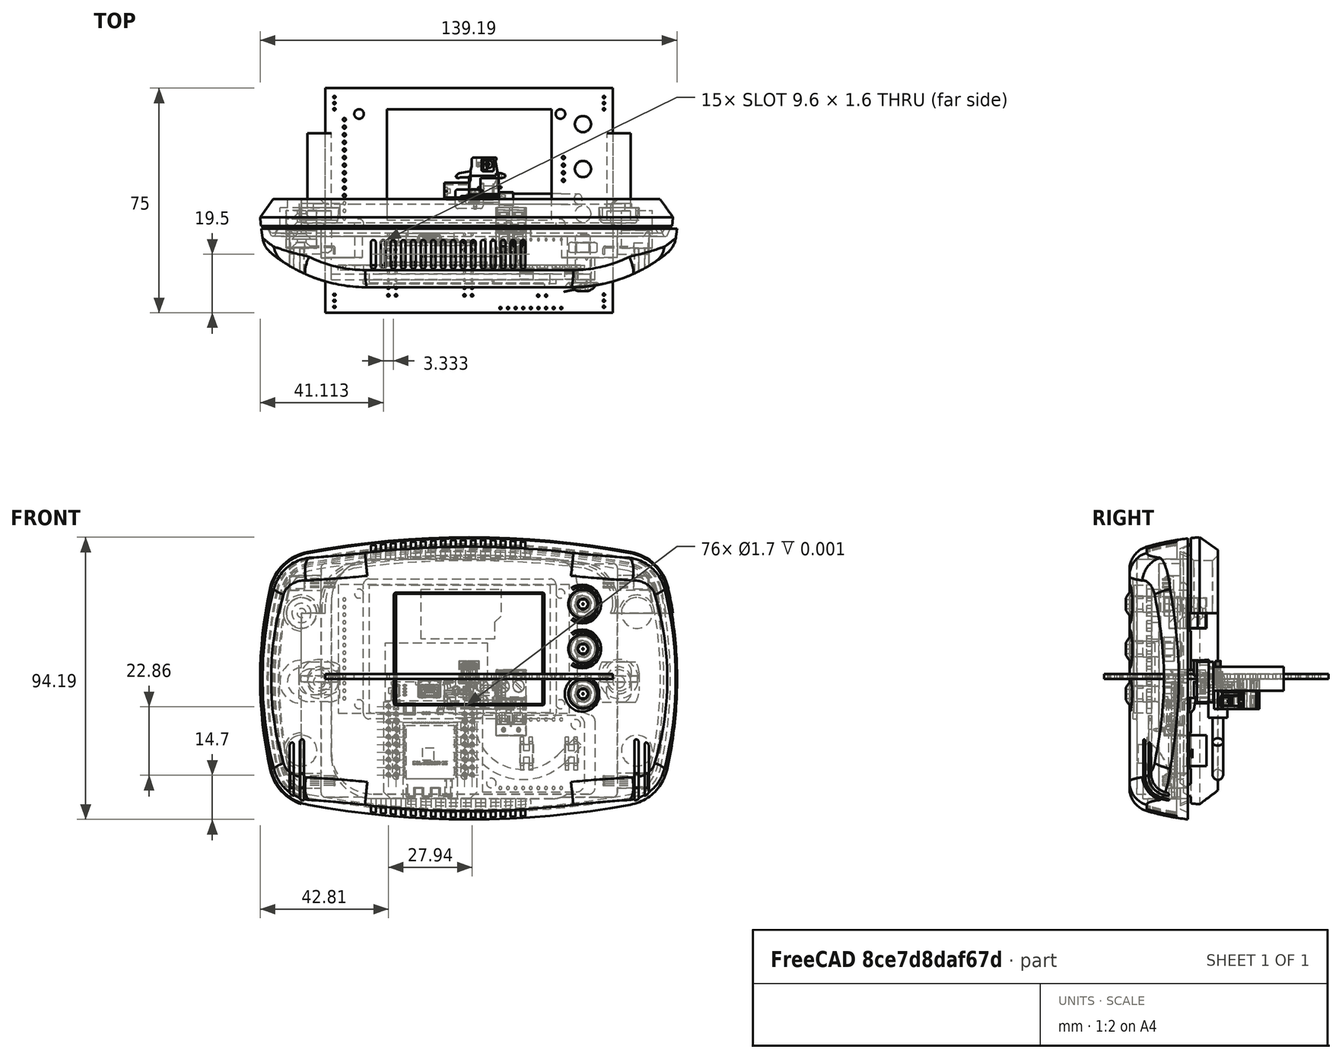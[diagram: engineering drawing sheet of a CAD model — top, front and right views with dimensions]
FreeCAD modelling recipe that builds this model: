
FCSTD DOCUMENT  (FreeCAD 1.0R38806 (Git))
Label: RoomThermostat with PCB
License: All rights reserved
LicenseURL: http://en.wikipedia.org/wiki/All_rights_reserved
objects: Sketcher::SketchObject×95, PartDesign::Body×35, PartDesign::Pocket×23, PartDesign::Pad×19, PartDesign::Mirrored×15, PartDesign::AdditivePipe×14, Part::Compound×8, Part::FeaturePython×8, PartDesign::SubtractivePipe×8, PartDesign::MultiTransform×7, Part::Feature×5, PartDesign::Revolution×5, PartDesign::Groove×5, PartDesign::LinearPattern×4, App::Part×4, App::LinkGroup×4, PartDesign::Fillet×3, PartDesign::Plane×2, Mesh::Feature×2, App::DocumentObjectGroup×1
note: 531 computed .brp shape members not serialized (recipe doc carries the construction recipe); baked Part::Feature solids carry a one-line shape summary decoded from their .brp

FEATURE [Sketcher::SketchObject] Sketch  label="gl base"
  ArcFitTolerance = 0
  AttachmentSupport = -> [XZ_Plane]
  FullyConstrained = true
  MakeInternals = false
  MapMode = 5
  Placement = pos=(0,0,0) rot=(1,0,0;1.5708rad)
  sketch-geometry (8):
    g0: LineSegment StartX=-33.28 StartY=21.36 StartZ=0 EndX=26.98 EndY=21.36 EndZ=0
    g1: LineSegment StartX=26.98 StartY=21.36 StartZ=0 EndX=26.98 EndY=-21.36 EndZ=0
    g2: LineSegment StartX=26.98 StartY=-21.36 StartZ=0 EndX=-33.28 EndY=-21.36 EndZ=0
    g3: LineSegment StartX=-33.28 StartY=-21.36 StartZ=0 EndX=-33.28 EndY=21.36 EndZ=0
    g4: LineSegment [constr] StartX=-24.48 StartY=18.36 StartZ=0 EndX=24.48 EndY=18.36 EndZ=0
    g5: LineSegment [constr] StartX=24.48 StartY=18.36 StartZ=0 EndX=24.48 EndY=-18.36 EndZ=0
    g6: LineSegment [constr] StartX=24.48 StartY=-18.36 StartZ=0 EndX=-24.48 EndY=-18.36 EndZ=0
    g7: LineSegment [constr] StartX=-24.48 StartY=-18.36 StartZ=0 EndX=-24.48 EndY=18.36 EndZ=0
  constraints (21):
    c: Coincident(g0,g1)
    c: Coincident(g1,g2)
    c: Coincident(g2,g3)
    c: Coincident(g3,g0)
    c: Horizontal(g2)
    c: Vertical(g3)
    c: DistanceX(g0,g0) = 60.26
    c: DistanceY(g1,g1) = 42.72
    c: Coincident(g4,g5)
    c: Coincident(g5,g6)
    c: Coincident(g6,g7)
    c: Coincident(g7,g4)
    c: Horizontal(g6)
    c: Vertical(g7)
    c: Horizontal(g0)
    c: Symmetric(g4,g4,g-2)
    c: Symmetric(g4,g5,g-1)
    c: DistanceX(g4,g4) = 48.96
    c: DistanceX(g4,g0) = 2.5
    c: DistanceY(g5,g5) = 36.72
    c: Symmetric(g0,g1,g-1)
FEATURE [PartDesign::Pad] Pad  label="GL Base"
  Direction = (1,1,1)
  Length = 4.2
  Length2 = 100
  Placement = pos=(0,0,0) rot=(1,0,0;1.5708rad)
  Profile = -> Sketch
  Reversed = true
  Suppressed = false
  Type = 0
FEATURE [Sketcher::SketchObject] Sketch001  label="gl active area"
  ArcFitTolerance = 0
  AttachmentSupport = -> [XZ_Plane]
  FullyConstrained = true
  MakeInternals = false
  MapMode = 5
  Placement = pos=(0,0,0) rot=(1,0,0;1.5708rad)
  sketch-geometry (4):
    g0: LineSegment StartX=-24.48 StartY=18.36 StartZ=0 EndX=24.48 EndY=18.36 EndZ=0
    g1: LineSegment StartX=24.48 StartY=18.36 StartZ=0 EndX=24.48 EndY=-18.36 EndZ=0
    g2: LineSegment StartX=24.48 StartY=-18.36 StartZ=0 EndX=-24.48 EndY=-18.36 EndZ=0
    g3: LineSegment StartX=-24.48 StartY=-18.36 StartZ=0 EndX=-24.48 EndY=18.36 EndZ=0
  constraints (10):
    c: Coincident(g0,g1)
    c: Coincident(g1,g2)
    c: Coincident(g2,g3)
    c: Coincident(g3,g0)
    c: Horizontal(g2)
    c: Vertical(g3)
    c: Symmetric(g0,g0,g-2)
    c: Symmetric(g0,g1,g-1)
    c: DistanceY(g1,g1) = 36.72
    c: DistanceX(g0,g0) = 48.96
FEATURE [PartDesign::Pad] Pad001  label="GL active area"
  BaseFeature = -> Pad
  Direction = (1,1,1)
  Length = 0.1
  Length2 = 100
  Placement = pos=(0,0,0) rot=(1,0,0;1.5708rad)
  Profile = -> Sketch001
  Suppressed = false
  Type = 0
FEATURE [PartDesign::Body] Body  label="Glass"
  AllowCompound = false
  Group = -> [Sketch,Pad,Sketch001,Pad001]
  Origin = -> Origin
  Tip = -> Pad001
FEATURE [Sketcher::SketchObject] Sketch003  label="pc skeleton"
  ArcFitTolerance = 0
  AttachmentSupport = -> [XZ_Plane001]
  FullyConstrained = true
  MakeInternals = false
  MapMode = 5
  Placement = pos=(0,0,0) rot=(1,0,0;1.5708rad)
  sketch-geometry (8):
    g0: LineSegment StartX=-33.28 StartY=21.36 StartZ=0 EndX=26.98 EndY=21.36 EndZ=0
    g1: LineSegment StartX=26.98 StartY=21.36 StartZ=0 EndX=26.98 EndY=-21.36 EndZ=0
    g2: LineSegment StartX=26.98 StartY=-21.36 StartZ=0 EndX=-33.28 EndY=-21.36 EndZ=0
    g3: LineSegment StartX=-33.28 StartY=-21.36 StartZ=0 EndX=-33.28 EndY=21.36 EndZ=0
    g4: LineSegment StartX=-24.48 StartY=18.36 StartZ=0 EndX=24.48 EndY=18.36 EndZ=0
    g5: LineSegment StartX=24.48 StartY=18.36 StartZ=0 EndX=24.48 EndY=-18.36 EndZ=0
    g6: LineSegment StartX=24.48 StartY=-18.36 StartZ=0 EndX=-24.48 EndY=-18.36 EndZ=0
    g7: LineSegment StartX=-24.48 StartY=-18.36 StartZ=0 EndX=-24.48 EndY=18.36 EndZ=0
  constraints (22):
    c: Coincident(g0,g1)
    c: Coincident(g1,g2)
    c: Coincident(g2,g3)
    c: Coincident(g3,g0)
    c: Horizontal(g2)
    c: Vertical(g3)
    c: DistanceX(g0,g0) = 60.26
    c: DistanceY(g1,g1) = 42.72
    c: Coincident(g4,g5)
    c: Coincident(g5,g6)
    c: Coincident(g6,g7)
    c: Coincident(g7,g4)
    c: Horizontal(g6)
    c: Vertical(g7)
    c: Horizontal(g0)
    c: Symmetric(g4,g4,g-2)
    c: Symmetric(g4,g5,g-1)
    c: DistanceX(g4,g4) = 48.96
    c: DistanceX(g4,g0) = 2.5
    c: DistanceY(g5,g5) = 36.72
    c: Symmetric(g0,g1,g-1)
    c: DistanceX(g0,g-1) = 33.28
FEATURE [Sketcher::SketchObject] Sketch002  label="pc base"
  ArcFitTolerance = 0
  AttachmentOffset = pos=(0,0,-4.2) rot=(0,0,1;0rad)
  AttachmentSupport = -> [XZ_Plane001]
  ExternalGeometry = -> [Sketch003]
  FullyConstrained = true
  MakeInternals = false
  MapMode = 5
  Placement = pos=(0,4.2,-9e-16) rot=(1,0,0;1.5708rad)
  sketch-geometry (12):
    g0: LineSegment StartX=33.49 StartY=21.45 StartZ=0 EndX=-43.69 EndY=21.45 EndZ=0
    g1: LineSegment StartX=-43.69 StartY=21.45 StartZ=0 EndX=-43.69 EndY=-21.45 EndZ=0
    g2: LineSegment StartX=-43.69 StartY=-21.45 StartZ=0 EndX=33.49 EndY=-21.45 EndZ=0
    g3: LineSegment StartX=33.49 StartY=-21.45 StartZ=0 EndX=33.49 EndY=21.45 EndZ=0
    g4: LineSegment [constr] StartX=-36.77 StartY=18.45 StartZ=0 EndX=30.49 EndY=18.45 EndZ=0
    g5: LineSegment [constr] StartX=30.49 StartY=18.45 StartZ=0 EndX=30.49 EndY=-18.45 EndZ=0
    g6: LineSegment [constr] StartX=30.49 StartY=-18.45 StartZ=0 EndX=-36.77 EndY=-18.45 EndZ=0
    g7: LineSegment [constr] StartX=-36.77 StartY=-18.45 StartZ=0 EndX=-36.77 EndY=18.45 EndZ=0
    g8: Circle CenterX=30.49 CenterY=18.45 CenterZ=0 NormalX=0 NormalY=0 NormalZ=1 AngleXU=0 Radius=1.5
    g9: Circle CenterX=30.49 CenterY=-18.45 CenterZ=0 NormalX=0 NormalY=0 NormalZ=1 AngleXU=0 Radius=1.5
    g10: Circle CenterX=-36.77 CenterY=-18.45 CenterZ=0 NormalX=0 NormalY=0 NormalZ=1 AngleXU=0 Radius=1.5
    g11: Circle CenterX=-36.77 CenterY=18.45 CenterZ=0 NormalX=0 NormalY=0 NormalZ=1 AngleXU=0 Radius=1.5
  constraints (31):
    c: Coincident(g0,g1)
    c: Coincident(g1,g2)
    c: Coincident(g2,g3)
    c: Coincident(g3,g0)
    c: Horizontal(g0)
    c: Horizontal(g2)
    c: Vertical(g1)
    c: Symmetric(g0,g2,g-1)
    c: DistanceX(g0,g-3) = 10.41
    c: DistanceX(g0,g0) = 77.18
    c: DistanceY(g3,g3) = 42.9
    c: Coincident(g4,g5)
    c: Coincident(g5,g6)
    c: Coincident(g6,g7)
    c: Coincident(g7,g4)
    c: Horizontal(g4)
    c: Horizontal(g6)
    c: Vertical(g7)
    c: Symmetric(g4,g5,g-1)
    c: Coincident(g8,g4)
    c: Coincident(g9,g5)
    c: Coincident(g10,g6)
    c: Coincident(g11,g4)
    c: Equal(g8,g11)
    c: Equal(g11,g10)
    c: Equal(g10,g9)
    c: Radius(g9) = 1.5
    c: DistanceX(g0,g11) = 6.92
    c: DistanceX(g8,g0) = 3
    c: DistanceY(g8,g0) = 3
    c: DistanceX(g0,g-1) = 43.69
FEATURE [PartDesign::Pad] Pad002  label="PC base"
  Direction = (1,1,1)
  Length = 1.6
  Length2 = 100
  Placement = pos=(0,0,0) rot=(1,0,0;1.5708rad)
  Profile = -> Sketch002
  Reversed = true
  Suppressed = false
  Type = 0
FEATURE [Sketcher::SketchObject] Sketch004  label="pc hole"
  ArcFitTolerance = 0
  AttachmentSupport = -> [XZ_Plane001]
  ExternalGeometry = -> [Sketch002]
  FullyConstrained = true
  MakeInternals = false
  MapMode = 5
  Placement = pos=(0,0,0) rot=(1,0,0;1.5708rad)
  sketch-geometry (1):
    g0: Circle CenterX=-41.69 CenterY=-16.51 CenterZ=0 NormalX=0 NormalY=0 NormalZ=1 AngleXU=0 Radius=0.5
  constraints (3):
    c: Radius(g0) = 0.5
    c: DistanceY(g0,g-1) = 16.51
    c: DistanceX(g0,g-1) = 41.69
FEATURE [PartDesign::Pocket] Pocket  label="PC FirstHole"
  BaseFeature = -> Pad002
  Direction = (1,1,1)
  Length = 5
  Length2 = 100
  Midplane = true
  Placement = pos=(0,0,0) rot=(1,0,0;1.5708rad)
  Profile = -> Sketch004
  Suppressed = false
  Type = 1
FEATURE [PartDesign::LinearPattern] LinearPattern  label="PC OtherHoles"
  BaseFeature = -> Pocket
  Direction = -> Z_Axis001
  Length = 33.02
  Mode = 0
  Occurrences = 14
  Offset = 2.54
  Originals = -> [Pocket]
  Placement = pos=(0,0,0) rot=(1,0,0;1.5708rad)
  Suppressed = false
  TransformMode = 0
FEATURE [PartDesign::Body] Body001  label="PCB"
  AllowCompound = false
  Group = -> [Sketch002,Sketch003,Pad002,Sketch004,Pocket,LinearPattern]
  Origin = -> Origin001
  Tip = -> LinearPattern
FEATURE [Sketcher::SketchObject] Sketch006  label="sd skeleton"
  ArcFitTolerance = 0
  AttachmentSupport = -> [XZ_Plane002]
  FullyConstrained = true
  MakeInternals = false
  MapMode = 5
  Placement = pos=(0,0,0) rot=(1,0,0;1.5708rad)
  sketch-geometry (8):
    g0: LineSegment StartX=-33.28 StartY=21.36 StartZ=0 EndX=26.98 EndY=21.36 EndZ=0
    g1: LineSegment StartX=26.98 StartY=21.36 StartZ=0 EndX=26.98 EndY=-21.36 EndZ=0
    g2: LineSegment StartX=26.98 StartY=-21.36 StartZ=0 EndX=-33.28 EndY=-21.36 EndZ=0
    g3: LineSegment StartX=-33.28 StartY=-21.36 StartZ=0 EndX=-33.28 EndY=21.36 EndZ=0
    g4: LineSegment StartX=-24.48 StartY=18.36 StartZ=0 EndX=24.48 EndY=18.36 EndZ=0
    g5: LineSegment StartX=24.48 StartY=18.36 StartZ=0 EndX=24.48 EndY=-18.36 EndZ=0
    g6: LineSegment StartX=24.48 StartY=-18.36 StartZ=0 EndX=-24.48 EndY=-18.36 EndZ=0
    g7: LineSegment StartX=-24.48 StartY=-18.36 StartZ=0 EndX=-24.48 EndY=18.36 EndZ=0
  constraints (21):
    c: Coincident(g0,g1)
    c: Coincident(g1,g2)
    c: Coincident(g2,g3)
    c: Coincident(g3,g0)
    c: Horizontal(g2)
    c: Vertical(g3)
    c: DistanceX(g0,g0) = 60.26
    c: DistanceY(g1,g1) = 42.72
    c: Coincident(g4,g5)
    c: Coincident(g5,g6)
    c: Coincident(g6,g7)
    c: Coincident(g7,g4)
    c: Horizontal(g6)
    c: Vertical(g7)
    c: Horizontal(g0)
    c: Symmetric(g4,g4,g-2)
    c: Symmetric(g4,g5,g-1)
    c: DistanceX(g4,g4) = 48.96
    c: DistanceX(g4,g0) = 2.5
    c: DistanceY(g5,g5) = 36.72
    c: Symmetric(g0,g1,g-1)
FEATURE [Sketcher::SketchObject] Sketch005  label="sd base"
  ArcFitTolerance = 0
  AttachmentOffset = pos=(0,0,-5.8) rot=(0,0,1;0rad)
  AttachmentSupport = -> [XZ_Plane002]
  ExternalGeometry = -> [Sketch006]
  FullyConstrained = true
  MakeInternals = false
  MapMode = 5
  Placement = pos=(0,5.8,-1.3e-15) rot=(1,0,0;1.5708rad)
  sketch-geometry (6):
    g0: LineSegment StartX=-16.02 StartY=19.96 StartZ=0 EndX=10.58 EndY=19.96 EndZ=0
    g1: LineSegment StartX=10.58 StartY=19.96 StartZ=0 EndX=10.58 EndY=10.96 EndZ=0
    g2: LineSegment StartX=8.48 StartY=3.26 StartZ=0 EndX=-16.02 EndY=3.26 EndZ=0
    g3: LineSegment StartX=-16.02 StartY=3.26 StartZ=0 EndX=-16.02 EndY=19.96 EndZ=0
    g4: LineSegment StartX=10.58 StartY=10.96 StartZ=0 EndX=8.48 EndY=8.86 EndZ=0
    g5: LineSegment StartX=8.48 StartY=8.86 StartZ=0 EndX=8.48 EndY=3.26 EndZ=0
  constraints (18):
    c: Coincident(g0,g1)
    c: Coincident(g2,g3)
    c: Coincident(g3,g0)
    c: Horizontal(g0)
    c: Horizontal(g2)
    c: Vertical(g1)
    c: Vertical(g3)
    c: DistanceX(g0,g-3) = 16.4
    c: DistanceX(g0,g0) = 26.6
    c: DistanceY(g0,g-3) = 1.4
    c: Coincident(g4,g5)
    c: Vertical(g5)
    c: Coincident(g2,g5)
    c: Coincident(g4,g1)
    c: DistanceY(g2,g0) = 16.7
    c: DistanceX(g2,g2) = 24.5
    c: DistanceY(g5,g5) = 5.6
    c: Angle(g5,g4) = 2.35619
FEATURE [PartDesign::Pad] Pad003  label="SD Base"
  Direction = (1,1,1)
  Length = 2.9
  Length2 = 100
  Placement = pos=(0,0,0) rot=(1,0,0;1.5708rad)
  Profile = -> Sketch005
  Reversed = true
  Suppressed = false
  Type = 0
FEATURE [PartDesign::Body] Body002  label="SD Card Slot"
  AllowCompound = false
  Group = -> [Sketch005,Sketch006,Pad003]
  Origin = -> Origin002
  Tip = -> Pad003
FEATURE [Sketcher::SketchObject] Sketch009  label="cm skeleton"
  ArcFitTolerance = 0
  AttachmentOffset = pos=(0,0,-4.2) rot=(0,0,1;0rad)
  AttachmentSupport = -> [XZ_Plane003]
  ExternalGeometry = -> [Sketch003]
  FullyConstrained = true
  MakeInternals = false
  MapMode = 5
  Placement = pos=(0,4.2,-9e-16) rot=(1,0,0;1.5708rad)
  sketch-geometry (12):
    g0: LineSegment StartX=33.49 StartY=21.45 StartZ=0 EndX=-43.69 EndY=21.45 EndZ=0
    g1: LineSegment StartX=-43.69 StartY=21.45 StartZ=0 EndX=-43.69 EndY=-21.45 EndZ=0
    g2: LineSegment StartX=-43.69 StartY=-21.45 StartZ=0 EndX=33.49 EndY=-21.45 EndZ=0
    g3: LineSegment StartX=33.49 StartY=-21.45 StartZ=0 EndX=33.49 EndY=21.45 EndZ=0
    g4: LineSegment [constr] StartX=-36.77 StartY=18.45 StartZ=0 EndX=30.49 EndY=18.45 EndZ=0
    g5: LineSegment [constr] StartX=30.49 StartY=18.45 StartZ=0 EndX=30.49 EndY=-18.45 EndZ=0
    g6: LineSegment [constr] StartX=30.49 StartY=-18.45 StartZ=0 EndX=-36.77 EndY=-18.45 EndZ=0
    g7: LineSegment [constr] StartX=-36.77 StartY=-18.45 StartZ=0 EndX=-36.77 EndY=18.45 EndZ=0
    g8: Circle CenterX=30.49 CenterY=18.45 CenterZ=0 NormalX=0 NormalY=0 NormalZ=1 AngleXU=0 Radius=1.5
    g9: Circle CenterX=30.49 CenterY=-18.45 CenterZ=0 NormalX=0 NormalY=0 NormalZ=1 AngleXU=0 Radius=1.5
    g10: Circle CenterX=-36.77 CenterY=-18.45 CenterZ=0 NormalX=0 NormalY=0 NormalZ=1 AngleXU=0 Radius=1.5
    g11: Circle CenterX=-36.77 CenterY=18.45 CenterZ=0 NormalX=0 NormalY=0 NormalZ=1 AngleXU=0 Radius=1.5
  constraints (30):
    c: Coincident(g0,g1)
    c: Coincident(g1,g2)
    c: Coincident(g2,g3)
    c: Coincident(g3,g0)
    c: Horizontal(g0)
    c: Horizontal(g2)
    c: Vertical(g1)
    c: Symmetric(g0,g2,g-1)
    c: DistanceX(g0,g-3) = 10.41
    c: DistanceX(g0,g0) = 77.18
    c: DistanceY(g3,g3) = 42.9
    c: Coincident(g4,g5)
    c: Coincident(g5,g6)
    c: Coincident(g6,g7)
    c: Coincident(g7,g4)
    c: Horizontal(g4)
    c: Horizontal(g6)
    c: Vertical(g7)
    c: Symmetric(g4,g5,g-1)
    c: Coincident(g8,g4)
    c: Coincident(g9,g5)
    c: Coincident(g10,g6)
    c: Coincident(g11,g4)
    c: Equal(g8,g11)
    c: Equal(g11,g10)
    c: Equal(g10,g9)
    c: Radius(g9) = 1.5
    c: DistanceX(g0,g11) = 6.92
    c: DistanceX(g8,g0) = 3
    c: DistanceY(g8,g0) = 3
FEATURE [Sketcher::SketchObject] Sketch010  label="cm components"
  ArcFitTolerance = 0
  AttachmentOffset = pos=(0,0,-5.8) rot=(0,0,1;0rad)
  AttachmentSupport = -> [XZ_Plane003]
  ExternalGeometry = -> [Sketch009]
  FullyConstrained = true
  MakeInternals = false
  MapMode = 5
  Placement = pos=(0,5.8,-1.3e-15) rot=(1,0,0;1.5708rad)
  sketch-geometry (4):
    g0: LineSegment StartX=-27.99 StartY=2.05 StartZ=0 EndX=6.01 EndY=2.05 EndZ=0
    g1: LineSegment StartX=6.01 StartY=2.05 StartZ=0 EndX=6.01 EndY=-17.45 EndZ=0
    g2: LineSegment StartX=6.01 StartY=-17.45 StartZ=0 EndX=-27.99 EndY=-17.45 EndZ=0
    g3: LineSegment StartX=-27.99 StartY=-17.45 StartZ=0 EndX=-27.99 EndY=2.05 EndZ=0
  constraints (12):
    c: Coincident(g0,g1)
    c: Coincident(g1,g2)
    c: Coincident(g2,g3)
    c: Coincident(g3,g0)
    c: Horizontal(g0)
    c: Horizontal(g2)
    c: Vertical(g1)
    c: Vertical(g3)
    c: DistanceX(g-3,g2) = 15.7
    c: DistanceX(g0,g0) = 34
    c: DistanceY(g-3,g2) = 4
    c: DistanceY(g1,g1) = 19.5
FEATURE [PartDesign::Pad] Pad004
  Direction = (1,1,1)
  Length = 1
  Length2 = 100
  Placement = pos=(0,0,0) rot=(1,0,0;1.5708rad)
  Profile = -> Sketch010
  Reversed = true
  Suppressed = false
  Type = 0
FEATURE [PartDesign::Body] Body003  label="Components"
  AllowCompound = false
  Group = -> [Sketch009,Sketch010,Pad004]
  Origin = -> Origin003
  Tip = -> Pad004
FEATURE [Part::Compound] Compound  label="Display"
  Links = -> [Body,Body001,Body002,Body003]
  Placement = pos=(0,-27.92,10) rot=(0,0,1;0rad)
FEATURE [Part::FeaturePython] Screw  label="M5x16-Screw"  # Fasteners workbench fastener (typed FeaturePython)
  Placement = pos=(38,-28,25) rot=(1,0,0;1.5708rad)
  diameter = 3
  invert = false
  length = 4
  lengthCustom = 16
  matchOuter = false
  offset = 0
  thread = false
  type = 40
FEATURE [Part::FeaturePython] Screw001  label="M5x16-Screw015"  # Fasteners workbench fastener (typed FeaturePython)
  Placement = pos=(38,-28,10) rot=(1,0,0;1.5708rad)
  diameter = 3
  invert = false
  length = 4
  lengthCustom = 16
  matchOuter = false
  offset = 0
  thread = false
  type = 40
FEATURE [Part::FeaturePython] Screw002  label="M5x16-Screw016"  # Fasteners workbench fastener (typed FeaturePython)
  Placement = pos=(38,-28,-5) rot=(1,0,0;1.5708rad)
  diameter = 3
  invert = false
  length = 4
  lengthCustom = 16
  matchOuter = false
  offset = 0
  thread = false
  type = 40
FEATURE [Part::FeaturePython] Nut  label="M5-Nut"  # Fasteners workbench fastener (typed FeaturePython)
  Placement = pos=(38,-18,25) rot=(-1,0,0;1.5708rad)
  diameter = 7
  invert = false
  matchOuter = false
  offset = 0
  thread = false
  type = 7
FEATURE [Part::FeaturePython] Nut001  label="M5-Nut015"  # Fasteners workbench fastener (typed FeaturePython)
  Placement = pos=(38,-18,10) rot=(-1,0,0;1.5708rad)
  diameter = 7
  invert = false
  matchOuter = false
  offset = 0
  thread = false
  type = 7
FEATURE [Part::FeaturePython] Nut002  label="M5-Nut016"  # Fasteners workbench fastener (typed FeaturePython)
  Placement = pos=(38,-18,-5) rot=(-1,0,0;1.5708rad)
  diameter = 7
  invert = false
  matchOuter = false
  offset = 0
  thread = false
  type = 7
FEATURE [Sketcher::SketchObject] Sketch023  label="cable_trj"
  ArcFitTolerance = 0
  AttachmentSupport = -> [XZ_Plane015]
  FullyConstrained = true
  MakeInternals = false
  MapMode = 5
  Placement = pos=(0,0,0) rot=(1,0,0;1.5708rad)
  sketch-geometry (3):
    g0: LineSegment StartX=0 StartY=-13 StartZ=0 EndX=0 EndY=-14 EndZ=0
    g1: ArcOfCircle CenterX=18 CenterY=-14 CenterZ=0 NormalX=0 NormalY=0 NormalZ=1 AngleXU=0 Radius=18 StartAngle=3.14159 EndAngle=5.49779
    g2: LineSegment StartX=30.7279 StartY=-26.7279 StartZ=0 EndX=36.3848 EndY=-21.0711 EndZ=0
  constraints (9):
    c: PointOnObject(g0,g-2)
    c: DistanceY(g0,g-1) = 13
    c: DistanceY(g0,g0) = 1
    c: Tangent(g0,g1) = -1.5708
    c: Radius(g1) = 18
    c: Tangent(g1,g2) = -1.5708
    c: Angle(g2,g-2) = 0.785398
    c: Distance(g2) = 8
    c: Vertical(g0)
FEATURE [Sketcher::SketchObject] Sketch024  label="cable_crs"
  ArcFitTolerance = 0
  AttachmentOffset = pos=(0,0,-13) rot=(0,0,1;0rad)
  AttachmentSupport = -> [XY_Plane015]
  FullyConstrained = true
  MakeInternals = false
  MapMode = 5
  Placement = pos=(0,0,-13) rot=(0,0,1;0rad)
  sketch-geometry (1):
    g0: Circle CenterX=0 CenterY=0 CenterZ=0 NormalX=0 NormalY=0 NormalZ=1 AngleXU=0 Radius=1.75
  constraints (2):
    c: Coincident(g0,g-1)
    c: Diameter(g0) = 3.5
FEATURE [PartDesign::AdditivePipe] AdditivePipe
  AuxilleryCurvelinear = true
  AuxillerySpineTangent = false
  Binormal = (0,0,0)
  Mode = 0
  Profile = -> Sketch024
  Spine = -> Sketch023
  SpineTangent = false
  Suppressed = false
  Transformation = 0
  Transition = 0
FEATURE [PartDesign::Body] Body015  label="Cable"
  AllowCompound = false
  Group = -> [Sketch023,Sketch024,AdditivePipe]
  Origin = -> Origin015
  Tip = -> AdditivePipe
FEATURE [Part::Feature] Part__Feature001  label="Micro_USB_Plug_Connector"
  shape: bbox 6.85 x 2.55 x 7.5 mm, 144 faces, 4 solids (baked)
FEATURE [Sketcher::SketchObject] Sketch025  label="Sketch002"
  ArcFitTolerance = 0
  AttachmentSupport = -> [XY_Plane016]
  FullyConstrained = true
  MakeInternals = false
  MapMode = 5
  sketch-geometry (12):
    g0: LineSegment StartX=-3.75 StartY=3.175 StartZ=0 EndX=3.75 EndY=3.175 EndZ=0
    g1: LineSegment StartX=4.65 StartY=2.275 StartZ=0 EndX=4.65 EndY=-2.275 EndZ=0
    g2: LineSegment StartX=3.75 StartY=-3.175 StartZ=0 EndX=-3.75 EndY=-3.175 EndZ=0
    g3: LineSegment StartX=-4.65 StartY=-2.275 StartZ=0 EndX=-4.65 EndY=2.275 EndZ=0
    g4: LineSegment [constr] StartX=-3.75 StartY=2.275 StartZ=0 EndX=3.75 EndY=2.275 EndZ=0
    g5: LineSegment [constr] StartX=3.75 StartY=2.275 StartZ=0 EndX=3.75 EndY=-2.275 EndZ=0
    g6: LineSegment [constr] StartX=3.75 StartY=-2.275 StartZ=0 EndX=-3.75 EndY=-2.275 EndZ=0
    g7: LineSegment [constr] StartX=-3.75 StartY=-2.275 StartZ=0 EndX=-3.75 EndY=2.275 EndZ=0
    g8: ArcOfCircle CenterX=3.75 CenterY=2.275 CenterZ=0 NormalX=0 NormalY=0 NormalZ=1 AngleXU=0 Radius=0.9 StartAngle=0 EndAngle=1.5708
    g9: ArcOfCircle CenterX=3.75 CenterY=-2.275 CenterZ=0 NormalX=0 NormalY=0 NormalZ=1 AngleXU=0 Radius=0.9 StartAngle=4.71239 EndAngle=6.28319
    g10: ArcOfCircle CenterX=-3.75 CenterY=-2.275 CenterZ=0 NormalX=0 NormalY=0 NormalZ=1 AngleXU=0 Radius=0.9 StartAngle=3.14159 EndAngle=4.71239
    g11: ArcOfCircle CenterX=-3.75 CenterY=2.275 CenterZ=0 NormalX=0 NormalY=0 NormalZ=1 AngleXU=0 Radius=0.9 StartAngle=1.5708 EndAngle=3.14159
  constraints (26):
    c: Horizontal(g0)
    c: Horizontal(g2)
    c: Vertical(g1)
    c: Vertical(g3)
    c: Coincident(g4,g5)
    c: Coincident(g5,g6)
    c: Coincident(g6,g7)
    c: Coincident(g7,g4)
    c: Horizontal(g6)
    c: Symmetric(g4,g4,g-2)
    c: Symmetric(g4,g5,g-1)
    c: Tangent(g1,g8) = 1.5708
    c: Tangent(g0,g8) = 1.5708
    c: Tangent(g1,g9) = 1.5708
    c: Tangent(g2,g9) = 1.5708
    c: Tangent(g2,g10) = 1.5708
    c: Tangent(g3,g10) = 1.5708
    c: Tangent(g0,g11) = 1.5708
    c: Tangent(g3,g11) = 1.5708
    c: Coincident(g4,g8)
    c: Coincident(g5,g9)
    c: Coincident(g6,g10)
    c: Coincident(g4,g11)
    c: DistanceX(g3,g1) = 9.3
    c: DistanceY(g2,g0) = 6.35
    c: Radius(g8) = 0.9
FEATURE [PartDesign::Pad] Pad015
  Direction = (1,1,1)
  Length = 13
  Length2 = 100
  Profile = -> Sketch025
  Reversed = true
  Suppressed = false
  Type = 0
FEATURE [PartDesign::Body] Body016  label="Housing"
  AllowCompound = false
  Group = -> [Sketch025,Pad015]
  Origin = -> Origin016
  Tip = -> Pad015
FEATURE [Part::Feature] Part__Feature004  label="mstb_2.5-2-g"
  Placement = pos=(-36.6267,-37.7727,-2.5) rot=(0,0,1;0rad)
  shape: bbox 12 x 12.1 x 10 mm, 208 faces (baked)
FEATURE [App::Part] mstb_2_5_2_g  label="mstb_2.5-2-g001"
  Group = -> [Part__Feature004]
  Origin = -> Origin023
FEATURE [Part::Feature] Part__Feature005  label="mstb_2.5-2-st"
  Placement = pos=(-48.6267,-39.1127,-2.5) rot=(0,0,1;0rad)
  shape: bbox 18.2 x 15 x 10 mm, 170 faces (baked)
FEATURE [App::Part] mstb_2_5_2_st  label="mstb_2.5-2-st001"
  Group = -> [Part__Feature005]
  Origin = -> Origin024
  Placement = pos=(12.1,1.35,0) rot=(0,0,1;0rad)
FEATURE [Part::Compound] Compound004  label="Phoenix"
  Links = -> [mstb_2_5_2_g,mstb_2_5_2_st]
  Placement = pos=(9,-18,-19) rot=(0,-1,0;1.5708rad)
FEATURE [Part::Feature] Part__Feature  label="MH-ET_LIVE_MiniKit"
  Placement = pos=(0,19.5,7e-15) rot=(1,0,0;1.5708rad)
  shape: bbox 31.02 x 39.44 x 99.68 mm, 5494 faces, 23 solids (baked)
FEATURE [Part::Compound] Compound005  label="ESP32"
  Links = -> [Part__Feature]
  Placement = pos=(-13,-15.5,-0.96) rot=(-1,0,0;1.5708rad)
FEATURE [Sketcher::SketchObject] Sketch032
  ArcFitTolerance = 0
  AttachmentSupport = -> [XY_Plane025]
  FullyConstrained = true
  MakeInternals = false
  MapMode = 5
  sketch-geometry (13):
    g0: LineSegment StartX=9.8 StartY=17.1 StartZ=0 EndX=-9.8 EndY=17.1 EndZ=0
    g1: LineSegment StartX=-12.8 StartY=14.1 StartZ=0 EndX=-12.8 EndY=-17.1 EndZ=0
    g2: LineSegment StartX=-12.8 StartY=-17.1 StartZ=0 EndX=12.8 EndY=-17.1 EndZ=0
    g3: LineSegment StartX=12.8 StartY=-17.1 StartZ=0 EndX=12.8 EndY=14.1 EndZ=0
    g4: GeomPoint X=12.8 Y=17.1 Z=0
    g5: ArcOfCircle CenterX=9.8 CenterY=14.1 CenterZ=0 NormalX=0 NormalY=0 NormalZ=1 AngleXU=0 Radius=3 StartAngle=0 EndAngle=1.5708
    g6: ArcOfCircle CenterX=-9.8 CenterY=14.1 CenterZ=0 NormalX=0 NormalY=0 NormalZ=1 AngleXU=0 Radius=3 StartAngle=1.5708 EndAngle=3.14159
    g7: Circle CenterX=-9.8 CenterY=14.1 CenterZ=0 NormalX=0 NormalY=0 NormalZ=1 AngleXU=0 Radius=1.6
    g8: Circle CenterX=9.8 CenterY=-14.1 CenterZ=0 NormalX=0 NormalY=0 NormalZ=1 AngleXU=0 Radius=1.6
    g9: LineSegment [constr] StartX=-9.8 StartY=14.1 StartZ=0 EndX=9.8 EndY=14.1 EndZ=0
    g10: LineSegment [constr] StartX=9.8 StartY=14.1 StartZ=0 EndX=9.8 EndY=-14.1 EndZ=0
    g11: LineSegment [constr] StartX=9.8 StartY=-14.1 StartZ=0 EndX=-9.8 EndY=-14.1 EndZ=0
    g12: LineSegment [constr] StartX=-9.8 StartY=-14.1 StartZ=0 EndX=-9.8 EndY=14.1 EndZ=0
  constraints (29):
    c: Vertical(g1)
    c: Symmetric(g1,g3,g-2)
    c: PointOnObject(g4,g0)
    c: Symmetric(g4,g2,g-1)
    c: Symmetric(g2,g2,g-2)
    c: Tangent(g3,g5) = -1.5708
    c: Tangent(g0,g5) = -1.5708
    c: Tangent(g0,g6) = -1.5708
    c: Tangent(g1,g6) = -1.5708
    c: Symmetric(g5,g6,g-2)
    c: Coincident(g1,g2)
    c: DistanceY(g2,g0) = 34.2
    c: Vertical(g3)
    c: DistanceX(g1,g3) = 25.6
    c: Radius(g5) = 3
    c: Coincident(g7,g6)
    c: Diameter(g7) = 3.2
    c: Coincident(g9,g10)
    c: Coincident(g10,g11)
    c: Coincident(g11,g12)
    c: Coincident(g12,g9)
    c: Horizontal(g11)
    c: Vertical(g12)
    c: Coincident(g9,g6)
    c: Coincident(g10,g8)
    c: Symmetric(g6,g9,g-2)
    c: Symmetric(g5,g8,g-1)
    c: Equal(g8,g7)
    c: DistanceY(g1,g-1) = 17.1
FEATURE [PartDesign::Pad] Pad017
  Direction = (1,1,1)
  Length = 1
  Length2 = 100
  Profile = -> Sketch032
  Reversed = true
  Suppressed = false
  Type = 0
FEATURE [Sketcher::SketchObject] Sketch033
  ArcFitTolerance = 0
  AttachmentSupport = -> [YZ_Plane026]
  FullyConstrained = false
  MakeInternals = false
  MapMode = 5
  Placement = pos=(0,0,0) rot=(0.57735,0.57735,0.57735;2.0944rad)
  sketch-geometry (4):
    g0: LineSegment StartX=-2.25 StartY=3.6 StartZ=0 EndX=2.25 EndY=3.6 EndZ=0
    g1: LineSegment StartX=2.25 StartY=3.6 StartZ=0 EndX=2.25 EndY=0 EndZ=0
    g2: LineSegment StartX=2.25 StartY=0 StartZ=0 EndX=-2.25 EndY=0 EndZ=0
    g3: LineSegment StartX=-2.25 StartY=0 StartZ=0 EndX=-2.25 EndY=3.6 EndZ=0
  constraints (11):
    c: Coincident(g0,g1)
    c: Coincident(g1,g2)
    c: Coincident(g2,g3)
    c: Coincident(g3,g0)
    c: Horizontal(g2)
    c: Vertical(g1)
    c: Vertical(g3)
    c: DistanceX(g0,g0) = 4.5
    c: DistanceY(g1,g1) = 3.6
    c: PointOnObject(g1,g-1)
    c: Symmetric(g0,g0,g-2)
FEATURE [PartDesign::Pad] Pad018
  Direction = (1,1,1)
  Length = 6.3
  Length2 = 100
  Midplane = true
  Placement = pos=(0,0,0) rot=(0.57735,0.57735,0.57735;2.0944rad)
  Profile = -> Sketch033
  Suppressed = false
  Type = 0
FEATURE [PartDesign::Body] Body021  label="BodyDevice003"
  AllowCompound = false
  Group = -> [Sketch033,Pad018]
  Origin = -> Origin026
  Placement = pos=(0,14.75,0) rot=(0,0,1;0rad)
  Tip = -> Pad018
FEATURE [Sketcher::SketchObject] Sketch034
  ArcFitTolerance = 0
  AttachmentSupport = -> [XZ_Plane027]
  FullyConstrained = false
  MakeInternals = false
  MapMode = 5
  Placement = pos=(0,0,0) rot=(1,0,0;1.5708rad)
  sketch-geometry (10):
    g0: LineSegment StartX=0 StartY=1.9 StartZ=0 EndX=3.2 EndY=1.9 EndZ=0
    g1: LineSegment StartX=3.2 StartY=1.4 StartZ=0 EndX=0 EndY=1.4 EndZ=0
    g2: LineSegment StartX=0 StartY=1.4 StartZ=0 EndX=0 EndY=1.9 EndZ=0
    g3: LineSegment StartX=4 StartY=0.5 StartZ=0 EndX=5.5 EndY=0.5 EndZ=0
    g4: LineSegment StartX=5.5 StartY=0.5 StartZ=0 EndX=5.5 EndY=0 EndZ=0
    g5: LineSegment StartX=5.5 StartY=0 StartZ=0 EndX=4 EndY=0 EndZ=0
    g6: LineSegment StartX=3.2 StartY=1.4 StartZ=0 EndX=3.5221 EndY=0.352981 EndZ=0
    g7: LineSegment StartX=4 StartY=0.5 StartZ=0 EndX=3.6779 EndY=1.54702 EndZ=0
    g8: ArcOfCircle CenterX=3.2 CenterY=1.4 CenterZ=0 NormalX=0 NormalY=0 NormalZ=1 AngleXU=0 Radius=0.5 StartAngle=0.29845 EndAngle=1.5708
    g9: ArcOfCircle CenterX=4 CenterY=0.5 CenterZ=0 NormalX=0 NormalY=0 NormalZ=1 AngleXU=0 Radius=0.5 StartAngle=3.44004 EndAngle=4.71239
  constraints (26):
    c: Coincident(g1,g2)
    c: Coincident(g2,g0)
    c: Horizontal(g0)
    c: Horizontal(g1)
    c: Vertical(g2)
    c: PointOnObject(g0,g-2)
    c: Coincident(g3,g4)
    c: Coincident(g4,g5)
    c: Horizontal(g3)
    c: Horizontal(g5)
    c: Vertical(g4)
    c: PointOnObject(g4,g-1)
    c: Tangent(g0,g8) = 1.5708
    c: Tangent(g7,g8) = -1.5708
    c: Tangent(g6,g9) = -1.5708
    c: Tangent(g5,g9) = 1.5708
    c: Coincident(g3,g7)
    c: Coincident(g3,g9)
    c: Coincident(g1,g6)
    c: Coincident(g1,g8)
    c: Parallel(g6,g7)
    c: DistanceX(g3) = 5.5
    c: DistanceY(g4,g4) = 0.5
    c: DistanceX(g1) = 3.2
    c: DistanceY(g1) = 1.4
    c: DistanceX(g1,g3) = 0.8
FEATURE [PartDesign::Pad] Pad019
  Direction = (1,1,1)
  Length = 4
  Length2 = 100
  Midplane = true
  Placement = pos=(0,0,0) rot=(1,0,0;1.5708rad)
  Profile = -> Sketch034
  Suppressed = false
  Type = 0
FEATURE [PartDesign::Mirrored] Mirrored005
  BaseFeature = -> Pad019
  MirrorPlane = -> YZ_Plane027
  Originals = -> [Pad019]
  Placement = pos=(0,0,0) rot=(1,0,0;1.5708rad)
  Suppressed = false
  TransformMode = 0
FEATURE [Sketcher::SketchObject] Sketch035
  ArcFitTolerance = 0
  AttachmentSupport = -> [XY_Plane027]
  FullyConstrained = false
  MakeInternals = false
  MapMode = 5
  sketch-geometry (4):
    g0: LineSegment StartX=6 StartY=0.9 StartZ=0 EndX=1 EndY=0.9 EndZ=0
    g1: LineSegment StartX=1 StartY=0.9 StartZ=0 EndX=1 EndY=-0.9 EndZ=0
    g2: LineSegment StartX=1 StartY=-0.9 StartZ=0 EndX=6 EndY=-0.9 EndZ=0
    g3: LineSegment StartX=6 StartY=-0.9 StartZ=0 EndX=6 EndY=0.9 EndZ=0
  constraints (11):
    c: Coincident(g0,g1)
    c: Coincident(g1,g2)
    c: Coincident(g2,g3)
    c: Coincident(g3,g0)
    c: Horizontal(g0)
    c: Horizontal(g2)
    c: Vertical(g1)
    c: Symmetric(g0,g2,g-1)
    c: DistanceY(g3,g3) = 1.8
    c: DistanceX(g0) = 6
    c: DistanceX(g0) = 1
FEATURE [PartDesign::Pocket] Pocket005
  BaseFeature = -> Mirrored005
  Direction = (1,1,1)
  Length = 5
  Length2 = 100
  Midplane = true
  Placement = pos=(0,0,0) rot=(1,0,0;1.5708rad)
  Profile = -> Sketch035
  Suppressed = false
  Type = 1
FEATURE [PartDesign::Mirrored] Mirrored006
  BaseFeature = -> Pocket005
  MirrorPlane = -> YZ_Plane027
  Originals = -> [Pocket005]
  Placement = pos=(0,0,0) rot=(1,0,0;1.5708rad)
  Suppressed = false
  TransformMode = 0
FEATURE [PartDesign::Body] Body022  label="PinsDevice003"
  AllowCompound = false
  Group = -> [Sketch034,Pad019,Mirrored005,Sketch035,Pocket005,Mirrored006]
  Origin = -> Origin027
  Placement = pos=(0,14.75,0) rot=(0,0,1;0rad)
  Tip = -> Mirrored006
FEATURE [Sketcher::SketchObject] Sketch036
  ArcFitTolerance = 0
  AttachmentSupport = -> [YZ_Plane007]
  FullyConstrained = false
  MakeInternals = false
  MapMode = 5
  Placement = pos=(0,0,0) rot=(0.57735,0.57735,0.57735;2.0944rad)
  sketch-geometry (4):
    g0: LineSegment StartX=-2.25 StartY=3.6 StartZ=0 EndX=2.25 EndY=3.6 EndZ=0
    g1: LineSegment StartX=2.25 StartY=3.6 StartZ=0 EndX=2.25 EndY=0 EndZ=0
    g2: LineSegment StartX=2.25 StartY=0 StartZ=0 EndX=-2.25 EndY=0 EndZ=0
    g3: LineSegment StartX=-2.25 StartY=0 StartZ=0 EndX=-2.25 EndY=3.6 EndZ=0
  constraints (11):
    c: Coincident(g0,g1)
    c: Coincident(g1,g2)
    c: Coincident(g2,g3)
    c: Coincident(g3,g0)
    c: Horizontal(g2)
    c: Vertical(g1)
    c: Vertical(g3)
    c: DistanceX(g0,g0) = 4.5
    c: DistanceY(g1,g1) = 3.6
    c: PointOnObject(g1,g-1)
    c: Symmetric(g0,g0,g-2)
FEATURE [PartDesign::Pad] Pad021
  Direction = (1,1,1)
  Length = 6.3
  Length2 = 100
  Midplane = true
  Placement = pos=(0,0,0) rot=(0.57735,0.57735,0.57735;2.0944rad)
  Profile = -> Sketch036
  Suppressed = false
  Type = 0
FEATURE [PartDesign::Body] Body007  label="BodyDevice004"
  AllowCompound = false
  Group = -> [Sketch036,Pad021]
  Origin = -> Origin008
  Placement = pos=(0,29.75,0) rot=(0,0,1;0rad)
  Tip = -> Pad021
FEATURE [Sketcher::SketchObject] Sketch013  label="Sketch037"
  ArcFitTolerance = 0
  AttachmentSupport = -> [XY_Plane007]
  FullyConstrained = false
  MakeInternals = false
  MapMode = 5
  sketch-geometry (4):
    g0: LineSegment StartX=6 StartY=0.9 StartZ=0 EndX=1 EndY=0.9 EndZ=0
    g1: LineSegment StartX=1 StartY=0.9 StartZ=0 EndX=1 EndY=-0.9 EndZ=0
    g2: LineSegment StartX=1 StartY=-0.9 StartZ=0 EndX=6 EndY=-0.9 EndZ=0
    g3: LineSegment StartX=6 StartY=-0.9 StartZ=0 EndX=6 EndY=0.9 EndZ=0
  constraints (11):
    c: Coincident(g0,g1)
    c: Coincident(g1,g2)
    c: Coincident(g2,g3)
    c: Coincident(g3,g0)
    c: Horizontal(g0)
    c: Horizontal(g2)
    c: Vertical(g1)
    c: Symmetric(g0,g2,g-1)
    c: DistanceY(g3,g3) = 1.8
    c: DistanceX(g0) = 6
    c: DistanceX(g0) = 1
FEATURE [Sketcher::SketchObject] Sketch037  label="Sketch038"
  ArcFitTolerance = 0
  AttachmentSupport = -> [XZ_Plane008]
  FullyConstrained = false
  MakeInternals = false
  MapMode = 5
  Placement = pos=(0,0,0) rot=(1,0,0;1.5708rad)
  sketch-geometry (10):
    g0: LineSegment StartX=0 StartY=1.9 StartZ=0 EndX=3.2 EndY=1.9 EndZ=0
    g1: LineSegment StartX=3.2 StartY=1.4 StartZ=0 EndX=0 EndY=1.4 EndZ=0
    g2: LineSegment StartX=0 StartY=1.4 StartZ=0 EndX=0 EndY=1.9 EndZ=0
    g3: LineSegment StartX=4 StartY=0.5 StartZ=0 EndX=5.5 EndY=0.5 EndZ=0
    g4: LineSegment StartX=5.5 StartY=0.5 StartZ=0 EndX=5.5 EndY=0 EndZ=0
    g5: LineSegment StartX=5.5 StartY=0 StartZ=0 EndX=4 EndY=0 EndZ=0
    g6: LineSegment StartX=3.2 StartY=1.4 StartZ=0 EndX=3.5221 EndY=0.352981 EndZ=0
    g7: LineSegment StartX=4 StartY=0.5 StartZ=0 EndX=3.6779 EndY=1.54702 EndZ=0
    g8: ArcOfCircle CenterX=3.2 CenterY=1.4 CenterZ=0 NormalX=0 NormalY=0 NormalZ=1 AngleXU=0 Radius=0.5 StartAngle=0.29845 EndAngle=1.5708
    g9: ArcOfCircle CenterX=4 CenterY=0.5 CenterZ=0 NormalX=0 NormalY=0 NormalZ=1 AngleXU=0 Radius=0.5 StartAngle=3.44004 EndAngle=4.71239
  constraints (26):
    c: Coincident(g1,g2)
    c: Coincident(g2,g0)
    c: Horizontal(g0)
    c: Horizontal(g1)
    c: Vertical(g2)
    c: PointOnObject(g0,g-2)
    c: Coincident(g3,g4)
    c: Coincident(g4,g5)
    c: Horizontal(g3)
    c: Horizontal(g5)
    c: Vertical(g4)
    c: PointOnObject(g4,g-1)
    c: Tangent(g0,g8) = 1.5708
    c: Tangent(g7,g8) = -1.5708
    c: Tangent(g6,g9) = -1.5708
    c: Tangent(g5,g9) = 1.5708
    c: Coincident(g3,g7)
    c: Coincident(g3,g9)
    c: Coincident(g1,g6)
    c: Coincident(g1,g8)
    c: Parallel(g6,g7)
    c: DistanceX(g3) = 5.5
    c: DistanceY(g4,g4) = 0.5
    c: DistanceX(g1) = 3.2
    c: DistanceY(g1) = 1.4
    c: DistanceX(g1,g3) = 0.8
FEATURE [PartDesign::Pad] Pad020
  Direction = (1,1,1)
  Length = 4
  Length2 = 100
  Midplane = true
  Placement = pos=(0,0,0) rot=(1,0,0;1.5708rad)
  Profile = -> Sketch037
  Suppressed = false
  Type = 0
FEATURE [PartDesign::Mirrored] Mirrored007
  BaseFeature = -> Pad020
  MirrorPlane = -> YZ_Plane008
  Originals = -> [Pad020]
  Placement = pos=(0,0,0) rot=(1,0,0;1.5708rad)
  Suppressed = false
  TransformMode = 0
FEATURE [PartDesign::Pocket] Pocket006
  BaseFeature = -> Mirrored007
  Direction = (1,1,1)
  Length = 5
  Length2 = 100
  Midplane = true
  Placement = pos=(0,0,0) rot=(1,0,0;1.5708rad)
  Profile = -> Sketch013
  Suppressed = false
  Type = 1
FEATURE [PartDesign::Mirrored] Mirrored008
  BaseFeature = -> Pocket006
  MirrorPlane = -> YZ_Plane008
  Originals = -> [Pocket006]
  Placement = pos=(0,0,0) rot=(1,0,0;1.5708rad)
  Suppressed = false
  TransformMode = 0
FEATURE [PartDesign::Body] Body008  label="PinsDevice004"
  AllowCompound = false
  Group = -> [Sketch037,Pad020,Mirrored007,Sketch013,Pocket006,Mirrored008]
  Origin = -> Origin007
  Placement = pos=(0,29.75,0) rot=(0,0,1;0rad)
  Tip = -> Mirrored008
FEATURE [Sketcher::SketchObject] Sketch038  label="Sketch039"
  ArcFitTolerance = 0
  AttachmentSupport = -> [XY_Plane025]
  FullyConstrained = false
  MakeInternals = false
  MapMode = 5
  sketch-geometry (1):
    g0: Circle CenterX=11.45 CenterY=-11.09 CenterZ=0 NormalX=0 NormalY=0 NormalZ=1 AngleXU=0 Radius=0.5
  constraints (3):
    c: DistanceX(g-1,g0) = 11.45
    c: DistanceY(g0,g-1) = 11.09
    c: Diameter(g0) = 1
FEATURE [PartDesign::Pocket] Pocket007
  BaseFeature = -> Pad017
  Direction = (1,1,1)
  Length = 5
  Length2 = 100
  Midplane = true
  Profile = -> Sketch038
  Suppressed = false
  Type = 1
FEATURE [PartDesign::LinearPattern] LinearPattern002
  Direction = -> Y_Axis025
  Length = 20.32
  Mode = 0
  Occurrences = 9
  Offset = 2.54
  Suppressed = false
  TransformMode = 0
FEATURE [PartDesign::Mirrored] Mirrored009
  MirrorPlane = -> YZ_Plane025
  Suppressed = false
  TransformMode = 0
FEATURE [PartDesign::MultiTransform] MultiTransform001
  BaseFeature = -> Pocket007
  Originals = -> [Pocket007]
  Suppressed = false
  TransformMode = 0
  Transformations = -> [LinearPattern002,Mirrored009]
FEATURE [PartDesign::Body] Body020  label="PCB002"
  AllowCompound = false
  Group = -> [Sketch032,Pad017,Sketch038,Pocket007,MultiTransform001,LinearPattern002,Mirrored009]
  Origin = -> Origin025
  Placement = pos=(0,17.1,0) rot=(0,0,1;0rad)
  Tip = -> MultiTransform001
FEATURE [Part::Compound] Compound006  label="OpenThermAdaptor"
  Links = -> [Body020,Body021,Body022,Body007,Body008]
  Placement = pos=(4.4,-23.12,-25) rot=(0.57735,0.57735,-0.57735;2.0944rad)
FEATURE [App::Part] Part  label="Micro USB connector"
  Group = -> [Body015,Part__Feature001,Body016]
  Origin = -> Origin017
  Placement = pos=(-13.05,-13.35,2.5) rot=(1,0,0;3.14159rad)
FEATURE [Sketcher::SketchObject] Sketch027  label="wp edge trj"
  ArcFitTolerance = 0
  AttachmentSupport = -> [XZ_Plane018]
  FullyConstrained = true
  MakeInternals = false
  MapMode = 5
  Placement = pos=(0,0,0) rot=(1,0,0;1.5708rad)
  sketch-geometry (14):
    g0: ArcOfCircle CenterX=-6.23e-14 CenterY=-252.5 CenterZ=0 NormalX=0 NormalY=0 NormalZ=1 AngleXU=0 Radius=300 StartAngle=1.39005 EndAngle=1.75154
    g1: ArcOfCircle CenterX=3.11e-14 CenterY=252.5 CenterZ=0 NormalX=0 NormalY=0 NormalZ=1 AngleXU=0 Radius=300 StartAngle=4.53164 EndAngle=4.89314
    g2: LineSegment [constr] StartX=0 StartY=47.5 StartZ=0 EndX=0 EndY=-47.5 EndZ=0
    g3: ArcOfCircle CenterX=70 CenterY=0 CenterZ=0 NormalX=0 NormalY=0 NormalZ=1 AngleXU=0 Radius=140 StartAngle=2.92314 EndAngle=3.36005
    g4: ArcOfCircle CenterX=-70 CenterY=0 CenterZ=0 NormalX=0 NormalY=0 NormalZ=1 AngleXU=0 Radius=140 StartAngle=6.06473 EndAngle=6.50164
    g5: ArcOfCircle CenterX=51.0529 CenterY=26.8736 CenterZ=0 NormalX=0 NormalY=0 NormalZ=1 AngleXU=0 Radius=16 StartAngle=0.218456 EndAngle=1.39005
    g6: ArcOfCircle CenterX=-51.0529 CenterY=26.8736 CenterZ=0 NormalX=0 NormalY=0 NormalZ=1 AngleXU=0 Radius=16 StartAngle=1.75154 EndAngle=2.92314
    g7: ArcOfCircle CenterX=51.0529 CenterY=-26.8736 CenterZ=0 NormalX=0 NormalY=0 NormalZ=1 AngleXU=0 Radius=16 StartAngle=4.89314 EndAngle=6.06473
    g8: ArcOfCircle CenterX=-51.0529 CenterY=-26.8736 CenterZ=0 NormalX=0 NormalY=0 NormalZ=1 AngleXU=0 Radius=16 StartAngle=3.36005 EndAngle=4.53164
    g9: LineSegment [constr] StartX=-51.0529 StartY=26.8736 StartZ=0 EndX=51.0529 EndY=26.8736 EndZ=0
    g10: LineSegment [constr] StartX=51.0529 StartY=26.8736 StartZ=0 EndX=51.0529 EndY=-26.8736 EndZ=0
    g11: LineSegment [constr] StartX=51.0529 StartY=-26.8736 StartZ=0 EndX=-51.0529 EndY=-26.8736 EndZ=0
    g12: LineSegment [constr] StartX=-51.0529 StartY=-26.8736 StartZ=0 EndX=-51.0529 EndY=26.8736 EndZ=0
    g13: LineSegment [constr] StartX=-70 StartY=0 StartZ=0 EndX=70 EndY=0 EndZ=0
  constraints (36):
    c: PointOnObject(g2,g0)
    c: PointOnObject(g2,g1)
    c: DistanceY(g2,g2) = 95
    c: Equal(g4,g3)
    c: Equal(g0,g1)
    c: Tangent(g0,g5) = -1.5708
    c: Tangent(g4,g5) = -1.5708
    c: Tangent(g4,g7) = -1.5708
    c: Tangent(g1,g7) = -1.5708
    c: Tangent(g8,g1) = -1.5708
    c: Tangent(g3,g8) = -1.5708
    c: Tangent(g3,g6) = -1.5708
    c: Tangent(g0,g6) = -1.5708
    c: Equal(g6,g5)
    c: Equal(g5,g7)
    c: Equal(g7,g8)
    c: Radius(g5) = 16
    c: Coincident(g9,g10)
    c: Coincident(g10,g11)
    c: Coincident(g11,g12)
    c: Coincident(g12,g9)
    c: Horizontal(g9)
    c: Horizontal(g11)
    c: Coincident(g9,g6)
    c: Coincident(g10,g7)
    c: Coincident(g5,g9)
    c: Coincident(g8,g11)
    c: Radius(g4) = 140
    c: Radius(g0) = 300
    c: Coincident(g13,g4)
    c: Coincident(g13,g3)
    c: PointOnObject(g3,g4)
    c: DistanceY(g3,g-1) = 0
    c: Symmetric(g2,g2,g13)
    c: PointOnObject(g-1,g2)
    c: Symmetric(g5,g6,g2)
FEATURE [Sketcher::SketchObject] Sketch028  label="wp base shape"
  ArcFitTolerance = 0
  AttachmentSupport = -> [XY_Plane018]
  FullyConstrained = true
  MakeInternals = false
  MapMode = 5
  sketch-geometry (6):
    g0: LineSegment StartX=-34 StartY=-29.5 StartZ=0 EndX=34 EndY=-29.5 EndZ=0
    g1: ArcOfCircle CenterX=34 CenterY=21.2813 CenterZ=0 NormalX=0 NormalY=0 NormalZ=1 AngleXU=0 Radius=50.7813 StartAngle=4.71239 EndAngle=5.52869
    g2: ArcOfCircle CenterX=-34 CenterY=21.2813 CenterZ=0 NormalX=0 NormalY=0 NormalZ=1 AngleXU=0 Radius=50.7813 StartAngle=3.89609 EndAngle=4.71239
    g3: LineSegment StartX=-71 StartY=0 StartZ=0 EndX=71 EndY=0 EndZ=0
    g4: LineSegment StartX=71 StartY=0 StartZ=0 EndX=71 EndY=-13.5 EndZ=0
    g5: LineSegment StartX=-71 StartY=-13.5 StartZ=0 EndX=-71 EndY=0 EndZ=0
  constraints (16):
    c: Tangent(g0,g2) = -1.5708
    c: Tangent(g0,g1) = -1.5708
    c: DistanceY(g0,g-1) = 29.5
    c: Coincident(g3,g4)
    c: Coincident(g5,g3)
    c: Horizontal(g3)
    c: Vertical(g4)
    c: Vertical(g5)
    c: PointOnObject(g3,g-1)
    c: Coincident(g4,g1)
    c: Coincident(g2,g5)
    c: Symmetric(g1,g2,g-2)
    c: DistanceX(g0,g0) = 68
    c: Symmetric(g1,g2,g-2)
    c: DistanceX(g3,g3) = 142
    c: DistanceY(g0,g1) = 16
FEATURE [PartDesign::Pad] Pad016  label="WP Base shape"
  Direction = (1,1,1)
  Length = 100
  Length2 = 60
  Midplane = true
  Profile = -> Sketch028
  Suppressed = false
  Type = 0
FEATURE [Sketcher::SketchObject] Sketch029  label="wp edge crs"
  ArcFitTolerance = 0
  AttachmentSupport = -> [YZ_Plane018]
  FullyConstrained = true
  MakeInternals = false
  MapMode = 5
  Placement = pos=(0,0,0) rot=(0.57735,0.57735,0.57735;2.0944rad)
  sketch-geometry (6):
    g0: LineSegment StartX=0 StartY=70 StartZ=0 EndX=-30 EndY=70 EndZ=0
    g1: LineSegment StartX=-30 StartY=70 StartZ=0 EndX=-30 EndY=42.0299 EndZ=0
    g2: LineSegment StartX=0 StartY=43 StartZ=0 EndX=0 EndY=70 EndZ=0
    g3: ArcOfCircle CenterX=0 CenterY=-37.5 CenterZ=0 NormalX=0 NormalY=0 NormalZ=1 AngleXU=0 Radius=85 StartAngle=1.64277 EndAngle=1.93151
    g4: LineSegment StartX=-6.11239 StartY=47.2799 StartZ=0 EndX=0 EndY=43 EndZ=0
    g5: ArcOfCircle [constr] CenterX=0 CenterY=-37.5 CenterZ=0 NormalX=0 NormalY=0 NormalZ=1 AngleXU=0 Radius=85 StartAngle=1.5708 EndAngle=1.64277
  constraints (19):
    c: Coincident(g0,g1)
    c: Coincident(g2,g0)
    c: Horizontal(g0)
    c: Vertical(g1)
    c: Vertical(g2)
    c: PointOnObject(g0,g-2)
    c: Coincident(g3,g1)
    c: DistanceX(g1,g-1) = 30
    c: PointOnObject(g3,g-2)
    c: DistanceY(g0) = 70
    c: Radius(g3) = 85
    c: Coincident(g4,g3)
    c: Coincident(g5,g3)
    c: Coincident(g5,g3)
    c: PointOnObject(g5,g-2)
    c: DistanceY(g5) = 47.5
    c: Coincident(g2,g4)
    c: Angle(g2,g4) = 0.959931
    c: DistanceY(g2,g5) = 4.5
FEATURE [PartDesign::SubtractivePipe] SubtractivePipe  label="WP Edge"
  AuxilleryCurvelinear = true
  AuxillerySpineTangent = false
  BaseFeature = -> Pad016
  Binormal = (0,0,0)
  Mode = 0
  Profile = -> Sketch029
  Spine = -> Sketch027
  SpineTangent = false
  Suppressed = false
  Transformation = 0
  Transition = 0
FEATURE [PartDesign::Fillet] Fillet  label="WP Base fillet"
  Base = -> SubtractivePipe [Edge10]
  BaseFeature = -> SubtractivePipe
  Radius = 8
  SupportTransform = false
  Suppressed = false
  UseAllEdges = false
FEATURE [Part::FeaturePython] Screw003  label="M8x25-Screw"  # Fasteners workbench fastener (typed FeaturePython)
  Placement = pos=(50,-3,-1e-15) rot=(1,0,0;1.5708rad)
  diameter = 9
  invert = false
  length = 5
  lengthCustom = 25
  matchOuter = false
  offset = 0
  thread = false
  type = 19
FEATURE [Part::FeaturePython] Screw004  label="M8x25-Screw001"  # Fasteners workbench fastener (typed FeaturePython)
  Placement = pos=(-50,-3,-1e-15) rot=(1,0,0;1.5708rad)
  diameter = 9
  invert = false
  length = 5
  lengthCustom = 25
  matchOuter = false
  offset = 0
  thread = false
  type = 19
FEATURE [PartDesign::Plane] DatumPlane  label="wp sensor mirror plane"
  AttachmentOffset = pos=(0,0,-1) rot=(0,0,1;0rad)
  AttachmentSupport = -> [XY_Plane018]
  Length = 60
  MapMode = 5
  Placement = pos=(0,0,-1) rot=(0,0,1;0rad)
  ResizeMode = 0
  Width = 60
FEATURE [Sketcher::SketchObject] Sketch067  label="Sketch"
  ArcFitTolerance = 0
  AttachmentSupport = -> [XZ_Plane042]
  FullyConstrained = false
  MakeInternals = false
  MapMode = 5
  Placement = pos=(0,0,0) rot=(1,0,0;1.5708rad)
  sketch-geometry (5):
    g0: LineSegment StartX=3.2 StartY=2.75 StartZ=0 EndX=5 EndY=2.75 EndZ=0
    g1: LineSegment StartX=5 StartY=2.75 StartZ=0 EndX=5 EndY=0 EndZ=0
    g2: LineSegment StartX=5 StartY=0 StartZ=0 EndX=1.5 EndY=0 EndZ=0
    g3: LineSegment StartX=1.5 StartY=0 StartZ=0 EndX=1.5 EndY=1.05 EndZ=0
    g4: LineSegment StartX=3.2 StartY=2.75 StartZ=0 EndX=1.5 EndY=1.05 EndZ=0
  constraints (15):
    c: Coincident(g0,g1)
    c: Coincident(g1,g2)
    c: Coincident(g2,g3)
    c: Horizontal(g0)
    c: Horizontal(g2)
    c: Vertical(g1)
    c: Vertical(g3)
    c: PointOnObject(g1,g-1)
    c: DistanceX(g1) = 5
    c: Coincident(g0,g4)
    c: Coincident(g4,g3)
    c: DistanceY(g0) = 2.75
    c: DistanceX(g2) = 1.5
    c: Angle(g3,g4) = 2.35619
    c: DistanceX(g0) = 3.2
FEATURE [PartDesign::Revolution] Revolution001  label="Revolution"
  Angle = 360
  Angle2 = 60
  Axis = (-3e-16,3e-16,1)
  Base = (0,0,0)
  Placement = pos=(0,0,0) rot=(1,0,0;1.5708rad)
  Profile = -> Sketch067
  ReferenceAxis = -> Z_Axis042
  Reversed = true
  Suppressed = false
  Type = 0
FEATURE [PartDesign::Body] Body037  label="RingMagnet10x2.75_1"
  AllowCompound = false
  Group = -> [Sketch067,Revolution001]
  Origin = -> Origin042
  Placement = pos=(-56,-6.75,22) rot=(1,0,0;1.5708rad)
  Tip = -> Revolution001
FEATURE [Sketcher::SketchObject] Sketch068  label="wp magnet pocket"
  ArcFitTolerance = 0
  AttachmentOffset = pos=(0,0,-56) rot=(0,0,1;0rad)
  AttachmentSupport = -> [YZ_Plane018]
  FullyConstrained = true
  MakeInternals = false
  MapMode = 5
  Placement = pos=(-56,0,0) rot=(0.57735,0.57735,0.57735;2.0944rad)
  sketch-geometry (5):
    g0: LineSegment StartX=-9.6 StartY=27.15 StartZ=0 EndX=-3.8 EndY=27.15 EndZ=0
    g1: LineSegment StartX=-3.8 StartY=27.15 StartZ=0 EndX=-3.8 EndY=22 EndZ=0
    g2: LineSegment StartX=-3.8 StartY=22 StartZ=0 EndX=-9.6 EndY=22 EndZ=0
    g3: LineSegment StartX=-9.6 StartY=22 StartZ=0 EndX=-9.6 EndY=27.15 EndZ=0
    g4: LineSegment [constr] StartX=-3.8 StartY=22 StartZ=0 EndX=1.35 EndY=22 EndZ=0
  constraints (15):
    c: Coincident(g0,g1)
    c: Coincident(g1,g2)
    c: Coincident(g2,g3)
    c: Coincident(g3,g0)
    c: Horizontal(g0)
    c: Horizontal(g2)
    c: Vertical(g1)
    c: Vertical(g3)
    c: Coincident(g4,g1)
    c: Horizontal(g4)
    c: DistanceY(g2) = 22
    c: DistanceY(g3,g3) = 5.15
    c: Equal(g4,g1)
    c: DistanceX(g0,g-1) = 9.6
    c: DistanceX(g0,g0) = 5.8
FEATURE [PartDesign::Mirrored] Mirrored011
  MirrorPlane = -> DatumPlane
  Suppressed = false
  TransformMode = 0
FEATURE [PartDesign::Mirrored] Mirrored012
  MirrorPlane = -> YZ_Plane018
  Suppressed = false
  TransformMode = 0
FEATURE [Sketcher::SketchObject] Sketch069  label="wp separation top bottom"
  ArcFitTolerance = 0
  AttachmentSupport = -> [YZ_Plane018]
  FullyConstrained = true
  MakeInternals = false
  MapMode = 5
  Placement = pos=(0,0,0) rot=(0.57735,0.57735,0.57735;2.0944rad)
  sketch-geometry (4):
    g0: LineSegment StartX=-9 StartY=60 StartZ=0 EndX=-59 EndY=60 EndZ=0
    g1: LineSegment StartX=-59 StartY=60 StartZ=0 EndX=-59 EndY=-60 EndZ=0
    g2: LineSegment StartX=-59 StartY=-60 StartZ=0 EndX=-9 EndY=-60 EndZ=0
    g3: LineSegment StartX=-9 StartY=-60 StartZ=0 EndX=-9 EndY=60 EndZ=0
  constraints (11):
    c: Coincident(g0,g1)
    c: Coincident(g1,g2)
    c: Coincident(g2,g3)
    c: Coincident(g3,g0)
    c: Horizontal(g0)
    c: Horizontal(g2)
    c: Vertical(g1)
    c: DistanceX(g0,g-1) = 9
    c: DistanceX(g0,g0) = 50
    c: Symmetric(g0,g2,g-1)
    c: DistanceY(g3,g3) = 120
FEATURE [PartDesign::Pocket] Pocket009  label="WP Separation top bottom"
  BaseFeature = -> Fillet
  Direction = (1,1,1)
  Length = 5
  Length2 = 100
  Midplane = true
  Profile = -> Sketch069
  Suppressed = false
  Type = 1
FEATURE [Sketcher::SketchObject] Sketch070  label="fp base shape"
  ArcFitTolerance = 0
  AttachmentSupport = -> [XY_Plane043]
  FullyConstrained = true
  MakeInternals = false
  MapMode = 5
  sketch-geometry (6):
    g0: LineSegment StartX=-34 StartY=-29.5 StartZ=0 EndX=34 EndY=-29.5 EndZ=0
    g1: ArcOfCircle CenterX=34 CenterY=21.2813 CenterZ=0 NormalX=0 NormalY=0 NormalZ=1 AngleXU=0 Radius=50.7813 StartAngle=4.71239 EndAngle=5.52869
    g2: ArcOfCircle CenterX=-34 CenterY=21.2813 CenterZ=0 NormalX=0 NormalY=0 NormalZ=1 AngleXU=0 Radius=50.7813 StartAngle=3.89609 EndAngle=4.71239
    g3: LineSegment StartX=-71 StartY=0 StartZ=0 EndX=71 EndY=0 EndZ=0
    g4: LineSegment StartX=71 StartY=0 StartZ=0 EndX=71 EndY=-13.5 EndZ=0
    g5: LineSegment StartX=-71 StartY=-13.5 StartZ=0 EndX=-71 EndY=0 EndZ=0
  constraints (16):
    c: Tangent(g0,g2) = -1.5708
    c: Tangent(g0,g1) = -1.5708
    c: DistanceY(g0,g-1) = 29.5
    c: Coincident(g3,g4)
    c: Coincident(g5,g3)
    c: Horizontal(g3)
    c: Vertical(g4)
    c: Vertical(g5)
    c: PointOnObject(g3,g-1)
    c: Coincident(g4,g1)
    c: Coincident(g2,g5)
    c: Symmetric(g1,g2,g-2)
    c: DistanceX(g0,g0) = 68
    c: Symmetric(g1,g2,g-2)
    c: DistanceX(g3,g3) = 142
    c: DistanceY(g0,g1) = 16
FEATURE [Sketcher::SketchObject] Sketch071  label="fp edge trj"
  ArcFitTolerance = 0
  AttachmentSupport = -> [XZ_Plane043]
  FullyConstrained = true
  MakeInternals = false
  MapMode = 5
  Placement = pos=(0,0,0) rot=(1,0,0;1.5708rad)
  sketch-geometry (14):
    g0: ArcOfCircle CenterX=-2.3e-15 CenterY=-252.5 CenterZ=0 NormalX=0 NormalY=0 NormalZ=1 AngleXU=0 Radius=300 StartAngle=1.39005 EndAngle=1.75154
    g1: ArcOfCircle CenterX=5.98e-14 CenterY=252.5 CenterZ=0 NormalX=0 NormalY=0 NormalZ=1 AngleXU=0 Radius=300 StartAngle=4.53164 EndAngle=4.89314
    g2: LineSegment [constr] StartX=0 StartY=47.5 StartZ=0 EndX=0 EndY=-47.5 EndZ=0
    g3: ArcOfCircle CenterX=70 CenterY=0 CenterZ=0 NormalX=0 NormalY=0 NormalZ=1 AngleXU=0 Radius=140 StartAngle=2.92314 EndAngle=3.36005
    g4: ArcOfCircle CenterX=-70 CenterY=0 CenterZ=0 NormalX=0 NormalY=0 NormalZ=1 AngleXU=0 Radius=140 StartAngle=6.06473 EndAngle=6.50164
    g5: ArcOfCircle CenterX=51.0529 CenterY=26.8736 CenterZ=0 NormalX=0 NormalY=0 NormalZ=1 AngleXU=0 Radius=16 StartAngle=0.218456 EndAngle=1.39005
    g6: ArcOfCircle CenterX=-51.0529 CenterY=26.8736 CenterZ=0 NormalX=0 NormalY=0 NormalZ=1 AngleXU=0 Radius=16 StartAngle=1.75154 EndAngle=2.92314
    g7: ArcOfCircle CenterX=51.0529 CenterY=-26.8736 CenterZ=0 NormalX=0 NormalY=0 NormalZ=1 AngleXU=0 Radius=16 StartAngle=4.89314 EndAngle=6.06473
    g8: ArcOfCircle CenterX=-51.0529 CenterY=-26.8736 CenterZ=0 NormalX=0 NormalY=0 NormalZ=1 AngleXU=0 Radius=16 StartAngle=3.36005 EndAngle=4.53164
    g9: LineSegment [constr] StartX=-51.0529 StartY=26.8736 StartZ=0 EndX=51.0529 EndY=26.8736 EndZ=0
    g10: LineSegment [constr] StartX=51.0529 StartY=26.8736 StartZ=0 EndX=51.0529 EndY=-26.8736 EndZ=0
    g11: LineSegment [constr] StartX=51.0529 StartY=-26.8736 StartZ=0 EndX=-51.0529 EndY=-26.8736 EndZ=0
    g12: LineSegment [constr] StartX=-51.0529 StartY=-26.8736 StartZ=0 EndX=-51.0529 EndY=26.8736 EndZ=0
    g13: LineSegment [constr] StartX=-70 StartY=0 StartZ=0 EndX=70 EndY=0 EndZ=0
  constraints (36):
    c: PointOnObject(g2,g0)
    c: PointOnObject(g2,g1)
    c: DistanceY(g2,g2) = 95
    c: Equal(g4,g3)
    c: Equal(g0,g1)
    c: Tangent(g0,g5) = -1.5708
    c: Tangent(g4,g5) = -1.5708
    c: Tangent(g4,g7) = -1.5708
    c: Tangent(g1,g7) = -1.5708
    c: Tangent(g8,g1) = -1.5708
    c: Tangent(g3,g8) = -1.5708
    c: Tangent(g3,g6) = -1.5708
    c: Tangent(g0,g6) = -1.5708
    c: Equal(g6,g5)
    c: Equal(g5,g7)
    c: Equal(g7,g8)
    c: Radius(g5) = 16
    c: Coincident(g9,g10)
    c: Coincident(g10,g11)
    c: Coincident(g11,g12)
    c: Coincident(g12,g9)
    c: Horizontal(g9)
    c: Horizontal(g11)
    c: Coincident(g9,g6)
    c: Coincident(g10,g7)
    c: Coincident(g5,g9)
    c: Coincident(g8,g11)
    c: Radius(g4) = 140
    c: Radius(g0) = 300
    c: Coincident(g13,g4)
    c: Coincident(g13,g3)
    c: PointOnObject(g3,g4)
    c: DistanceY(g3,g-1) = 0
    c: Symmetric(g2,g2,g13)
    c: PointOnObject(g-1,g2)
    c: Symmetric(g5,g6,g2)
FEATURE [Sketcher::SketchObject] Sketch072  label="fp edge crs"
  ArcFitTolerance = 0
  AttachmentSupport = -> [YZ_Plane043]
  FullyConstrained = true
  MakeInternals = false
  MapMode = 5
  Placement = pos=(0,0,0) rot=(0.57735,0.57735,0.57735;2.0944rad)
  sketch-geometry (4):
    g0: LineSegment StartX=5.2e-15 StartY=70 StartZ=0 EndX=-30 EndY=70 EndZ=0
    g1: LineSegment StartX=-30 StartY=70 StartZ=0 EndX=-30 EndY=42.0299 EndZ=0
    g2: LineSegment StartX=5.2e-15 StartY=47.5 StartZ=0 EndX=5.2e-15 EndY=70 EndZ=0
    g3: ArcOfCircle CenterX=0 CenterY=-37.5 CenterZ=0 NormalX=0 NormalY=0 NormalZ=1 AngleXU=0 Radius=85 StartAngle=1.5708 EndAngle=1.93151
  constraints (13):
    c: Coincident(g0,g1)
    c: Coincident(g2,g0)
    c: Horizontal(g0)
    c: Vertical(g1)
    c: Vertical(g2)
    c: PointOnObject(g0,g-2)
    c: Coincident(g3,g1)
    c: Coincident(g2,g3)
    c: DistanceY(g2) = 47.5
    c: DistanceX(g1,g-1) = 30
    c: PointOnObject(g3,g-2)
    c: DistanceY(g0) = 70
    c: Radius(g3) = 85
FEATURE [Sketcher::SketchObject] Sketch073  label="fp cable cavity"
  ArcFitTolerance = 0
  AttachmentOffset = pos=(0,0,25) rot=(0,0,1;0rad)
  AttachmentSupport = -> [XZ_Plane043]
  FullyConstrained = true
  MakeInternals = false
  MapMode = 5
  Placement = pos=(0,-25,5.6e-15) rot=(1,0,0;1.5708rad)
  sketch-geometry (13):
    g0: ArcOfCircle CenterX=3.7e-15 CenterY=-102 CenterZ=0 NormalX=0 NormalY=0 NormalZ=1 AngleXU=0 Radius=140 StartAngle=1.3467 EndAngle=1.79489
    g1: LineSegment StartX=35 StartY=29.6245 StartZ=0 EndX=35 EndY=-2 EndZ=0
    g2: LineSegment StartX=30 StartY=-7 StartZ=0 EndX=-30 EndY=-7 EndZ=0
    g3: LineSegment StartX=-35 StartY=-2 StartZ=0 EndX=-35 EndY=29.6245 EndZ=0
    g4: GeomPoint [constr] X=0 Y=38 Z=0
    g5: ArcOfCircle CenterX=-30 CenterY=29.6245 CenterZ=0 NormalX=0 NormalY=0 NormalZ=1 AngleXU=0 Radius=5 StartAngle=1.79489 EndAngle=3.14159
    g6: ArcOfCircle CenterX=-30 CenterY=-2 CenterZ=0 NormalX=0 NormalY=0 NormalZ=1 AngleXU=0 Radius=5 StartAngle=3.14159 EndAngle=4.71239
    g7: ArcOfCircle CenterX=30 CenterY=-2 CenterZ=0 NormalX=0 NormalY=0 NormalZ=1 AngleXU=0 Radius=5 StartAngle=4.71239 EndAngle=6.28319
    g8: ArcOfCircle CenterX=30 CenterY=29.6245 CenterZ=0 NormalX=0 NormalY=0 NormalZ=1 AngleXU=0 Radius=5 StartAngle=0 EndAngle=1.3467
    g9: LineSegment [constr] StartX=30 StartY=29.6245 StartZ=0 EndX=-30 EndY=29.6245 EndZ=0
    g10: LineSegment [constr] StartX=-30 StartY=29.6245 StartZ=0 EndX=-30 EndY=-2 EndZ=0
    g11: LineSegment [constr] StartX=-30 StartY=-2 StartZ=0 EndX=30 EndY=-2 EndZ=0
    g12: LineSegment [constr] StartX=30 StartY=-2 StartZ=0 EndX=30 EndY=29.6245 EndZ=0
  constraints (30):
    c: Horizontal(g2)
    c: Vertical(g1)
    c: Vertical(g3)
    c: PointOnObject(g4,g0)
    c: PointOnObject(g4,g-2)
    c: DistanceY(g4) = 38
    c: Radius(g0) = 140
    c: Tangent(g0,g5) = -1.5708
    c: Tangent(g3,g5) = 1.5708
    c: Tangent(g2,g6) = 1.5708
    c: Tangent(g3,g6) = 1.5708
    c: Tangent(g2,g7) = 1.5708
    c: Tangent(g1,g7) = 1.5708
    c: Tangent(g1,g8) = 1.5708
    c: Tangent(g0,g8) = -1.5708
    c: Coincident(g9,g10)
    c: Coincident(g10,g11)
    c: Coincident(g11,g12)
    c: Coincident(g12,g9)
    c: Horizontal(g11)
    c: Vertical(g10)
    c: Vertical(g12)
    c: Coincident(g9,g8)
    c: Coincident(g10,g6)
    c: Coincident(g5,g9)
    c: Symmetric(g5,g8,g-2)
    c: Coincident(g7,g11)
    c: DistanceX(g3,g1) = 70
    c: DistanceY(g2,g-1) = 7
    c: Radius(g7) = 5
FEATURE [Sketcher::SketchObject] Sketch077  label="fp magnet pocket"
  ArcFitTolerance = 0
  AttachmentOffset = pos=(0,0,-56) rot=(0,0,1;0rad)
  AttachmentSupport = -> [YZ_Plane043]
  FullyConstrained = true
  MakeInternals = false
  MapMode = 5
  Placement = pos=(-56,0,0) rot=(0.57735,0.57735,0.57735;2.0944rad)
  sketch-geometry (5):
    g0: LineSegment StartX=-16.4 StartY=27.15 StartZ=0 EndX=-10.4 EndY=27.15 EndZ=0
    g1: LineSegment StartX=-10.4 StartY=27.15 StartZ=0 EndX=-10.4 EndY=22 EndZ=0
    g2: LineSegment StartX=-10.4 StartY=22 StartZ=0 EndX=-16.4 EndY=22 EndZ=0
    g3: LineSegment StartX=-16.4 StartY=22 StartZ=0 EndX=-16.4 EndY=27.15 EndZ=0
    g4: LineSegment [constr] StartX=-10.4 StartY=22 StartZ=0 EndX=-5.25 EndY=22 EndZ=0
  constraints (15):
    c: Coincident(g0,g1)
    c: Coincident(g1,g2)
    c: Coincident(g2,g3)
    c: Coincident(g3,g0)
    c: Horizontal(g0)
    c: Horizontal(g2)
    c: Vertical(g1)
    c: Vertical(g3)
    c: Coincident(g4,g1)
    c: Horizontal(g4)
    c: DistanceY(g2) = 22
    c: DistanceY(g3,g3) = 5.15
    c: Equal(g4,g1)
    c: DistanceX(g1,g-1) = 10.4
    c: DistanceX(g0,g0) = 6
FEATURE [PartDesign::Mirrored] Mirrored014
  MirrorPlane = -> YZ_Plane043
  Suppressed = false
  TransformMode = 0
FEATURE [PartDesign::Plane] DatumPlane001  label="fp sensor mirror plane"
  AttachmentOffset = pos=(0,0,-1) rot=(0,0,1;0rad)
  AttachmentSupport = -> [XY_Plane043]
  Length = 60
  MapMode = 5
  Placement = pos=(0,0,-1) rot=(0,0,1;0rad)
  ResizeMode = 0
  Width = 60
FEATURE [PartDesign::Mirrored] Mirrored016
  MirrorPlane = -> DatumPlane001
  Suppressed = false
  TransformMode = 0
FEATURE [Sketcher::SketchObject] Sketch078  label="fp separation top bottom"
  ArcFitTolerance = 0
  AttachmentSupport = -> [YZ_Plane043]
  FullyConstrained = true
  MakeInternals = false
  MapMode = 5
  Placement = pos=(0,0,0) rot=(0.57735,0.57735,0.57735;2.0944rad)
  sketch-geometry (4):
    g0: LineSegment StartX=-10 StartY=60 StartZ=0 EndX=40 EndY=60 EndZ=0
    g1: LineSegment StartX=40 StartY=60 StartZ=0 EndX=40 EndY=-60 EndZ=0
    g2: LineSegment StartX=40 StartY=-60 StartZ=0 EndX=-10 EndY=-60 EndZ=0
    g3: LineSegment StartX=-10 StartY=-60 StartZ=0 EndX=-10 EndY=60 EndZ=0
  constraints (11):
    c: Coincident(g0,g1)
    c: Coincident(g1,g2)
    c: Coincident(g2,g3)
    c: Coincident(g3,g0)
    c: Horizontal(g0)
    c: Horizontal(g2)
    c: Vertical(g1)
    c: DistanceX(g0,g-1) = 10
    c: DistanceX(g0,g0) = -50
    c: Symmetric(g0,g2,g-1)
    c: DistanceY(g3,g3) = 120
FEATURE [PartDesign::Pad] Pad025  label="FP Base shape"
  Direction = (1,1,1)
  Length = 100
  Length2 = 60
  Midplane = true
  Profile = -> Sketch070
  Suppressed = false
  Type = 0
FEATURE [PartDesign::SubtractivePipe] SubtractivePipe001  label="FP Edge"
  AuxilleryCurvelinear = true
  AuxillerySpineTangent = false
  BaseFeature = -> Pad025
  Binormal = (0,0,0)
  Mode = 0
  Profile = -> Sketch072
  Spine = -> Sketch071
  SpineTangent = false
  Suppressed = false
  Transformation = 0
  Transition = 0
FEATURE [PartDesign::Fillet] Fillet002  label="FP Base fillet"
  Base = -> SubtractivePipe001 [Edge10]
  BaseFeature = -> SubtractivePipe001
  Radius = 8
  SupportTransform = false
  Suppressed = false
  UseAllEdges = false
FEATURE [PartDesign::Groove] Groove003  label="FP Magnet pocket"
  Angle = 360
  Angle2 = 60
  Axis = (1.7e-15,5.15,-1.1e-15)
  Base = (-56,-10.4,22)
  BaseFeature = -> Fillet002
  Profile = -> Sketch077
  ReferenceAxis = -> Sketch077 [Axis]
  Reversed = true
  Suppressed = false
  Type = 0
FEATURE [PartDesign::MultiTransform] MultiTransform003  label="FP Other magnet pockets"
  BaseFeature = -> Groove003
  Originals = -> [Groove003]
  Suppressed = false
  TransformMode = 0
  Transformations = -> [Mirrored016,Mirrored014]
FEATURE [PartDesign::Pocket] Pocket011  label="FP Cable cavity"
  BaseFeature = -> MultiTransform003
  Direction = (0,1,2e-16)
  Length = 5
  Length2 = 100
  Profile = -> Sketch073
  Suppressed = false
  Type = 1
FEATURE [PartDesign::Pocket] Pocket010  label="FP Separation top bottom"
  BaseFeature = -> Pocket011
  Direction = (-1,2e-16,-3e-16)
  Length = 5
  Length2 = 100
  Midplane = true
  Profile = -> Sketch078
  Suppressed = false
  Type = 1
FEATURE [Sketcher::SketchObject] Sketch079  label="fp screen visible hole"
  ArcFitTolerance = 0
  AttachmentSupport = -> [XZ_Plane043]
  FullyConstrained = true
  MakeInternals = false
  MapMode = 5
  Placement = pos=(0,0,0) rot=(1,0,0;1.5708rad)
  sketch-geometry (13):
    g0: LineSegment [constr] StartX=-24.35 StartY=28.05 StartZ=0 EndX=24.35 EndY=28.05 EndZ=0
    g1: LineSegment [constr] StartX=24.35 StartY=28.05 StartZ=0 EndX=24.35 EndY=-8.05 EndZ=0
    g2: LineSegment [constr] StartX=24.35 StartY=-8.05 StartZ=0 EndX=-24.35 EndY=-8.05 EndZ=0
    g3: LineSegment [constr] StartX=-24.35 StartY=-8.05 StartZ=0 EndX=-24.35 EndY=28.05 EndZ=0
    g4: LineSegment StartX=-24.35 StartY=28.85 StartZ=0 EndX=24.35 EndY=28.85 EndZ=0
    g5: LineSegment StartX=25.15 StartY=28.05 StartZ=0 EndX=25.15 EndY=-8.05 EndZ=0
    g6: LineSegment StartX=24.35 StartY=-8.85 StartZ=0 EndX=-24.35 EndY=-8.85 EndZ=0
    g7: LineSegment StartX=-25.15 StartY=-8.05 StartZ=0 EndX=-25.15 EndY=28.05 EndZ=0
    g8: ArcOfCircle CenterX=24.35 CenterY=28.05 CenterZ=0 NormalX=0 NormalY=0 NormalZ=1 AngleXU=0 Radius=0.8 StartAngle=4.911e-12 EndAngle=1.5708
    g9: ArcOfCircle CenterX=-24.35 CenterY=28.05 CenterZ=0 NormalX=0 NormalY=0 NormalZ=1 AngleXU=0 Radius=0.8 StartAngle=1.5708 EndAngle=3.14159
    g10: ArcOfCircle CenterX=-24.35 CenterY=-8.05 CenterZ=0 NormalX=0 NormalY=0 NormalZ=1 AngleXU=0 Radius=0.8 StartAngle=3.14159 EndAngle=4.71239
    g11: ArcOfCircle CenterX=24.35 CenterY=-8.05 CenterZ=0 NormalX=0 NormalY=0 NormalZ=1 AngleXU=0 Radius=0.8 StartAngle=4.71239 EndAngle=6.28319
    g12: LineSegment [constr] StartX=-24.35 StartY=10 StartZ=0 EndX=24.35 EndY=10 EndZ=0
  constraints (30):
    c: Coincident(g0,g1)
    c: Coincident(g1,g2)
    c: Coincident(g2,g3)
    c: Coincident(g3,g0)
    c: Horizontal(g2)
    c: Vertical(g1)
    c: Vertical(g3)
    c: Horizontal(g4)
    c: Horizontal(g6)
    c: Vertical(g5)
    c: Tangent(g4,g8) = 1.5708
    c: Tangent(g5,g8) = 1.5708
    c: Tangent(g4,g9) = 1.5708
    c: Tangent(g7,g9) = 1.5708
    c: Tangent(g6,g10) = 1.5708
    c: Tangent(g7,g10) = 1.5708
    c: Tangent(g5,g11) = 1.5708
    c: Tangent(g6,g11) = 1.5708
    c: Coincident(g1,g11)
    c: Coincident(g0,g8)
    c: Coincident(g0,g9)
    c: Coincident(g2,g10)
    c: Symmetric(g8,g9,g-2)
    c: DistanceX(g7,g5) = 50.3
    c: DistanceY(g6,g4) = 37.7
    c: PointOnObject(g12,g3)
    c: PointOnObject(g12,g1)
    c: Symmetric(g8,g11,g12)
    c: DistanceY(g12) = 10
    c: Radius(g8) = 0.8
FEATURE [PartDesign::Pocket] Pocket013  label="FP Screen visible hole"
  BaseFeature = -> Pocket010
  Direction = (0,1,2e-16)
  Length = 5
  Length2 = 100
  Profile = -> Sketch079
  Reversed = true
  Suppressed = false
  Type = 1
FEATURE [Sketcher::SketchObject] Sketch080  label="fp screen glass hole"
  ArcFitTolerance = 0
  AttachmentOffset = pos=(0,0,28.3) rot=(0,0,1;0rad)
  AttachmentSupport = -> [XZ_Plane043]
  FullyConstrained = true
  MakeInternals = false
  MapMode = 5
  Placement = pos=(0,-28.3,6.3e-15) rot=(1,0,0;1.5708rad)
  sketch-geometry (13):
    g0: LineSegment [constr] StartX=-33.35 StartY=31.4 StartZ=0 EndX=27 EndY=31.4 EndZ=0
    g1: LineSegment [constr] StartX=27 StartY=31.4 StartZ=0 EndX=27 EndY=-11.4 EndZ=0
    g2: LineSegment [constr] StartX=27 StartY=-11.4 StartZ=0 EndX=-33.35 EndY=-11.4 EndZ=0
    g3: LineSegment [constr] StartX=-33.35 StartY=-11.4 StartZ=0 EndX=-33.35 EndY=31.4 EndZ=0
    g4: LineSegment [constr] StartX=-33.35 StartY=10 StartZ=0 EndX=27 EndY=10 EndZ=0
    g5: LineSegment StartX=29 StartY=31.4 StartZ=0 EndX=29 EndY=-11.4 EndZ=0
    g6: ArcOfCircle CenterX=27 CenterY=31.4 CenterZ=0 NormalX=0 NormalY=0 NormalZ=1 AngleXU=0 Radius=2 StartAngle=0 EndAngle=1.5708
    g7: ArcOfCircle CenterX=27 CenterY=-11.4 CenterZ=0 NormalX=0 NormalY=0 NormalZ=1 AngleXU=0 Radius=2 StartAngle=4.71239 EndAngle=6.28319
    g8: ArcOfCircle CenterX=-33.35 CenterY=-11.4 CenterZ=0 NormalX=0 NormalY=0 NormalZ=1 AngleXU=0 Radius=2 StartAngle=3.14159 EndAngle=4.71239
    g9: ArcOfCircle CenterX=-33.35 CenterY=31.4 CenterZ=0 NormalX=0 NormalY=0 NormalZ=1 AngleXU=0 Radius=2 StartAngle=1.5708 EndAngle=3.14159
    g10: LineSegment StartX=-33.35 StartY=33.4 StartZ=0 EndX=27 EndY=33.4 EndZ=0
    g11: LineSegment StartX=27 StartY=-13.4 StartZ=0 EndX=-33.35 EndY=-13.4 EndZ=0
    g12: LineSegment StartX=-35.35 StartY=-11.4 StartZ=0 EndX=-35.35 EndY=31.4 EndZ=0
  constraints (31):
    c: Coincident(g0,g1)
    c: Coincident(g1,g2)
    c: Coincident(g2,g3)
    c: Coincident(g3,g0)
    c: Horizontal(g0)
    c: Horizontal(g2)
    c: Vertical(g1)
    c: Vertical(g3)
    c: DistanceY(g1,g1) = 42.8
    c: DistanceX(g2,g2) = 60.35
    c: PointOnObject(g4,g3)
    c: Symmetric(g0,g1,g4)
    c: DistanceY(g4) = 10
    c: DistanceX(g0) = 27
    c: Vertical(g5)
    c: Tangent(g5,g6) = 1.5708
    c: Coincident(g0,g6)
    c: Coincident(g1,g7)
    c: Coincident(g2,g8)
    c: Coincident(g0,g9)
    c: Radius(g9) = 2
    c: Horizontal(g10)
    c: Tangent(g8,g11) = 1.5708
    c: Tangent(g9,g12) = 1.5708
    c: PointOnObject(g4,g1)
    c: Tangent(g9,g10) = 1.5708
    c: Tangent(g6,g10) = 1.5708
    c: Tangent(g7,g5) = 1.5708
    c: Tangent(g11,g7) = 1.5708
    c: Tangent(g8,g12) = 1.5708
    c: Vertical(g12)
FEATURE [PartDesign::Pocket] Pocket014  label="FP Screen glass hole"
  BaseFeature = -> Pocket013
  Direction = (0,1,2e-16)
  Length = 5
  Length2 = 100
  Profile = -> Sketch080
  Suppressed = false
  Type = 1
FEATURE [Sketcher::SketchObject] Sketch081  label="fp screen PCB hole"
  ArcFitTolerance = 0
  AttachmentOffset = pos=(0,0,25) rot=(0,0,1;0rad)
  AttachmentSupport = -> [XZ_Plane043]
  FullyConstrained = true
  MakeInternals = false
  MapMode = 5
  Placement = pos=(0,-25,5.6e-15) rot=(1,0,0;1.5708rad)
  sketch-geometry (22):
    g0: LineSegment StartX=-32 StartY=40 StartZ=0 EndX=28 EndY=40 EndZ=0
    g1: LineSegment StartX=36 StartY=32 StartZ=0 EndX=36 EndY=27.7 EndZ=0
    g2: LineSegment StartX=28 StartY=-40 StartZ=0 EndX=-32 EndY=-40 EndZ=0
    g3: LineSegment StartX=-46 StartY=-26 StartZ=0 EndX=-46 EndY=26 EndZ=0
    g4: ArcOfCircle CenterX=28 CenterY=32 CenterZ=0 NormalX=0 NormalY=0 NormalZ=1 AngleXU=0 Radius=8 StartAngle=0 EndAngle=1.5708
    g5: ArcOfCircle CenterX=28 CenterY=-32 CenterZ=0 NormalX=0 NormalY=0 NormalZ=1 AngleXU=0 Radius=8 StartAngle=4.71239 EndAngle=6.28319
    g6: ArcOfCircle CenterX=38 CenterY=25 CenterZ=0 NormalX=0 NormalY=0 NormalZ=1 AngleXU=0 Radius=2.7 StartAngle=4.71239 EndAngle=7.85398
    g7: ArcOfCircle CenterX=38 CenterY=10 CenterZ=0 NormalX=0 NormalY=0 NormalZ=1 AngleXU=0 Radius=2.7 StartAngle=4.71239 EndAngle=7.85398
    g8: ArcOfCircle CenterX=38 CenterY=-5 CenterZ=0 NormalX=0 NormalY=0 NormalZ=1 AngleXU=0 Radius=2.7 StartAngle=4.71239 EndAngle=7.85398
    g9: LineSegment [constr] StartX=38 StartY=-5 StartZ=0 EndX=38 EndY=10 EndZ=0
    g10: LineSegment [constr] StartX=38 StartY=10 StartZ=0 EndX=38 EndY=25 EndZ=0
    g11: LineSegment StartX=38 StartY=27.7 StartZ=0 EndX=36 EndY=27.7 EndZ=0
    g12: LineSegment StartX=38 StartY=22.3 StartZ=0 EndX=36 EndY=22.3 EndZ=0
    g13: LineSegment StartX=36 StartY=22.3 StartZ=0 EndX=36 EndY=12.7 EndZ=0
    g14: LineSegment StartX=38 StartY=12.7 StartZ=0 EndX=36 EndY=12.7 EndZ=0
    g15: LineSegment StartX=38 StartY=7.3 StartZ=0 EndX=36 EndY=7.3 EndZ=0
    g16: LineSegment StartX=36 StartY=7.3 StartZ=0 EndX=36 EndY=-2.3 EndZ=0
    g17: LineSegment StartX=38 StartY=-2.3 StartZ=0 EndX=36 EndY=-2.3 EndZ=0
    g18: LineSegment StartX=38 StartY=-7.7 StartZ=0 EndX=36 EndY=-7.7 EndZ=0
    g19: LineSegment StartX=36 StartY=-7.7 StartZ=0 EndX=36 EndY=-32 EndZ=0
    g20: ArcOfCircle CenterX=-32 CenterY=26 CenterZ=0 NormalX=0 NormalY=0 NormalZ=1 AngleXU=0 Radius=14 StartAngle=1.5708 EndAngle=3.14159
    g21: ArcOfCircle CenterX=-32 CenterY=-26 CenterZ=0 NormalX=0 NormalY=0 NormalZ=1 AngleXU=0 Radius=14 StartAngle=3.14159 EndAngle=4.71239
  constraints (53):
    c: Horizontal(g0)
    c: Horizontal(g2)
    c: Vertical(g1)
    c: Tangent(g1,g4) = 1.5708
    c: Tangent(g0,g4) = 1.5708
    c: Tangent(g2,g5) = 1.5708
    c: Symmetric(g5,g4,g-1)
    c: DistanceY(g2,g0) = 80
    c: DistanceX(g1) = 36
    c: Radius(g4) = 8
    c: Coincident(g9,g8)
    c: Coincident(g9,g7)
    c: Vertical(g9)
    c: Coincident(g10,g7)
    c: Coincident(g10,g6)
    c: Vertical(g10)
    c: DistanceY(g7) = 10
    c: Equal(g9,g10)
    c: DistanceY(g8,g6) = 30
    c: DistanceX(g6) = 38
    c: Horizontal(g11)
    c: Horizontal(g12)
    c: Tangent(g6,g12) = 1.5708
    c: Tangent(g6,g11) = -1.5708
    c: Tangent(g1,g13)
    c: Coincident(g11,g1)
    c: Coincident(g12,g13)
    c: Horizontal(g14)
    c: Horizontal(g15)
    c: Tangent(g7,g15) = 1.5708
    c: Tangent(g7,g14) = -1.5708
    c: Tangent(g13,g16)
    c: Coincident(g14,g13)
    c: Coincident(g15,g16)
    c: Horizontal(g17)
    c: Horizontal(g18)
    c: Tangent(g8,g17) = -1.5708
    c: Tangent(g8,g18) = 1.5708
    c: Tangent(g16,g19)
    c: Coincident(g17,g16)
    c: Coincident(g18,g19)
    c: Equal(g8,g7)
    c: Equal(g7,g6)
    c: Radius(g6) = 2.7
    c: Tangent(g5,g19) = 1.5708
    c: Tangent(g0,g20) = 1.5708
    c: Tangent(g3,g20) = 1.5708
    c: Tangent(g2,g21) = 1.5708
    c: Tangent(g3,g21) = 1.5708
    c: Equal(g20,g21)
    c: Radius(g20) = 14
    c: Vertical(g3)
    c: DistanceX(g3,g-1) = 46
FEATURE [PartDesign::Pocket] Pocket015  label="FP Screen PCB hole"
  BaseFeature = -> Pocket014
  Direction = (0,1,2e-16)
  Length = 5
  Length2 = 100
  Profile = -> Sketch081
  Suppressed = false
  Type = 1
FEATURE [Sketcher::SketchObject] Sketch082  label="fp cross connect pcb hole"
  ArcFitTolerance = 0
  AttachmentOffset = pos=(0,0,19.65) rot=(0,0,1;0rad)
  AttachmentSupport = -> [XZ_Plane043]
  FullyConstrained = true
  MakeInternals = false
  MapMode = 5
  Placement = pos=(0,-19.65,4.4e-15) rot=(1,0,0;1.5708rad)
  sketch-geometry (18):
    g0: LineSegment StartX=-48 StartY=38.5 StartZ=0 EndX=48 EndY=38.5 EndZ=0
    g1: LineSegment StartX=49.5 StartY=37 StartZ=0 EndX=49.5 EndY=-38 EndZ=0
    g2: LineSegment StartX=48 StartY=-39.5 StartZ=0 EndX=-48 EndY=-39.5 EndZ=0
    g3: LineSegment StartX=-49.5 StartY=-38 StartZ=0 EndX=-49.5 EndY=-3.25 EndZ=0
    g4: LineSegment [constr] StartX=48 StartY=37 StartZ=0 EndX=-48 EndY=37 EndZ=0
    g5: LineSegment [constr] StartX=-48 StartY=37 StartZ=0 EndX=-48 EndY=-38 EndZ=0
    g6: LineSegment [constr] StartX=-48 StartY=-38 StartZ=0 EndX=48 EndY=-38 EndZ=0
    g7: LineSegment [constr] StartX=48 StartY=-38 StartZ=0 EndX=48 EndY=37 EndZ=0
    g8: ArcOfCircle CenterX=48 CenterY=37 CenterZ=0 NormalX=0 NormalY=0 NormalZ=1 AngleXU=0 Radius=1.5 StartAngle=1.7e-15 EndAngle=1.5708
    g9: ArcOfCircle CenterX=48 CenterY=-38 CenterZ=0 NormalX=0 NormalY=0 NormalZ=1 AngleXU=0 Radius=1.5 StartAngle=4.71239 EndAngle=6.28319
    g10: ArcOfCircle CenterX=-48 CenterY=-38 CenterZ=0 NormalX=0 NormalY=0 NormalZ=1 AngleXU=0 Radius=1.5 StartAngle=3.14159 EndAngle=4.71239
    g11: ArcOfCircle CenterX=-48 CenterY=37 CenterZ=0 NormalX=0 NormalY=0 NormalZ=1 AngleXU=0 Radius=1.5 StartAngle=1.5708 EndAngle=3.14159
    g12: LineSegment StartX=-47.5 StartY=1.25 StartZ=0 EndX=-45.5 EndY=1.25 EndZ=0
    g13: LineSegment StartX=-45.5 StartY=1.25 StartZ=0 EndX=-45.5 EndY=-1.25 EndZ=0
    g14: LineSegment StartX=-45.5 StartY=-1.25 StartZ=0 EndX=-47.5 EndY=-1.25 EndZ=0
    g15: LineSegment StartX=-49.5 StartY=3.25 StartZ=0 EndX=-49.5 EndY=37 EndZ=0
    g16: ArcOfCircle CenterX=-47.5 CenterY=3.25 CenterZ=0 NormalX=0 NormalY=0 NormalZ=1 AngleXU=0 Radius=2 StartAngle=3.14159 EndAngle=4.71239
    g17: ArcOfCircle CenterX=-47.5 CenterY=-3.25 CenterZ=0 NormalX=0 NormalY=0 NormalZ=1 AngleXU=0 Radius=2 StartAngle=1.5708 EndAngle=3.14159
  constraints (41):
    c: Horizontal(g0)
    c: Horizontal(g2)
    c: Vertical(g1)
    c: Vertical(g3)
    c: Coincident(g4,g5)
    c: Coincident(g5,g6)
    c: Coincident(g6,g7)
    c: Coincident(g7,g4)
    c: Horizontal(g6)
    c: Vertical(g5)
    c: Symmetric(g4,g4,g-2)
    c: DistanceX(g4,g4) = 96
    c: DistanceY(g7,g7) = 75
    c: DistanceY(g4) = 37
    c: Tangent(g1,g8) = 1.5708
    c: Tangent(g0,g8) = 1.5708
    c: Tangent(g1,g9) = 1.5708
    c: Tangent(g2,g9) = 1.5708
    c: Tangent(g2,g10) = 1.5708
    c: Tangent(g3,g10) = 1.5708
    c: Tangent(g0,g11) = 1.5708
    c: Coincident(g4,g11)
    c: Coincident(g4,g8)
    c: Coincident(g6,g9)
    c: Coincident(g5,g10)
    c: Radius(g8) = 1.5
    c: Coincident(g12,g13)
    c: Coincident(g13,g14)
    c: Horizontal(g12)
    c: Horizontal(g14)
    c: Vertical(g13)
    c: Tangent(g3,g15)
    c: Tangent(g12,g16) = -1.5708
    c: Tangent(g15,g16) = 1.5708
    c: Tangent(g14,g17) = -1.5708
    c: Tangent(g3,g17) = 1.5708
    c: Symmetric(g17,g16,g-1)
    c: DistanceY(g13,g13) = 2.5
    c: DistanceX(g15,g12) = 4
    c: Radius(g16) = 2
    c: Tangent(g11,g15) = 1.5708
FEATURE [PartDesign::Pocket] Pocket016  label="FP Cross connect PCB hole"
  BaseFeature = -> Pocket015
  Direction = (0,1,2e-16)
  Length = 5
  Length2 = 100
  Profile = -> Sketch082
  Suppressed = false
  Type = 1
FEATURE [Sketcher::SketchObject] Sketch083  label="fp V groove"
  ArcFitTolerance = 0
  AttachmentSupport = -> [YZ_Plane043]
  FullyConstrained = true
  MakeInternals = false
  MapMode = 5
  Placement = pos=(0,0,0) rot=(0.57735,0.57735,0.57735;2.0944rad)
  sketch-geometry (5):
    g0: LineSegment StartX=-9 StartY=45.1321 StartZ=0 EndX=-12.5 EndY=43.5 EndZ=0
    g1: LineSegment StartX=-12.5 StartY=43.5 StartZ=0 EndX=-12.5 EndY=42.5 EndZ=0
    g2: LineSegment StartX=-12.5 StartY=42.5 StartZ=0 EndX=-9 EndY=40.8679 EndZ=0
    g3: LineSegment StartX=-9 StartY=40.8679 StartZ=0 EndX=-9 EndY=45.1321 EndZ=0
    g4: LineSegment [constr] StartX=-12.5 StartY=43 StartZ=0 EndX=-9 EndY=43 EndZ=0
  constraints (14):
    c: Coincident(g0,g1)
    c: Vertical(g1)
    c: Coincident(g1,g2)
    c: Coincident(g2,g3)
    c: Coincident(g3,g0)
    c: DistanceX(g0,g-1) = 9
    c: DistanceX(g0,g-1) = 12.5
    c: PointOnObject(g4,g1)
    c: PointOnObject(g4,g3)
    c: Symmetric(g2,g0,g4)
    c: Symmetric(g1,g0,g4)
    c: DistanceY(g1,g1) = 1
    c: Angle(g2,g0) = 0.872665
    c: DistanceY(g4) = 43
FEATURE [PartDesign::SubtractivePipe] SubtractivePipe002  label="FP V groove"
  AuxilleryCurvelinear = true
  AuxillerySpineTangent = false
  BaseFeature = -> Pocket016
  Binormal = (0,0,0)
  Mode = 0
  Profile = -> Sketch083
  Spine = -> Sketch071
  SpineTangent = false
  Suppressed = false
  Transformation = 0
  Transition = 0
FEATURE [Sketcher::SketchObject] Sketch084  label="wp Rim top bottom"
  ArcFitTolerance = 0
  AttachmentSupport = -> [YZ_Plane018]
  FullyConstrained = true
  MakeInternals = false
  MapMode = 5
  Placement = pos=(0,0,0) rot=(0.57735,0.57735,0.57735;2.0944rad)
  sketch-geometry (5):
    g0: LineSegment StartX=-8.5 StartY=45.3321 StartZ=0 EndX=-11.5 EndY=43.6 EndZ=0
    g1: LineSegment StartX=-11.5 StartY=43.6 StartZ=0 EndX=-11.5 EndY=42.4 EndZ=0
    g2: LineSegment StartX=-11.5 StartY=42.4 StartZ=0 EndX=-8.5 EndY=40.6679 EndZ=0
    g3: LineSegment StartX=-8.5 StartY=40.6679 StartZ=0 EndX=-8.5 EndY=45.3321 EndZ=0
    g4: LineSegment [constr] StartX=-11.5 StartY=43 StartZ=0 EndX=-8.5 EndY=43 EndZ=0
  constraints (14):
    c: Coincident(g0,g1)
    c: Vertical(g1)
    c: Coincident(g1,g2)
    c: Coincident(g2,g3)
    c: Coincident(g3,g0)
    c: DistanceX(g0,g-1) = 8.5
    c: DistanceX(g0,g-1) = 11.5
    c: PointOnObject(g4,g1)
    c: PointOnObject(g4,g3)
    c: Symmetric(g2,g0,g4)
    c: Symmetric(g1,g0,g4)
    c: DistanceY(g1,g1) = 1.2
    c: Angle(g2,g0) = 1.0472
    c: DistanceY(g4) = 43
FEATURE [Sketcher::SketchObject] Sketch085  label="wp inner slit screw right"
  ArcFitTolerance = 0
  AttachmentSupport = -> [XZ_Plane018]
  ExternalGeometry = -> [DatumPlane]
  FullyConstrained = true
  MakeInternals = false
  MapMode = 5
  Placement = pos=(0,0,0) rot=(1,0,0;1.5708rad)
  sketch-geometry (4):
    g0: ArcOfCircle CenterX=50 CenterY=10 CenterZ=0 NormalX=0 NormalY=0 NormalZ=1 AngleXU=0 Radius=4.7 StartAngle=1e-16 EndAngle=3.14159
    g1: ArcOfCircle CenterX=50 CenterY=-12 CenterZ=0 NormalX=0 NormalY=0 NormalZ=1 AngleXU=0 Radius=4.7 StartAngle=3.14159 EndAngle=6.28319
    g2: LineSegment StartX=45.3 StartY=10 StartZ=0 EndX=45.3 EndY=-12 EndZ=0
    g3: LineSegment StartX=54.7 StartY=10 StartZ=0 EndX=54.7 EndY=-12 EndZ=0
  constraints (9):
    c: Tangent(g0,g3) = 1.5708
    c: Tangent(g0,g2) = -1.5708
    c: Tangent(g2,g1) = -1.5708
    c: Tangent(g3,g1) = 1.5708
    c: Vertical(g2)
    c: DistanceX(g0) = 50
    c: Radius(g0) = 4.7
    c: DistanceY(g1,g0) = 22
    c: Symmetric(g1,g0,g-3)
FEATURE [Sketcher::SketchObject] Sketch086  label="wp outer slit screw right"
  ArcFitTolerance = 0
  AttachmentOffset = pos=(0,0,3) rot=(0,0,1;0rad)
  AttachmentSupport = -> [XZ_Plane018]
  ExternalGeometry = -> [Sketch085]
  FullyConstrained = true
  MakeInternals = false
  MapMode = 5
  Placement = pos=(0,-3,7e-16) rot=(1,0,0;1.5708rad)
  sketch-geometry (4):
    g0: ArcOfCircle CenterX=50 CenterY=10 CenterZ=0 NormalX=0 NormalY=0 NormalZ=1 AngleXU=0 Radius=7.2 StartAngle=4.00905e-11 EndAngle=3.14159
    g1: ArcOfCircle CenterX=50 CenterY=-12 CenterZ=0 NormalX=0 NormalY=0 NormalZ=1 AngleXU=0 Radius=7.2 StartAngle=3.14159 EndAngle=6.28319
    g2: LineSegment StartX=42.8 StartY=10 StartZ=0 EndX=42.8 EndY=-12 EndZ=0
    g3: LineSegment StartX=57.2 StartY=10 StartZ=0 EndX=57.2 EndY=-12 EndZ=0
  constraints (8):
    c: Tangent(g0,g3) = 1.5708
    c: Tangent(g0,g2) = -1.5708
    c: Tangent(g2,g1) = -1.5708
    c: Tangent(g3,g1) = 1.5708
    c: Vertical(g2)
    c: Coincident(g1,g-4)
    c: Coincident(g0,g-3)
    c: Radius(g0) = 7.2
FEATURE [Sketcher::SketchObject] Sketch088  label="wp inner slit screw left"
  ArcFitTolerance = 0
  AttachmentSupport = -> [XZ_Plane018]
  ExternalGeometry = -> [DatumPlane]
  FullyConstrained = true
  MakeInternals = false
  MapMode = 5
  Placement = pos=(0,0,0) rot=(1,0,0;1.5708rad)
  sketch-geometry (5):
    g0: ArcOfCircle CenterX=-56 CenterY=-1 CenterZ=0 NormalX=0 NormalY=0 NormalZ=1 AngleXU=0 Radius=4.7 StartAngle=1.5708 EndAngle=4.71239
    g1: ArcOfCircle CenterX=-44 CenterY=-1 CenterZ=0 NormalX=0 NormalY=0 NormalZ=1 AngleXU=0 Radius=4.7 StartAngle=4.71239 EndAngle=7.85398
    g2: LineSegment StartX=-56 StartY=-5.7 StartZ=0 EndX=-44 EndY=-5.7 EndZ=0
    g3: LineSegment StartX=-56 StartY=3.7 StartZ=0 EndX=-44 EndY=3.7 EndZ=0
    g4: LineSegment [constr] StartX=-50 StartY=3.7 StartZ=0 EndX=-50 EndY=-5.7 EndZ=0
  constraints (13):
    c: Tangent(g0,g3) = 1.5708
    c: Tangent(g0,g2) = -1.5708
    c: Tangent(g2,g1) = -1.5708
    c: Tangent(g3,g1) = 1.5708
    c: Horizontal(g2)
    c: Equal(g0,g1)
    c: PointOnObject(g4,g3)
    c: PointOnObject(g4,g2)
    c: Symmetric(g1,g0,g4)
    c: DistanceX(g4,g-1) = 50
    c: Radius(g1) = 4.7
    c: DistanceX(g3,g3) = 12
    c: PointOnObject(g0,g-3)
FEATURE [Sketcher::SketchObject] Sketch087  label="wp outer slit screw left"
  ArcFitTolerance = 0
  AttachmentOffset = pos=(0,0,3) rot=(0,0,1;0rad)
  AttachmentSupport = -> [XZ_Plane018]
  ExternalGeometry = -> [Sketch088]
  FullyConstrained = true
  MakeInternals = false
  MapMode = 5
  Placement = pos=(0,-3,7e-16) rot=(1,0,0;1.5708rad)
  sketch-geometry (4):
    g0: ArcOfCircle CenterX=-56 CenterY=-1 CenterZ=0 NormalX=0 NormalY=0 NormalZ=1 AngleXU=0 Radius=7.2 StartAngle=1.5708 EndAngle=4.71239
    g1: ArcOfCircle CenterX=-44 CenterY=-1 CenterZ=0 NormalX=0 NormalY=0 NormalZ=1 AngleXU=0 Radius=7.2 StartAngle=4.71239 EndAngle=7.85398
    g2: LineSegment StartX=-56 StartY=-8.2 StartZ=0 EndX=-44 EndY=-8.2 EndZ=0
    g3: LineSegment StartX=-56 StartY=6.2 StartZ=0 EndX=-44 EndY=6.2 EndZ=0
  constraints (8):
    c: Tangent(g0,g3) = 1.5708
    c: Tangent(g0,g2) = -1.5708
    c: Tangent(g2,g1) = -1.5708
    c: Tangent(g3,g1) = 1.5708
    c: Horizontal(g2)
    c: Coincident(g0,g-3)
    c: Coincident(g1,g-4)
    c: Radius(g1) = 7.2
FEATURE [Sketcher::SketchObject] Sketch091  label="fp button hole"
  ArcFitTolerance = 0
  AttachmentOffset = pos=(0,0,-5) rot=(0,0,1;0rad)
  AttachmentSupport = -> [XY_Plane043]
  FullyConstrained = true
  MakeInternals = false
  MapMode = 5
  Placement = pos=(0,0,-5) rot=(0,0,1;0rad)
  sketch-geometry (8):
    g0: LineSegment StartX=38 StartY=-32 StartZ=0 EndX=38 EndY=0 EndZ=0
    g1: LineSegment StartX=38 StartY=0 StartZ=0 EndX=35.35 EndY=0 EndZ=0
    g2: LineSegment StartX=35.35 StartY=0 StartZ=0 EndX=35.35 EndY=-28 EndZ=0
    g3: LineSegment StartX=30.9303 StartY=-32 StartZ=0 EndX=38 EndY=-32 EndZ=0
    g4: LineSegment [constr] StartX=38 StartY=0 StartZ=0 EndX=38 EndY=2.65 EndZ=0
    g5: ArcOfCircle CenterX=38.7569 CenterY=-33.6569 CenterZ=0 NormalX=0 NormalY=0 NormalZ=1 AngleXU=0 Radius=8 StartAngle=2.35619 EndAngle=2.93298
    g6: LineSegment StartX=33.1 StartY=-28 StartZ=0 EndX=35.35 EndY=-28 EndZ=0
    g7: LineSegment [constr] StartX=35.35 StartY=-25.75 StartZ=0 EndX=33.1 EndY=-28 EndZ=0
  constraints (24):
    c: PointOnObject(g0,g-1)
    c: Vertical(g0)
    c: Coincident(g0,g1)
    c: PointOnObject(g1,g-1)
    c: Coincident(g1,g2)
    c: Vertical(g2)
    c: Coincident(g3,g0)
    c: Horizontal(g3)
    c: Coincident(g4,g0)
    c: Vertical(g4)
    c: Equal(g1,g4)
    c: DistanceX(g4) = 38
    c: DistanceX(g1,g1) = 2.65
    c: Coincident(g6,g5)
    c: Horizontal(g6)
    c: DistanceY(g5,g-1) = 28
    c: DistanceX(g5,g4) = 4.9
    c: Coincident(g6,g2)
    c: Coincident(g3,g5)
    c: DistanceY(g0,g0) = 32
    c: PointOnObject(g7,g2)
    c: Tangent(g7,g5) = -1.5708
    c: Angle(g2,g7) = 2.35619
    c: Radius(g5) = 8
FEATURE [PartDesign::Groove] Groove  label="FP First button hole"
  Angle = 360
  Angle2 = 60
  Axis = (0,2.65,0)
  Base = (38,0,-5)
  BaseFeature = -> SubtractivePipe002
  Profile = -> Sketch091
  ReferenceAxis = -> Sketch091 [Axis]
  Reversed = true
  Suppressed = false
  Type = 0
FEATURE [PartDesign::LinearPattern] LinearPattern003  label="FP Other button holes"
  BaseFeature = -> Groove
  Direction = -> Z_Axis043
  Length = 30
  Mode = 0
  Occurrences = 3
  Offset = 15
  Originals = -> [Groove]
  Suppressed = false
  TransformMode = 0
FEATURE [Sketcher::SketchObject] Sketch099  label="fp vent hole ESP"
  ArcFitTolerance = 0
  AttachmentOffset = pos=(0,0,-35) rot=(0,0,1;0rad)
  AttachmentSupport = -> [XY_Plane043]
  FullyConstrained = true
  MakeInternals = false
  MapMode = 5
  Placement = pos=(0,0,-35) rot=(0,0,1;0rad)
  sketch-geometry (4):
    g0: ArcOfCircle CenterX=-32 CenterY=-14.5 CenterZ=0 NormalX=0 NormalY=0 NormalZ=1 AngleXU=0 Radius=0.8 StartAngle=1.71e-14 EndAngle=3.14159
    g1: ArcOfCircle CenterX=-32 CenterY=-22.5 CenterZ=0 NormalX=0 NormalY=0 NormalZ=1 AngleXU=0 Radius=0.8 StartAngle=3.14159 EndAngle=6.28319
    g2: LineSegment StartX=-32.8 StartY=-14.5 StartZ=0 EndX=-32.8 EndY=-22.5 EndZ=0
    g3: LineSegment StartX=-31.2 StartY=-14.5 StartZ=0 EndX=-31.2 EndY=-22.5 EndZ=0
  constraints (10):
    c: Tangent(g0,g3) = 1.5708
    c: Tangent(g0,g2) = -1.5708
    c: Tangent(g2,g1) = -1.5708
    c: Tangent(g3,g1) = 1.5708
    c: Vertical(g2)
    c: Equal(g0,g1)
    c: DistanceY(g0,g-1) = 14.5
    c: DistanceY(g1,g-1) = 22.5
    c: DistanceX(g0,g0) = 1.6
    c: DistanceX(g0,g-1) = 32
FEATURE [Sketcher::SketchObject] Sketch100
  ArcFitTolerance = 0
  AttachmentSupport = -> [XZ_Plane044]
  FullyConstrained = false
  MakeInternals = false
  MapMode = 5
  Placement = pos=(0,0,0) rot=(1,0,0;1.5708rad)
  sketch-geometry (5):
    g0: LineSegment StartX=3.2 StartY=2.75 StartZ=0 EndX=5 EndY=2.75 EndZ=0
    g1: LineSegment StartX=5 StartY=2.75 StartZ=0 EndX=5 EndY=0 EndZ=0
    g2: LineSegment StartX=5 StartY=0 StartZ=0 EndX=1.5 EndY=0 EndZ=0
    g3: LineSegment StartX=1.5 StartY=0 StartZ=0 EndX=1.5 EndY=1.05 EndZ=0
    g4: LineSegment StartX=3.2 StartY=2.75 StartZ=0 EndX=1.5 EndY=1.05 EndZ=0
  constraints (15):
    c: Coincident(g0,g1)
    c: Coincident(g1,g2)
    c: Coincident(g2,g3)
    c: Horizontal(g0)
    c: Horizontal(g2)
    c: Vertical(g1)
    c: Vertical(g3)
    c: PointOnObject(g1,g-1)
    c: DistanceX(g1) = 5
    c: Coincident(g0,g4)
    c: Coincident(g4,g3)
    c: DistanceY(g0) = 2.75
    c: DistanceX(g2) = 1.5
    c: Angle(g3,g4) = 2.35619
    c: DistanceX(g0) = 3.2
FEATURE [PartDesign::Revolution] Revolution003
  Angle = 360
  Angle2 = 60
  Axis = (-3e-16,3e-16,1)
  Base = (0,0,0)
  Placement = pos=(0,0,0) rot=(1,0,0;1.5708rad)
  Profile = -> Sketch100
  ReferenceAxis = -> Z_Axis043
  Reversed = true
  Suppressed = false
  Type = 0
FEATURE [PartDesign::Body] Body039  label="RingMagnet10x2.75_2"
  AllowCompound = false
  Group = -> [Sketch100,Revolution003]
  Origin = -> Origin044
  Placement = pos=(-56,-10.7,22) rot=(1,0,0;1.5708rad)
  Tip = -> Revolution003
FEATURE [Sketcher::SketchObject] Sketch101  label="wp magnet island"
  ArcFitTolerance = 0
  AttachmentOffset = pos=(0,0,-56) rot=(0,0,1;0rad)
  AttachmentSupport = -> [YZ_Plane018]
  FullyConstrained = true
  MakeInternals = false
  MapMode = 5
  Placement = pos=(-56,0,0) rot=(0.57735,0.57735,0.57735;2.0944rad)
  sketch-geometry (6):
    g0: LineSegment StartX=-9 StartY=28 StartZ=0 EndX=-1 EndY=28 EndZ=0
    g1: LineSegment StartX=-1 StartY=28 StartZ=0 EndX=-1 EndY=22 EndZ=0
    g2: LineSegment StartX=-1 StartY=22 StartZ=0 EndX=-10 EndY=22 EndZ=0
    g3: LineSegment StartX=-10 StartY=22 StartZ=0 EndX=-10 EndY=27 EndZ=0
    g4: ArcOfCircle CenterX=-9 CenterY=27 CenterZ=0 NormalX=0 NormalY=0 NormalZ=1 AngleXU=0 Radius=1 StartAngle=1.5708 EndAngle=3.14159
    g5: LineSegment [constr] StartX=-10 StartY=22 StartZ=0 EndX=-15 EndY=22 EndZ=0
  constraints (17):
    c: Coincident(g0,g1)
    c: Coincident(g1,g2)
    c: Coincident(g2,g3)
    c: Horizontal(g0)
    c: Horizontal(g2)
    c: Vertical(g1)
    c: Vertical(g3)
    c: DistanceX(g1,g-1) = 1
    c: DistanceY(g1) = 22
    c: Tangent(g0,g4) = 1.5708
    c: Tangent(g3,g4) = 1.5708
    c: DistanceX(g0,g-1) = 9
    c: DistanceX(g3,g-1) = 10
    c: DistanceY(g1,g1) = 6
    c: Coincident(g5,g2)
    c: Horizontal(g5)
    c: Equal(g3,g5)
FEATURE [PartDesign::Revolution] Revolution  label="WP Magnet island"
  Angle = 360
  Angle2 = 60
  Axis = (-1.7e-15,-5,1.1e-15)
  Base = (-56,-10,22)
  BaseFeature = -> Pocket009
  Profile = -> Sketch101
  ReferenceAxis = -> Sketch101 [Axis]
  Reversed = true
  Suppressed = false
  Type = 0
FEATURE [PartDesign::Groove] Groove001  label="WP Magnet pocket"
  Angle = 360
  Angle2 = 60
  Axis = (1.7e-15,5.15,-1.1e-15)
  Base = (-56,-3.8,22)
  BaseFeature = -> Revolution
  Profile = -> Sketch068
  ReferenceAxis = -> Sketch068 [Axis]
  Reversed = true
  Suppressed = false
  Type = 0
FEATURE [PartDesign::MultiTransform] MultiTransform002  label="WP Other magnet pockets"
  BaseFeature = -> Groove001
  Originals = -> [Revolution,Groove001]
  Suppressed = false
  TransformMode = 0
  Transformations = -> [Mirrored011,Mirrored012]
FEATURE [PartDesign::AdditivePipe] AdditivePipe013  label="WP Rim top bottom"
  AuxilleryCurvelinear = true
  AuxillerySpineTangent = false
  BaseFeature = -> MultiTransform002
  Binormal = (0,0,0)
  Mode = 0
  Profile = -> Sketch084
  Spine = -> Sketch027
  SpineTangent = false
  Suppressed = false
  Transformation = 0
  Transition = 0
FEATURE [PartDesign::Pocket] Pocket017  label="WP Inner slit screw right"
  BaseFeature = -> AdditivePipe013
  Direction = (0,1,2e-16)
  Length = 5
  Length2 = 100
  Midplane = true
  Profile = -> Sketch085
  Suppressed = false
  Type = 1
FEATURE [PartDesign::Pocket] Pocket018  label="WP Outer slit screw right"
  BaseFeature = -> Pocket017
  Direction = (0,1,2e-16)
  Length = 5
  Length2 = 100
  Profile = -> Sketch086
  Reversed = true
  Suppressed = false
  Type = 1
FEATURE [PartDesign::Pocket] Pocket019  label="WP Inner slit screw left"
  BaseFeature = -> Pocket018
  Direction = (0,1,2e-16)
  Length = 5
  Length2 = 100
  Midplane = true
  Profile = -> Sketch088
  Suppressed = false
  Type = 1
FEATURE [PartDesign::Pocket] Pocket020  label="WP Outer slit screw left"
  BaseFeature = -> Pocket019
  Direction = (0,1,2e-16)
  Length = 5
  Length2 = 100
  Profile = -> Sketch087
  Reversed = true
  Suppressed = false
  Type = 1
FEATURE [PartDesign::LinearPattern] LinearPattern004
  Direction = -> X_Axis043
  Length = 50
  Mode = 0
  Occurrences = 16
  Offset = 3.33333
  Suppressed = false
  TransformMode = 0
FEATURE [PartDesign::Mirrored] Mirrored
  MirrorPlane = -> XY_Plane043
  Suppressed = false
  TransformMode = 0
FEATURE [Sketcher::SketchObject] Sketch102
  ArcFitTolerance = 0
  AttachmentOffset = pos=(0,0,10) rot=(0,0,1;0rad)
  AttachmentSupport = -> [YZ_Plane045]
  FullyConstrained = true
  MakeInternals = false
  MapMode = 5
  Placement = pos=(10,0,0) rot=(0.57735,0.57735,0.57735;2.0944rad)
  sketch-geometry (2):
    g0: ArcOfCircle CenterX=0 CenterY=0 CenterZ=0 NormalX=0 NormalY=0 NormalZ=1 AngleXU=0 Radius=2.3 StartAngle=5.68249 EndAngle=10.0255
    g1: LineSegment StartX=1.89737 StartY=-1.3 StartZ=0 EndX=-1.89737 EndY=-1.3 EndZ=0
  constraints (6):
    c: Coincident(g1,g0)
    c: Coincident(g1,g0)
    c: Coincident(g0,g-1)
    c: Diameter(g0) = 4.6
    c: Distance(g0,g1) = 1.3
    c: Horizontal(g1)
FEATURE [PartDesign::Pad] Pad026
  Direction = (1,1,1)
  Length = 4.7
  Length2 = 100
  Placement = pos=(0,0,0) rot=(0.57735,0.57735,0.57735;2.0944rad)
  Profile = -> Sketch102
  Suppressed = false
  Type = 0
FEATURE [PartDesign::Body] Body040  label="DallasSensor004"
  AllowCompound = false
  Group = -> [Sketch102,Pad026]
  Origin = -> Origin045
  Tip = -> Pad026
FEATURE [Sketcher::SketchObject] Sketch103  label="pin crs012"
  ArcFitTolerance = 0
  AttachmentOffset = pos=(0,0,-1) rot=(0,0,1;0rad)
  FullyConstrained = true
  MakeInternals = false
  MapMode = 5
  Placement = pos=(0,0,-1) rot=(0,0,1;0rad)
  sketch-geometry (4):
    g0: LineSegment StartX=-0.275 StartY=0.275 StartZ=0 EndX=0.275 EndY=0.275 EndZ=0
    g1: LineSegment StartX=0.275 StartY=0.275 StartZ=0 EndX=0.275 EndY=-0.275 EndZ=0
    g2: LineSegment StartX=0.275 StartY=-0.275 StartZ=0 EndX=-0.275 EndY=-0.275 EndZ=0
    g3: LineSegment StartX=-0.275 StartY=-0.275 StartZ=0 EndX=-0.275 EndY=0.275 EndZ=0
  constraints (10):
    c: Coincident(g0,g1)
    c: Coincident(g1,g2)
    c: Coincident(g2,g3)
    c: Coincident(g3,g0)
    c: Horizontal(g2)
    c: Vertical(g3)
    c: Symmetric(g1,g0,g-1)
    c: Symmetric(g0,g0,g-2)
    c: Equal(g0,g1)
    c: DistanceX(g0,g0) = 0.55
FEATURE [Sketcher::SketchObject] Sketch104  label="pin trj012"
  ArcFitTolerance = 0
  AttachmentSupport = -> [XZ_Plane046]
  FullyConstrained = true
  MakeInternals = false
  MapMode = 5
  Placement = pos=(0,0,0) rot=(1,0,0;1.5708rad)
  sketch-geometry (3):
    g0: LineSegment StartX=0.5 StartY=0 StartZ=0 EndX=10 EndY=0 EndZ=0
    g1: LineSegment StartX=0 StartY=-2.5 StartZ=0 EndX=0 EndY=-0.5 EndZ=0
    g2: ArcOfCircle CenterX=0.5 CenterY=-0.5 CenterZ=0 NormalX=0 NormalY=0 NormalZ=1 AngleXU=0 Radius=0.5 StartAngle=1.5708 EndAngle=3.14159
  constraints (9):
    c: Horizontal(g0)
    c: Vertical(g1)
    c: Tangent(g0,g2) = 1.5708
    c: Tangent(g1,g2) = 1.5708
    c: DistanceY(g1,g-1) = 2.5
    c: DistanceX(g-1,g0) = 10
    c: Radius(g2) = 0.5
    c: PointOnObject(g1,g-2)
    c: PointOnObject(g0,g-1)
FEATURE [PartDesign::AdditivePipe] AdditivePipe014
  AuxilleryCurvelinear = true
  AuxillerySpineTangent = false
  Binormal = (0,0,0)
  Mode = 0
  Placement = pos=(0,0,-1) rot=(0,0,1;0rad)
  Profile = -> Sketch103
  Spine = -> Sketch104
  SpineTangent = false
  Suppressed = false
  Transformation = 0
  Transition = 0
FEATURE [PartDesign::Body] Body041  label="DallasPin013"
  AllowCompound = false
  Group = -> [Sketch104,Sketch103,AdditivePipe014]
  Origin = -> Origin046
  Placement = pos=(0,0,0) rot=(1,0,0;3.14159rad)
  Tip = -> AdditivePipe014
FEATURE [Sketcher::SketchObject] Sketch105  label="pin crs013"
  ArcFitTolerance = 0
  AttachmentOffset = pos=(0,0,-1) rot=(0,0,1;0rad)
  FullyConstrained = true
  MakeInternals = false
  MapMode = 5
  Placement = pos=(0,0,-1) rot=(0,0,1;0rad)
  sketch-geometry (4):
    g0: LineSegment StartX=-0.275 StartY=0.275 StartZ=0 EndX=0.275 EndY=0.275 EndZ=0
    g1: LineSegment StartX=0.275 StartY=0.275 StartZ=0 EndX=0.275 EndY=-0.275 EndZ=0
    g2: LineSegment StartX=0.275 StartY=-0.275 StartZ=0 EndX=-0.275 EndY=-0.275 EndZ=0
    g3: LineSegment StartX=-0.275 StartY=-0.275 StartZ=0 EndX=-0.275 EndY=0.275 EndZ=0
  constraints (10):
    c: Coincident(g0,g1)
    c: Coincident(g1,g2)
    c: Coincident(g2,g3)
    c: Coincident(g3,g0)
    c: Horizontal(g2)
    c: Vertical(g3)
    c: Symmetric(g1,g0,g-1)
    c: Symmetric(g0,g0,g-2)
    c: Equal(g0,g1)
    c: DistanceX(g0,g0) = 0.55
FEATURE [Sketcher::SketchObject] Sketch106  label="pin trj013"
  ArcFitTolerance = 0
  AttachmentSupport = -> [XZ_Plane047]
  FullyConstrained = true
  MakeInternals = false
  MapMode = 5
  Placement = pos=(0,0,0) rot=(1,0,0;1.5708rad)
  sketch-geometry (3):
    g0: LineSegment StartX=0.5 StartY=0 StartZ=0 EndX=10 EndY=0 EndZ=0
    g1: LineSegment StartX=0 StartY=-2.5 StartZ=0 EndX=0 EndY=-0.5 EndZ=0
    g2: ArcOfCircle CenterX=0.5 CenterY=-0.5 CenterZ=0 NormalX=0 NormalY=0 NormalZ=1 AngleXU=0 Radius=0.5 StartAngle=1.5708 EndAngle=3.14159
  constraints (9):
    c: Horizontal(g0)
    c: Vertical(g1)
    c: Tangent(g0,g2) = 1.5708
    c: Tangent(g1,g2) = 1.5708
    c: DistanceY(g1,g-1) = 2.5
    c: DistanceX(g-1,g0) = 10
    c: Radius(g2) = 0.5
    c: PointOnObject(g1,g-2)
    c: PointOnObject(g0,g-1)
FEATURE [PartDesign::AdditivePipe] AdditivePipe015
  AuxilleryCurvelinear = true
  AuxillerySpineTangent = false
  Binormal = (0,0,0)
  Mode = 0
  Placement = pos=(0,0,-1) rot=(0,0,1;0rad)
  Profile = -> Sketch105
  Spine = -> Sketch106
  SpineTangent = false
  Suppressed = false
  Transformation = 0
  Transition = 0
FEATURE [PartDesign::Body] Body042  label="DallasPin014"
  AllowCompound = false
  Group = -> [Sketch106,Sketch105,AdditivePipe015]
  Origin = -> Origin047
  Placement = pos=(0,1.27,0) rot=(1,0,0;3.14159rad)
  Tip = -> AdditivePipe015
FEATURE [Sketcher::SketchObject] Sketch014  label="pin crs014"
  ArcFitTolerance = 0
  AttachmentOffset = pos=(0,0,-1) rot=(0,0,1;0rad)
  FullyConstrained = true
  MakeInternals = false
  MapMode = 5
  Placement = pos=(0,0,-1) rot=(0,0,1;0rad)
  sketch-geometry (4):
    g0: LineSegment StartX=-0.275 StartY=0.275 StartZ=0 EndX=0.275 EndY=0.275 EndZ=0
    g1: LineSegment StartX=0.275 StartY=0.275 StartZ=0 EndX=0.275 EndY=-0.275 EndZ=0
    g2: LineSegment StartX=0.275 StartY=-0.275 StartZ=0 EndX=-0.275 EndY=-0.275 EndZ=0
    g3: LineSegment StartX=-0.275 StartY=-0.275 StartZ=0 EndX=-0.275 EndY=0.275 EndZ=0
  constraints (10):
    c: Coincident(g0,g1)
    c: Coincident(g1,g2)
    c: Coincident(g2,g3)
    c: Coincident(g3,g0)
    c: Horizontal(g2)
    c: Vertical(g3)
    c: Symmetric(g1,g0,g-1)
    c: Symmetric(g0,g0,g-2)
    c: Equal(g0,g1)
    c: DistanceX(g0,g0) = 0.55
FEATURE [Sketcher::SketchObject] Sketch015  label="pin trj014"
  ArcFitTolerance = 0
  AttachmentSupport = -> [XZ_Plane009]
  FullyConstrained = true
  MakeInternals = false
  MapMode = 5
  Placement = pos=(0,0,0) rot=(1,0,0;1.5708rad)
  sketch-geometry (3):
    g0: LineSegment StartX=0.5 StartY=0 StartZ=0 EndX=10 EndY=0 EndZ=0
    g1: LineSegment StartX=0 StartY=-2.5 StartZ=0 EndX=0 EndY=-0.5 EndZ=0
    g2: ArcOfCircle CenterX=0.5 CenterY=-0.5 CenterZ=0 NormalX=0 NormalY=0 NormalZ=1 AngleXU=0 Radius=0.5 StartAngle=1.5708 EndAngle=3.14159
  constraints (9):
    c: Horizontal(g0)
    c: Vertical(g1)
    c: Tangent(g0,g2) = 1.5708
    c: Tangent(g1,g2) = 1.5708
    c: DistanceY(g1,g-1) = 2.5
    c: DistanceX(g-1,g0) = 10
    c: Radius(g2) = 0.5
    c: PointOnObject(g1,g-2)
    c: PointOnObject(g0,g-1)
FEATURE [PartDesign::AdditivePipe] AdditivePipe016
  AuxilleryCurvelinear = true
  AuxillerySpineTangent = false
  Binormal = (0,0,0)
  Mode = 0
  Placement = pos=(0,0,-1) rot=(0,0,1;0rad)
  Profile = -> Sketch014
  Spine = -> Sketch015
  SpineTangent = false
  Suppressed = false
  Transformation = 0
  Transition = 0
FEATURE [PartDesign::Body] Body009  label="DallasPin001"
  AllowCompound = false
  Group = -> [Sketch015,Sketch014,AdditivePipe016]
  Origin = -> Origin009
  Placement = pos=(0,-1.27,0) rot=(1,0,0;3.14159rad)
  Tip = -> AdditivePipe016
FEATURE [App::LinkGroup] LinkGroup
  ElementList = -> [Body040,Body041,Body042,Body009]
  LinkMode = 0
FEATURE [Part::Compound] Compound007  label="Dallas DS18B20_1"
  Links = -> [LinkGroup]
  Placement = pos=(-45,-16,31.99) rot=(0,0.707107,-0.707107;3.14159rad)
FEATURE [Sketcher::SketchObject] Sketch107
  ArcFitTolerance = 0
  AttachmentOffset = pos=(0,0,10) rot=(0,0,1;0rad)
  AttachmentSupport = -> [YZ_Plane048]
  FullyConstrained = true
  MakeInternals = false
  MapMode = 5
  Placement = pos=(10,0,0) rot=(0.57735,0.57735,0.57735;2.0944rad)
  sketch-geometry (2):
    g0: ArcOfCircle CenterX=0 CenterY=0 CenterZ=0 NormalX=0 NormalY=0 NormalZ=1 AngleXU=0 Radius=2.3 StartAngle=5.68249 EndAngle=10.0255
    g1: LineSegment StartX=1.89737 StartY=-1.3 StartZ=0 EndX=-1.89737 EndY=-1.3 EndZ=0
  constraints (6):
    c: Coincident(g1,g0)
    c: Coincident(g1,g0)
    c: Coincident(g0,g-1)
    c: Diameter(g0) = 4.6
    c: Distance(g0,g1) = 1.3
    c: Horizontal(g1)
FEATURE [PartDesign::Pad] Pad027
  Direction = (1,1,1)
  Length = 4.7
  Length2 = 100
  Placement = pos=(0,0,0) rot=(0.57735,0.57735,0.57735;2.0944rad)
  Profile = -> Sketch107
  Suppressed = false
  Type = 0
FEATURE [PartDesign::Body] Body046  label="DallasSensor005"
  AllowCompound = false
  Group = -> [Sketch107,Pad027]
  Origin = -> Origin050
  Tip = -> Pad027
FEATURE [Sketcher::SketchObject] Sketch108  label="pin trj015"
  ArcFitTolerance = 0
  AttachmentSupport = -> [XZ_Plane049]
  FullyConstrained = true
  MakeInternals = false
  MapMode = 5
  Placement = pos=(0,0,0) rot=(1,0,0;1.5708rad)
  sketch-geometry (3):
    g0: LineSegment StartX=0.5 StartY=0 StartZ=0 EndX=10 EndY=0 EndZ=0
    g1: LineSegment StartX=0 StartY=-2.5 StartZ=0 EndX=0 EndY=-0.5 EndZ=0
    g2: ArcOfCircle CenterX=0.5 CenterY=-0.5 CenterZ=0 NormalX=0 NormalY=0 NormalZ=1 AngleXU=0 Radius=0.5 StartAngle=1.5708 EndAngle=3.14159
  constraints (9):
    c: Horizontal(g0)
    c: Vertical(g1)
    c: Tangent(g0,g2) = 1.5708
    c: Tangent(g1,g2) = 1.5708
    c: DistanceY(g1,g-1) = 2.5
    c: DistanceX(g-1,g0) = 10
    c: Radius(g2) = 0.5
    c: PointOnObject(g1,g-2)
    c: PointOnObject(g0,g-1)
FEATURE [Sketcher::SketchObject] Sketch109  label="pin crs015"
  ArcFitTolerance = 0
  AttachmentOffset = pos=(0,0,-1) rot=(0,0,1;0rad)
  FullyConstrained = true
  MakeInternals = false
  MapMode = 5
  Placement = pos=(0,0,-1) rot=(0,0,1;0rad)
  sketch-geometry (4):
    g0: LineSegment StartX=-0.275 StartY=0.275 StartZ=0 EndX=0.275 EndY=0.275 EndZ=0
    g1: LineSegment StartX=0.275 StartY=0.275 StartZ=0 EndX=0.275 EndY=-0.275 EndZ=0
    g2: LineSegment StartX=0.275 StartY=-0.275 StartZ=0 EndX=-0.275 EndY=-0.275 EndZ=0
    g3: LineSegment StartX=-0.275 StartY=-0.275 StartZ=0 EndX=-0.275 EndY=0.275 EndZ=0
  constraints (10):
    c: Coincident(g0,g1)
    c: Coincident(g1,g2)
    c: Coincident(g2,g3)
    c: Coincident(g3,g0)
    c: Horizontal(g2)
    c: Vertical(g3)
    c: Symmetric(g1,g0,g-1)
    c: Symmetric(g0,g0,g-2)
    c: Equal(g0,g1)
    c: DistanceX(g0,g0) = 0.55
FEATURE [Sketcher::SketchObject] Sketch110  label="pin crs016"
  ArcFitTolerance = 0
  AttachmentOffset = pos=(0,0,-1) rot=(0,0,1;0rad)
  FullyConstrained = true
  MakeInternals = false
  MapMode = 5
  Placement = pos=(0,0,-1) rot=(0,0,1;0rad)
  sketch-geometry (4):
    g0: LineSegment StartX=-0.275 StartY=0.275 StartZ=0 EndX=0.275 EndY=0.275 EndZ=0
    g1: LineSegment StartX=0.275 StartY=0.275 StartZ=0 EndX=0.275 EndY=-0.275 EndZ=0
    g2: LineSegment StartX=0.275 StartY=-0.275 StartZ=0 EndX=-0.275 EndY=-0.275 EndZ=0
    g3: LineSegment StartX=-0.275 StartY=-0.275 StartZ=0 EndX=-0.275 EndY=0.275 EndZ=0
  constraints (10):
    c: Coincident(g0,g1)
    c: Coincident(g1,g2)
    c: Coincident(g2,g3)
    c: Coincident(g3,g0)
    c: Horizontal(g2)
    c: Vertical(g3)
    c: Symmetric(g1,g0,g-1)
    c: Symmetric(g0,g0,g-2)
    c: Equal(g0,g1)
    c: DistanceX(g0,g0) = 0.55
FEATURE [PartDesign::AdditivePipe] AdditivePipe018
  AuxilleryCurvelinear = true
  AuxillerySpineTangent = false
  Binormal = (0,0,0)
  Mode = 0
  Placement = pos=(0,0,-1) rot=(0,0,1;0rad)
  Profile = -> Sketch110
  Spine = -> Sketch108
  SpineTangent = false
  Suppressed = false
  Transformation = 0
  Transition = 0
FEATURE [PartDesign::Body] Body045  label="DallasPin017"
  AllowCompound = false
  Group = -> [Sketch108,Sketch110,AdditivePipe018]
  Origin = -> Origin048
  Placement = pos=(0,0,0) rot=(1,0,0;3.14159rad)
  Tip = -> AdditivePipe018
FEATURE [Sketcher::SketchObject] Sketch111  label="pin crs017"
  ArcFitTolerance = 0
  AttachmentOffset = pos=(0,0,-1) rot=(0,0,1;0rad)
  FullyConstrained = true
  MakeInternals = false
  MapMode = 5
  Placement = pos=(0,0,-1) rot=(0,0,1;0rad)
  sketch-geometry (4):
    g0: LineSegment StartX=-0.275 StartY=0.275 StartZ=0 EndX=0.275 EndY=0.275 EndZ=0
    g1: LineSegment StartX=0.275 StartY=0.275 StartZ=0 EndX=0.275 EndY=-0.275 EndZ=0
    g2: LineSegment StartX=0.275 StartY=-0.275 StartZ=0 EndX=-0.275 EndY=-0.275 EndZ=0
    g3: LineSegment StartX=-0.275 StartY=-0.275 StartZ=0 EndX=-0.275 EndY=0.275 EndZ=0
  constraints (10):
    c: Coincident(g0,g1)
    c: Coincident(g1,g2)
    c: Coincident(g2,g3)
    c: Coincident(g3,g0)
    c: Horizontal(g2)
    c: Vertical(g3)
    c: Symmetric(g1,g0,g-1)
    c: Symmetric(g0,g0,g-2)
    c: Equal(g0,g1)
    c: DistanceX(g0,g0) = 0.55
FEATURE [Sketcher::SketchObject] Sketch112  label="pin trj016"
  ArcFitTolerance = 0
  AttachmentSupport = -> [XZ_Plane050]
  FullyConstrained = true
  MakeInternals = false
  MapMode = 5
  Placement = pos=(0,0,0) rot=(1,0,0;1.5708rad)
  sketch-geometry (3):
    g0: LineSegment StartX=0.5 StartY=0 StartZ=0 EndX=10 EndY=0 EndZ=0
    g1: LineSegment StartX=0 StartY=-2.5 StartZ=0 EndX=0 EndY=-0.5 EndZ=0
    g2: ArcOfCircle CenterX=0.5 CenterY=-0.5 CenterZ=0 NormalX=0 NormalY=0 NormalZ=1 AngleXU=0 Radius=0.5 StartAngle=1.5708 EndAngle=3.14159
  constraints (9):
    c: Horizontal(g0)
    c: Vertical(g1)
    c: Tangent(g0,g2) = 1.5708
    c: Tangent(g1,g2) = 1.5708
    c: DistanceY(g1,g-1) = 2.5
    c: DistanceX(g-1,g0) = 10
    c: Radius(g2) = 0.5
    c: PointOnObject(g1,g-2)
    c: PointOnObject(g0,g-1)
FEATURE [PartDesign::AdditivePipe] AdditivePipe017
  AuxilleryCurvelinear = true
  AuxillerySpineTangent = false
  Binormal = (0,0,0)
  Mode = 0
  Placement = pos=(0,0,-1) rot=(0,0,1;0rad)
  Profile = -> Sketch109
  Spine = -> Sketch112
  SpineTangent = false
  Suppressed = false
  Transformation = 0
  Transition = 0
FEATURE [PartDesign::Body] Body044  label="DallasPin016"
  AllowCompound = false
  Group = -> [Sketch112,Sketch109,AdditivePipe017]
  Origin = -> Origin051
  Placement = pos=(0,1.27,0) rot=(1,0,0;3.14159rad)
  Tip = -> AdditivePipe017
FEATURE [Sketcher::SketchObject] Sketch113  label="pin trj017"
  ArcFitTolerance = 0
  AttachmentSupport = -> [XZ_Plane051]
  FullyConstrained = true
  MakeInternals = false
  MapMode = 5
  Placement = pos=(0,0,0) rot=(1,0,0;1.5708rad)
  sketch-geometry (3):
    g0: LineSegment StartX=0.5 StartY=0 StartZ=0 EndX=10 EndY=0 EndZ=0
    g1: LineSegment StartX=0 StartY=-2.5 StartZ=0 EndX=0 EndY=-0.5 EndZ=0
    g2: ArcOfCircle CenterX=0.5 CenterY=-0.5 CenterZ=0 NormalX=0 NormalY=0 NormalZ=1 AngleXU=0 Radius=0.5 StartAngle=1.5708 EndAngle=3.14159
  constraints (9):
    c: Horizontal(g0)
    c: Vertical(g1)
    c: Tangent(g0,g2) = 1.5708
    c: Tangent(g1,g2) = 1.5708
    c: DistanceY(g1,g-1) = 2.5
    c: DistanceX(g-1,g0) = 10
    c: Radius(g2) = 0.5
    c: PointOnObject(g1,g-2)
    c: PointOnObject(g0,g-1)
FEATURE [PartDesign::AdditivePipe] AdditivePipe019
  AuxilleryCurvelinear = true
  AuxillerySpineTangent = false
  Binormal = (0,0,0)
  Mode = 0
  Placement = pos=(0,0,-1) rot=(0,0,1;0rad)
  Profile = -> Sketch111
  Spine = -> Sketch113
  SpineTangent = false
  Suppressed = false
  Transformation = 0
  Transition = 0
FEATURE [PartDesign::Body] Body043  label="DallasPin015"
  AllowCompound = false
  Group = -> [Sketch113,Sketch111,AdditivePipe019]
  Origin = -> Origin049
  Placement = pos=(0,-1.27,0) rot=(1,0,0;3.14159rad)
  Tip = -> AdditivePipe019
FEATURE [App::LinkGroup] LinkGroup001
  ElementList = -> [Body046,Body045,Body044,Body043]
  LinkMode = 0
FEATURE [Part::Compound] Compound008  label="Dallas DS18B20_2"
  Links = -> [LinkGroup001]
  Placement = pos=(-45,-16,-34.01) rot=(0,0.707107,-0.707107;3.14159rad)
FEATURE [Sketcher::SketchObject] Sketch114  label="pin crs018"
  ArcFitTolerance = 0
  AttachmentOffset = pos=(0,0,-1) rot=(0,0,1;0rad)
  FullyConstrained = true
  MakeInternals = false
  MapMode = 5
  Placement = pos=(0,0,-1) rot=(0,0,1;0rad)
  sketch-geometry (4):
    g0: LineSegment StartX=-0.275 StartY=0.275 StartZ=0 EndX=0.275 EndY=0.275 EndZ=0
    g1: LineSegment StartX=0.275 StartY=0.275 StartZ=0 EndX=0.275 EndY=-0.275 EndZ=0
    g2: LineSegment StartX=0.275 StartY=-0.275 StartZ=0 EndX=-0.275 EndY=-0.275 EndZ=0
    g3: LineSegment StartX=-0.275 StartY=-0.275 StartZ=0 EndX=-0.275 EndY=0.275 EndZ=0
  constraints (10):
    c: Coincident(g0,g1)
    c: Coincident(g1,g2)
    c: Coincident(g2,g3)
    c: Coincident(g3,g0)
    c: Horizontal(g2)
    c: Vertical(g3)
    c: Symmetric(g1,g0,g-1)
    c: Symmetric(g0,g0,g-2)
    c: Equal(g0,g1)
    c: DistanceX(g0,g0) = 0.55
FEATURE [Sketcher::SketchObject] Sketch115  label="pin trj018"
  ArcFitTolerance = 0
  AttachmentSupport = -> [XZ_Plane056]
  FullyConstrained = true
  MakeInternals = false
  MapMode = 5
  Placement = pos=(0,0,0) rot=(1,0,0;1.5708rad)
  sketch-geometry (3):
    g0: LineSegment StartX=0.5 StartY=0 StartZ=0 EndX=10 EndY=0 EndZ=0
    g1: LineSegment StartX=0 StartY=-2.5 StartZ=0 EndX=0 EndY=-0.5 EndZ=0
    g2: ArcOfCircle CenterX=0.5 CenterY=-0.5 CenterZ=0 NormalX=0 NormalY=0 NormalZ=1 AngleXU=0 Radius=0.5 StartAngle=1.5708 EndAngle=3.14159
  constraints (9):
    c: Horizontal(g0)
    c: Vertical(g1)
    c: Tangent(g0,g2) = 1.5708
    c: Tangent(g1,g2) = 1.5708
    c: DistanceY(g1,g-1) = 2.5
    c: DistanceX(g-1,g0) = 10
    c: Radius(g2) = 0.5
    c: PointOnObject(g1,g-2)
    c: PointOnObject(g0,g-1)
FEATURE [Sketcher::SketchObject] Sketch116  label="pin trj019"
  ArcFitTolerance = 0
  AttachmentSupport = -> [XZ_Plane059]
  FullyConstrained = true
  MakeInternals = false
  MapMode = 5
  Placement = pos=(0,0,0) rot=(1,0,0;1.5708rad)
  sketch-geometry (3):
    g0: LineSegment StartX=0.5 StartY=0 StartZ=0 EndX=10 EndY=0 EndZ=0
    g1: LineSegment StartX=0 StartY=-2.5 StartZ=0 EndX=0 EndY=-0.5 EndZ=0
    g2: ArcOfCircle CenterX=0.5 CenterY=-0.5 CenterZ=0 NormalX=0 NormalY=0 NormalZ=1 AngleXU=0 Radius=0.5 StartAngle=1.5708 EndAngle=3.14159
  constraints (9):
    c: Horizontal(g0)
    c: Vertical(g1)
    c: Tangent(g0,g2) = 1.5708
    c: Tangent(g1,g2) = 1.5708
    c: DistanceY(g1,g-1) = 2.5
    c: DistanceX(g-1,g0) = 10
    c: Radius(g2) = 0.5
    c: PointOnObject(g1,g-2)
    c: PointOnObject(g0,g-1)
FEATURE [Sketcher::SketchObject] Sketch117
  ArcFitTolerance = 0
  AttachmentOffset = pos=(0,0,10) rot=(0,0,1;0rad)
  AttachmentSupport = -> [YZ_Plane052]
  FullyConstrained = true
  MakeInternals = false
  MapMode = 5
  Placement = pos=(10,0,0) rot=(0.57735,0.57735,0.57735;2.0944rad)
  sketch-geometry (2):
    g0: ArcOfCircle CenterX=0 CenterY=0 CenterZ=0 NormalX=0 NormalY=0 NormalZ=1 AngleXU=0 Radius=2.3 StartAngle=5.68249 EndAngle=10.0255
    g1: LineSegment StartX=1.89737 StartY=-1.3 StartZ=0 EndX=-1.89737 EndY=-1.3 EndZ=0
  constraints (6):
    c: Coincident(g1,g0)
    c: Coincident(g1,g0)
    c: Coincident(g0,g-1)
    c: Diameter(g0) = 4.6
    c: Distance(g0,g1) = 1.3
    c: Horizontal(g1)
FEATURE [PartDesign::Pad] Pad028
  Direction = (1,1,1)
  Length = 4.7
  Length2 = 100
  Placement = pos=(0,0,0) rot=(0.57735,0.57735,0.57735;2.0944rad)
  Profile = -> Sketch117
  Suppressed = false
  Type = 0
FEATURE [PartDesign::Body] Body050  label="DallasSensor006"
  AllowCompound = false
  Group = -> [Sketch117,Pad028]
  Origin = -> Origin058
  Tip = -> Pad028
FEATURE [Sketcher::SketchObject] Sketch118  label="pin trj020"
  ArcFitTolerance = 0
  AttachmentSupport = -> [XZ_Plane053]
  FullyConstrained = true
  MakeInternals = false
  MapMode = 5
  Placement = pos=(0,0,0) rot=(1,0,0;1.5708rad)
  sketch-geometry (3):
    g0: LineSegment StartX=0.5 StartY=0 StartZ=0 EndX=10 EndY=0 EndZ=0
    g1: LineSegment StartX=0 StartY=-2.5 StartZ=0 EndX=0 EndY=-0.5 EndZ=0
    g2: ArcOfCircle CenterX=0.5 CenterY=-0.5 CenterZ=0 NormalX=0 NormalY=0 NormalZ=1 AngleXU=0 Radius=0.5 StartAngle=1.5708 EndAngle=3.14159
  constraints (9):
    c: Horizontal(g0)
    c: Vertical(g1)
    c: Tangent(g0,g2) = 1.5708
    c: Tangent(g1,g2) = 1.5708
    c: DistanceY(g1,g-1) = 2.5
    c: DistanceX(g-1,g0) = 10
    c: Radius(g2) = 0.5
    c: PointOnObject(g1,g-2)
    c: PointOnObject(g0,g-1)
FEATURE [Sketcher::SketchObject] Sketch119  label="pin crs019"
  ArcFitTolerance = 0
  AttachmentOffset = pos=(0,0,-1) rot=(0,0,1;0rad)
  FullyConstrained = true
  MakeInternals = false
  MapMode = 5
  Placement = pos=(0,0,-1) rot=(0,0,1;0rad)
  sketch-geometry (4):
    g0: LineSegment StartX=-0.275 StartY=0.275 StartZ=0 EndX=0.275 EndY=0.275 EndZ=0
    g1: LineSegment StartX=0.275 StartY=0.275 StartZ=0 EndX=0.275 EndY=-0.275 EndZ=0
    g2: LineSegment StartX=0.275 StartY=-0.275 StartZ=0 EndX=-0.275 EndY=-0.275 EndZ=0
    g3: LineSegment StartX=-0.275 StartY=-0.275 StartZ=0 EndX=-0.275 EndY=0.275 EndZ=0
  constraints (10):
    c: Coincident(g0,g1)
    c: Coincident(g1,g2)
    c: Coincident(g2,g3)
    c: Coincident(g3,g0)
    c: Horizontal(g2)
    c: Vertical(g3)
    c: Symmetric(g1,g0,g-1)
    c: Symmetric(g0,g0,g-2)
    c: Equal(g0,g1)
    c: DistanceX(g0,g0) = 0.55
FEATURE [Sketcher::SketchObject] Sketch120  label="pin crs020"
  ArcFitTolerance = 0
  AttachmentOffset = pos=(0,0,-1) rot=(0,0,1;0rad)
  FullyConstrained = true
  MakeInternals = false
  MapMode = 5
  Placement = pos=(0,0,-1) rot=(0,0,1;0rad)
  sketch-geometry (4):
    g0: LineSegment StartX=-0.275 StartY=0.275 StartZ=0 EndX=0.275 EndY=0.275 EndZ=0
    g1: LineSegment StartX=0.275 StartY=0.275 StartZ=0 EndX=0.275 EndY=-0.275 EndZ=0
    g2: LineSegment StartX=0.275 StartY=-0.275 StartZ=0 EndX=-0.275 EndY=-0.275 EndZ=0
    g3: LineSegment StartX=-0.275 StartY=-0.275 StartZ=0 EndX=-0.275 EndY=0.275 EndZ=0
  constraints (10):
    c: Coincident(g0,g1)
    c: Coincident(g1,g2)
    c: Coincident(g2,g3)
    c: Coincident(g3,g0)
    c: Horizontal(g2)
    c: Vertical(g3)
    c: Symmetric(g1,g0,g-1)
    c: Symmetric(g0,g0,g-2)
    c: Equal(g0,g1)
    c: DistanceX(g0,g0) = 0.55
FEATURE [PartDesign::AdditivePipe] AdditivePipe021
  AuxilleryCurvelinear = true
  AuxillerySpineTangent = false
  Binormal = (0,0,0)
  Mode = 0
  Placement = pos=(0,0,-1) rot=(0,0,1;0rad)
  Profile = -> Sketch120
  Spine = -> Sketch118
  SpineTangent = false
  Suppressed = false
  Transformation = 0
  Transition = 0
FEATURE [PartDesign::Body] Body049  label="DallasPin020"
  AllowCompound = false
  Group = -> [Sketch118,Sketch120,AdditivePipe021]
  Origin = -> Origin056
  Placement = pos=(0,0,0) rot=(1,0,0;3.14159rad)
  Tip = -> AdditivePipe021
FEATURE [Sketcher::SketchObject] Sketch121  label="pin crs021"
  ArcFitTolerance = 0
  AttachmentOffset = pos=(0,0,-1) rot=(0,0,1;0rad)
  FullyConstrained = true
  MakeInternals = false
  MapMode = 5
  Placement = pos=(0,0,-1) rot=(0,0,1;0rad)
  sketch-geometry (4):
    g0: LineSegment StartX=-0.275 StartY=0.275 StartZ=0 EndX=0.275 EndY=0.275 EndZ=0
    g1: LineSegment StartX=0.275 StartY=0.275 StartZ=0 EndX=0.275 EndY=-0.275 EndZ=0
    g2: LineSegment StartX=0.275 StartY=-0.275 StartZ=0 EndX=-0.275 EndY=-0.275 EndZ=0
    g3: LineSegment StartX=-0.275 StartY=-0.275 StartZ=0 EndX=-0.275 EndY=0.275 EndZ=0
  constraints (10):
    c: Coincident(g0,g1)
    c: Coincident(g1,g2)
    c: Coincident(g2,g3)
    c: Coincident(g3,g0)
    c: Horizontal(g2)
    c: Vertical(g3)
    c: Symmetric(g1,g0,g-1)
    c: Symmetric(g0,g0,g-2)
    c: Equal(g0,g1)
    c: DistanceX(g0,g0) = 0.55
FEATURE [Sketcher::SketchObject] Sketch122  label="pin trj021"
  ArcFitTolerance = 0
  AttachmentSupport = -> [XZ_Plane054]
  FullyConstrained = true
  MakeInternals = false
  MapMode = 5
  Placement = pos=(0,0,0) rot=(1,0,0;1.5708rad)
  sketch-geometry (3):
    g0: LineSegment StartX=0.5 StartY=0 StartZ=0 EndX=10 EndY=0 EndZ=0
    g1: LineSegment StartX=0 StartY=-2.5 StartZ=0 EndX=0 EndY=-0.5 EndZ=0
    g2: ArcOfCircle CenterX=0.5 CenterY=-0.5 CenterZ=0 NormalX=0 NormalY=0 NormalZ=1 AngleXU=0 Radius=0.5 StartAngle=1.5708 EndAngle=3.14159
  constraints (9):
    c: Horizontal(g0)
    c: Vertical(g1)
    c: Tangent(g0,g2) = 1.5708
    c: Tangent(g1,g2) = 1.5708
    c: DistanceY(g1,g-1) = 2.5
    c: DistanceX(g-1,g0) = 10
    c: Radius(g2) = 0.5
    c: PointOnObject(g1,g-2)
    c: PointOnObject(g0,g-1)
FEATURE [PartDesign::AdditivePipe] AdditivePipe020
  AuxilleryCurvelinear = true
  AuxillerySpineTangent = false
  Binormal = (0,0,0)
  Mode = 0
  Placement = pos=(0,0,-1) rot=(0,0,1;0rad)
  Profile = -> Sketch119
  Spine = -> Sketch122
  SpineTangent = false
  Suppressed = false
  Transformation = 0
  Transition = 0
FEATURE [PartDesign::Body] Body048  label="DallasPin019"
  AllowCompound = false
  Group = -> [Sketch122,Sketch119,AdditivePipe020]
  Origin = -> Origin059
  Placement = pos=(0,1.27,0) rot=(1,0,0;3.14159rad)
  Tip = -> AdditivePipe020
FEATURE [Sketcher::SketchObject] Sketch123  label="pin trj022"
  ArcFitTolerance = 0
  AttachmentSupport = -> [XZ_Plane055]
  FullyConstrained = true
  MakeInternals = false
  MapMode = 5
  Placement = pos=(0,0,0) rot=(1,0,0;1.5708rad)
  sketch-geometry (3):
    g0: LineSegment StartX=0.5 StartY=0 StartZ=0 EndX=10 EndY=0 EndZ=0
    g1: LineSegment StartX=0 StartY=-2.5 StartZ=0 EndX=0 EndY=-0.5 EndZ=0
    g2: ArcOfCircle CenterX=0.5 CenterY=-0.5 CenterZ=0 NormalX=0 NormalY=0 NormalZ=1 AngleXU=0 Radius=0.5 StartAngle=1.5708 EndAngle=3.14159
  constraints (9):
    c: Horizontal(g0)
    c: Vertical(g1)
    c: Tangent(g0,g2) = 1.5708
    c: Tangent(g1,g2) = 1.5708
    c: DistanceY(g1,g-1) = 2.5
    c: DistanceX(g-1,g0) = 10
    c: Radius(g2) = 0.5
    c: PointOnObject(g1,g-2)
    c: PointOnObject(g0,g-1)
FEATURE [PartDesign::AdditivePipe] AdditivePipe022
  AuxilleryCurvelinear = true
  AuxillerySpineTangent = false
  Binormal = (0,0,0)
  Mode = 0
  Placement = pos=(0,0,-1) rot=(0,0,1;0rad)
  Profile = -> Sketch121
  Spine = -> Sketch123
  SpineTangent = false
  Suppressed = false
  Transformation = 0
  Transition = 0
FEATURE [PartDesign::Body] Body047  label="DallasPin018"
  AllowCompound = false
  Group = -> [Sketch123,Sketch121,AdditivePipe022]
  Origin = -> Origin057
  Placement = pos=(0,-1.27,0) rot=(1,0,0;3.14159rad)
  Tip = -> AdditivePipe022
FEATURE [App::LinkGroup] LinkGroup002
  ElementList = -> [Body050,Body049,Body048,Body047]
  LinkMode = 0
FEATURE [Sketcher::SketchObject] Sketch124  label="pin crs022"
  ArcFitTolerance = 0
  AttachmentOffset = pos=(0,0,-1) rot=(0,0,1;0rad)
  FullyConstrained = true
  MakeInternals = false
  MapMode = 5
  Placement = pos=(0,0,-1) rot=(0,0,1;0rad)
  sketch-geometry (4):
    g0: LineSegment StartX=-0.275 StartY=0.275 StartZ=0 EndX=0.275 EndY=0.275 EndZ=0
    g1: LineSegment StartX=0.275 StartY=0.275 StartZ=0 EndX=0.275 EndY=-0.275 EndZ=0
    g2: LineSegment StartX=0.275 StartY=-0.275 StartZ=0 EndX=-0.275 EndY=-0.275 EndZ=0
    g3: LineSegment StartX=-0.275 StartY=-0.275 StartZ=0 EndX=-0.275 EndY=0.275 EndZ=0
  constraints (10):
    c: Coincident(g0,g1)
    c: Coincident(g1,g2)
    c: Coincident(g2,g3)
    c: Coincident(g3,g0)
    c: Horizontal(g2)
    c: Vertical(g3)
    c: Symmetric(g1,g0,g-1)
    c: Symmetric(g0,g0,g-2)
    c: Equal(g0,g1)
    c: DistanceX(g0,g0) = 0.55
FEATURE [Sketcher::SketchObject] Sketch125
  ArcFitTolerance = 0
  AttachmentOffset = pos=(0,0,10) rot=(0,0,1;0rad)
  AttachmentSupport = -> [YZ_Plane056]
  FullyConstrained = true
  MakeInternals = false
  MapMode = 5
  Placement = pos=(10,0,0) rot=(0.57735,0.57735,0.57735;2.0944rad)
  sketch-geometry (2):
    g0: ArcOfCircle CenterX=0 CenterY=0 CenterZ=0 NormalX=0 NormalY=0 NormalZ=1 AngleXU=0 Radius=2.3 StartAngle=5.68249 EndAngle=10.0255
    g1: LineSegment StartX=1.89737 StartY=-1.3 StartZ=0 EndX=-1.89737 EndY=-1.3 EndZ=0
  constraints (6):
    c: Coincident(g1,g0)
    c: Coincident(g1,g0)
    c: Coincident(g0,g-1)
    c: Diameter(g0) = 4.6
    c: Distance(g0,g1) = 1.3
    c: Horizontal(g1)
FEATURE [Sketcher::SketchObject] Sketch126  label="pin crs023"
  ArcFitTolerance = 0
  AttachmentOffset = pos=(0,0,-1) rot=(0,0,1;0rad)
  FullyConstrained = true
  MakeInternals = false
  MapMode = 5
  Placement = pos=(0,0,-1) rot=(0,0,1;0rad)
  sketch-geometry (4):
    g0: LineSegment StartX=-0.275 StartY=0.275 StartZ=0 EndX=0.275 EndY=0.275 EndZ=0
    g1: LineSegment StartX=0.275 StartY=0.275 StartZ=0 EndX=0.275 EndY=-0.275 EndZ=0
    g2: LineSegment StartX=0.275 StartY=-0.275 StartZ=0 EndX=-0.275 EndY=-0.275 EndZ=0
    g3: LineSegment StartX=-0.275 StartY=-0.275 StartZ=0 EndX=-0.275 EndY=0.275 EndZ=0
  constraints (10):
    c: Coincident(g0,g1)
    c: Coincident(g1,g2)
    c: Coincident(g2,g3)
    c: Coincident(g3,g0)
    c: Horizontal(g2)
    c: Vertical(g3)
    c: Symmetric(g1,g0,g-1)
    c: Symmetric(g0,g0,g-2)
    c: Equal(g0,g1)
    c: DistanceX(g0,g0) = 0.55
FEATURE [Sketcher::SketchObject] Sketch127  label="pin trj023"
  ArcFitTolerance = 0
  AttachmentSupport = -> [XZ_Plane058]
  FullyConstrained = true
  MakeInternals = false
  MapMode = 5
  Placement = pos=(0,0,0) rot=(1,0,0;1.5708rad)
  sketch-geometry (3):
    g0: LineSegment StartX=0.5 StartY=0 StartZ=0 EndX=10 EndY=0 EndZ=0
    g1: LineSegment StartX=0 StartY=-2.5 StartZ=0 EndX=0 EndY=-0.5 EndZ=0
    g2: ArcOfCircle CenterX=0.5 CenterY=-0.5 CenterZ=0 NormalX=0 NormalY=0 NormalZ=1 AngleXU=0 Radius=0.5 StartAngle=1.5708 EndAngle=3.14159
  constraints (9):
    c: Horizontal(g0)
    c: Vertical(g1)
    c: Tangent(g0,g2) = 1.5708
    c: Tangent(g1,g2) = 1.5708
    c: DistanceY(g1,g-1) = 2.5
    c: DistanceX(g-1,g0) = 10
    c: Radius(g2) = 0.5
    c: PointOnObject(g1,g-2)
    c: PointOnObject(g0,g-1)
FEATURE [PartDesign::Pad] Pad029
  Direction = (1,1,1)
  Length = 4.7
  Length2 = 100
  Placement = pos=(0,0,0) rot=(0.57735,0.57735,0.57735;2.0944rad)
  Profile = -> Sketch125
  Suppressed = false
  Type = 0
FEATURE [PartDesign::AdditivePipe] AdditivePipe023
  AuxilleryCurvelinear = true
  AuxillerySpineTangent = false
  Binormal = (0,0,0)
  Mode = 0
  Placement = pos=(0,0,-1) rot=(0,0,1;0rad)
  Profile = -> Sketch126
  Spine = -> Sketch115
  SpineTangent = false
  Suppressed = false
  Transformation = 0
  Transition = 0
FEATURE [PartDesign::AdditivePipe] AdditivePipe024
  AuxilleryCurvelinear = true
  AuxillerySpineTangent = false
  Binormal = (0,0,0)
  Mode = 0
  Placement = pos=(0,0,-1) rot=(0,0,1;0rad)
  Profile = -> Sketch114
  Spine = -> Sketch116
  SpineTangent = false
  Suppressed = false
  Transformation = 0
  Transition = 0
FEATURE [PartDesign::AdditivePipe] AdditivePipe025
  AuxilleryCurvelinear = true
  AuxillerySpineTangent = false
  Binormal = (0,0,0)
  Mode = 0
  Placement = pos=(0,0,-1) rot=(0,0,1;0rad)
  Profile = -> Sketch124
  Spine = -> Sketch127
  SpineTangent = false
  Suppressed = false
  Transformation = 0
  Transition = 0
FEATURE [PartDesign::Body] Body051  label="DallasPin021"
  AllowCompound = false
  Group = -> [Sketch127,Sketch124,AdditivePipe025]
  Origin = -> Origin054
  Placement = pos=(0,0,0) rot=(1,0,0;3.14159rad)
  Tip = -> AdditivePipe025
FEATURE [PartDesign::Body] Body052  label="DallasPin022"
  AllowCompound = false
  Group = -> [Sketch115,Sketch126,AdditivePipe023]
  Origin = -> Origin052
  Placement = pos=(0,1.27,0) rot=(1,0,0;3.14159rad)
  Tip = -> AdditivePipe023
FEATURE [PartDesign::Body] Body053  label="DallasSensor007"
  AllowCompound = false
  Group = -> [Sketch125,Pad029]
  Origin = -> Origin055
  Tip = -> Pad029
FEATURE [PartDesign::Body] Body054  label="DallasPin023"
  AllowCompound = false
  Group = -> [Sketch116,Sketch114,AdditivePipe024]
  Origin = -> Origin053
  Placement = pos=(0,-1.27,0) rot=(1,0,0;3.14159rad)
  Tip = -> AdditivePipe024
FEATURE [App::LinkGroup] LinkGroup003
  ElementList = -> [Body053,Body051,Body052,Body054]
  LinkMode = 0
FEATURE [Part::Compound] Compound009  label="Dallas DS18B20_3"
  Links = -> [LinkGroup003]
  Placement = pos=(45,-16,-34.01) rot=(1,0,0;1.5708rad)
FEATURE [Part::Compound] Compound010  label="Dallas DS18B20_4"
  Links = -> [LinkGroup002]
  Placement = pos=(45,-16,31.99) rot=(1,0,0;1.5708rad)
FEATURE [Sketcher::SketchObject] Sketch128  label="fp sensor slot"
  ArcFitTolerance = 0
  AttachmentOffset = pos=(0,0,-60) rot=(0,0,1;0rad)
  AttachmentSupport = -> [YZ_Plane043]
  FullyConstrained = true
  MakeInternals = false
  MapMode = 5
  Placement = pos=(-60,0,0) rot=(0.57735,0.57735,0.57735;2.0944rad)
  sketch-geometry (4):
    g0: ArcOfCircle CenterX=-16 CenterY=-34 CenterZ=0 NormalX=0 NormalY=0 NormalZ=1 AngleXU=0 Radius=2.5 StartAngle=1.5708 EndAngle=4.71239
    g1: LineSegment StartX=-16 StartY=-31.5 StartZ=0 EndX=0 EndY=-31.5 EndZ=0
    g2: LineSegment StartX=0 StartY=-31.5 StartZ=0 EndX=0 EndY=-36.5 EndZ=0
    g3: LineSegment StartX=0 StartY=-36.5 StartZ=0 EndX=-16 EndY=-36.5 EndZ=0
  constraints (11):
    c: Coincident(g1,g2)
    c: Coincident(g2,g3)
    c: Horizontal(g1)
    c: Horizontal(g3)
    c: Vertical(g2)
    c: DistanceX(g0) = -16
    c: DistanceY(g0) = -34
    c: Tangent(g0,g1) = 1.5708
    c: Tangent(g0,g3) = 1.5708
    c: Radius(g0) = 2.5
    c: PointOnObject(g1,g-2)
FEATURE [PartDesign::Mirrored] Mirrored017
  MirrorPlane = -> YZ_Plane043
  Suppressed = false
  TransformMode = 0
FEATURE [PartDesign::Mirrored] Mirrored018
  MirrorPlane = -> DatumPlane001
  Suppressed = false
  TransformMode = 0
FEATURE [Sketcher::SketchObject] Sketch129  label="fp vent crs"
  ArcFitTolerance = 0
  AttachmentOffset = pos=(0,0,-34) rot=(0,0,1;0rad)
  AttachmentSupport = -> [XY_Plane043]
  FullyConstrained = true
  MakeInternals = false
  MapMode = 5
  Placement = pos=(0,0,-34) rot=(0,0,1;0rad)
  sketch-geometry (8):
    g0: ArcOfCircle CenterX=-59.3 CenterY=-17 CenterZ=0 NormalX=0 NormalY=0 NormalZ=1 AngleXU=0 Radius=0.7 StartAngle=-1.78e-14 EndAngle=3.14159
    g1: LineSegment StartX=-60 StartY=-17 StartZ=0 EndX=-60 EndY=-26 EndZ=0
    g2: LineSegment StartX=-58.6 StartY=-17 StartZ=0 EndX=-58.6 EndY=-25 EndZ=0
    g3: LineSegment StartX=-55.2 StartY=-26 StartZ=0 EndX=-60 EndY=-26 EndZ=0
    g4: ArcOfCircle CenterX=-55.9 CenterY=-17 CenterZ=0 NormalX=0 NormalY=0 NormalZ=1 AngleXU=0 Radius=0.7 StartAngle=4e-16 EndAngle=3.14159
    g5: LineSegment StartX=-56.6 StartY=-17 StartZ=0 EndX=-56.6 EndY=-25 EndZ=0
    g6: LineSegment StartX=-55.2 StartY=-17 StartZ=0 EndX=-55.2 EndY=-26 EndZ=0
    g7: LineSegment StartX=-58.6 StartY=-25 StartZ=0 EndX=-56.6 EndY=-25 EndZ=0
  constraints (22):
    c: Tangent(g0,g2) = 1.5708
    c: Tangent(g0,g1) = -1.5708
    c: Vertical(g1)
    c: DistanceX(g0,g0) = 1.4
    c: DistanceX(g0,g-1) = 60
    c: Coincident(g3,g1)
    c: Horizontal(g3)
    c: Vertical(g2)
    c: DistanceY(g3,g-1) = 26
    c: DistanceY(g1,g1) = 9
    c: Tangent(g4,g6) = 1.5708
    c: Tangent(g4,g5) = -1.5708
    c: Vertical(g5)
    c: Vertical(g6)
    c: Equal(g0,g4)
    c: DistanceX(g0,g4) = 2
    c: Horizontal(g7)
    c: Coincident(g3,g6)
    c: Coincident(g2,g7)
    c: Coincident(g5,g7)
    c: DistanceY(g3,g5) = 1
    c: Equal(g6,g1)
FEATURE [Sketcher::SketchObject] Sketch130  label="fp vent trj"
  ArcFitTolerance = 0
  AttachmentOffset = pos=(0,0,-60) rot=(0,0,1;0rad)
  AttachmentSupport = -> [YZ_Plane043]
  FullyConstrained = true
  MakeInternals = false
  MapMode = 5
  Placement = pos=(-60,0,0) rot=(0.57735,0.57735,0.57735;2.0944rad)
  sketch-geometry (2):
    g0: ArcOfCircle CenterX=-32 CenterY=-34 CenterZ=0 NormalX=0 NormalY=0 NormalZ=1 AngleXU=0 Radius=16 StartAngle=1e-16 EndAngle=1.31812
    g1: LineSegment StartX=-16 StartY=-34 StartZ=0 EndX=-16 EndY=-50 EndZ=0
  constraints (7):
    c: DistanceX(g0,g-1) = 16
    c: DistanceY(g0,g-1) = 34
    c: Vertical(g1)
    c: DistanceY(g1,g1) = 16
    c: Radius(g0) = 16
    c: DistanceX(g0,g0) = 12
    c: Tangent(g1,g0) = 1.5708
FEATURE [Sketcher::SketchObject] Sketch131  label="fp notch for PCB"
  ArcFitTolerance = 0
  AttachmentSupport = -> [XY_Plane043]
  FullyConstrained = true
  MakeInternals = false
  MapMode = 5
  sketch-geometry (5):
    g0: LineSegment StartX=-47 StartY=-17.9 StartZ=0 EndX=-49.5 EndY=-17.9 EndZ=0
    g1: LineSegment StartX=-49.5 StartY=-17.9 StartZ=0 EndX=-49.5 EndY=-19.7 EndZ=0
    g2: LineSegment StartX=-49.5 StartY=-19.7 StartZ=0 EndX=-44 EndY=-19.7 EndZ=0
    g3: LineSegment StartX=-44 StartY=-19.7 StartZ=0 EndX=-44 EndY=-16.1679 EndZ=0
    g4: LineSegment StartX=-44 StartY=-16.1679 StartZ=0 EndX=-47 EndY=-17.9 EndZ=0
  constraints (15):
    c: Coincident(g0,g1)
    c: Coincident(g1,g2)
    c: Coincident(g2,g3)
    c: Horizontal(g0)
    c: Horizontal(g2)
    c: Vertical(g1)
    c: Vertical(g3)
    c: Coincident(g0,g4)
    c: Coincident(g4,g3)
    c: DistanceY(g0,g-1) = 17.9
    c: DistanceX(g0,g-1) = 47
    c: Angle(g4,g0) = 2.61799
    c: DistanceX(g4,g4) = 3
    c: DistanceY(g1,g-1) = 19.7
    c: DistanceX(g0,g-1) = 49.5
FEATURE [Sketcher::SketchObject] Sketch132  label="fp pocket for IsoTherm"
  ArcFitTolerance = 0
  AttachmentOffset = pos=(0,0,27) rot=(0,0,1;0rad)
  AttachmentSupport = -> [XZ_Plane043]
  ExternalGeometry = -> [Sketch081,Pocket015]
  FullyConstrained = true
  MakeInternals = false
  MapMode = 5
  Placement = pos=(0,-27,6e-15) rot=(1,0,0;1.5708rad)
  sketch-geometry (12):
    g0: LineSegment StartX=42 StartY=-14 StartZ=0 EndX=42 EndY=-36.5 EndZ=0
    g1: ArcOfCircle CenterX=40 CenterY=-14 CenterZ=0 NormalX=0 NormalY=0 NormalZ=1 AngleXU=0 Radius=2 StartAngle=2e-16 EndAngle=1.21772
    g2: ArcOfCircle CenterX=40 CenterY=-36.5 CenterZ=0 NormalX=0 NormalY=0 NormalZ=1 AngleXU=0 Radius=2 StartAngle=4.71239 EndAngle=6.28319
    g3: ArcOfCircle CenterX=-32 CenterY=-24.5 CenterZ=0 NormalX=0 NormalY=0 NormalZ=1 AngleXU=0 Radius=14 StartAngle=3.14159 EndAngle=4.71239
    g4: ArcOfCircle CenterX=-32 CenterY=26 CenterZ=0 NormalX=0 NormalY=0 NormalZ=1 AngleXU=0 Radius=14 StartAngle=1.5708 EndAngle=3.14159
    g5: ArcOfCircle CenterX=28 CenterY=32 CenterZ=0 NormalX=0 NormalY=0 NormalZ=1 AngleXU=0 Radius=8 StartAngle=4e-16 EndAngle=1.5708
    g6: LineSegment StartX=-32 StartY=40 StartZ=0 EndX=28 EndY=40 EndZ=0
    g7: LineSegment StartX=-46 StartY=26 StartZ=0 EndX=-46 EndY=-24.5 EndZ=0
    g8: LineSegment StartX=36 StartY=32 StartZ=0 EndX=36 EndY=-9 EndZ=0
    g9: LineSegment StartX=40 StartY=-38.5 StartZ=0 EndX=-32 EndY=-38.5 EndZ=0
    g10: ArcOfCircle CenterX=38 CenterY=-9 CenterZ=0 NormalX=0 NormalY=0 NormalZ=1 AngleXU=0 Radius=2 StartAngle=3.14159 EndAngle=4.35931
    g11: LineSegment StartX=37.3084 StartY=-10.8766 StartZ=0 EndX=40.6916 EndY=-12.1234 EndZ=0
  constraints (28):
    c: Vertical(g0)
    c: Tangent(g0,g1) = 1.5708
    c: Tangent(g0,g2) = 1.5708
    c: Radius(g1) = 2
    c: Coincident(g4,g-3)
    c: Coincident(g5,g-5)
    c: Horizontal(g6)
    c: Tangent(g5,g6) = 1.5708
    c: Tangent(g4,g6) = 1.5708
    c: Vertical(g7)
    c: Tangent(g4,g7) = -1.5708
    c: Tangent(g3,g7) = -1.5708
    c: Vertical(g8)
    c: Tangent(g5,g8) = 1.5708
    c: Equal(g2,g1)
    c: Equal(g-4,g3)
    c: DistanceX(g0) = 42
    c: Horizontal(g9)
    c: DistanceY(g9,g-1) = 38.5
    c: Tangent(g2,g9) = 1.5708
    c: DistanceY(g1,g-1) = 14
    c: Tangent(g9,g3) = 1.5708
    c: Equal(g4,g-3)
    c: Tangent(g1,g11) = 1.5708
    c: Tangent(g10,g11) = -1.5708
    c: Tangent(g8,g10) = -1.5708
    c: DistanceY(g8,g-1) = 9
    c: Equal(g1,g10)
FEATURE [Sketcher::SketchObject] Sketch134
  ArcFitTolerance = 0
  AttachmentSupport = -> [XZ_Plane060]
  FullyConstrained = false
  MakeInternals = false
  MapMode = 5
  Placement = pos=(0,0,0) rot=(1,0,0;1.5708rad)
  sketch-geometry (5):
    g0: LineSegment StartX=3.2 StartY=2.75 StartZ=0 EndX=5 EndY=2.75 EndZ=0
    g1: LineSegment StartX=5 StartY=2.75 StartZ=0 EndX=5 EndY=0 EndZ=0
    g2: LineSegment StartX=5 StartY=0 StartZ=0 EndX=1.5 EndY=0 EndZ=0
    g3: LineSegment StartX=1.5 StartY=0 StartZ=0 EndX=1.5 EndY=1.05 EndZ=0
    g4: LineSegment StartX=3.2 StartY=2.75 StartZ=0 EndX=1.5 EndY=1.05 EndZ=0
  constraints (15):
    c: Coincident(g0,g1)
    c: Coincident(g1,g2)
    c: Coincident(g2,g3)
    c: Horizontal(g0)
    c: Horizontal(g2)
    c: Vertical(g1)
    c: Vertical(g3)
    c: PointOnObject(g1,g-1)
    c: DistanceX(g1) = 5
    c: Coincident(g0,g4)
    c: Coincident(g4,g3)
    c: DistanceY(g0) = 2.75
    c: DistanceX(g2) = 1.5
    c: Angle(g3,g4) = 2.35619
    c: DistanceX(g0) = 3.2
FEATURE [PartDesign::Revolution] Revolution004
  Angle = 360
  Angle2 = 60
  Axis = (-3e-16,3e-16,1)
  Base = (0,0,0)
  Placement = pos=(0,0,0) rot=(1,0,0;1.5708rad)
  Profile = -> Sketch134
  ReferenceAxis = -> Z_Axis018
  Reversed = true
  Suppressed = false
  Type = 0
FEATURE [PartDesign::Body] Body055  label="RingMagnet10x2.75_3"
  AllowCompound = false
  Group = -> [Sketch134,Revolution004]
  Origin = -> Origin060
  Placement = pos=(-56,-4,22) rot=(1,0,0;1.5708rad)
  Tip = -> Revolution004
FEATURE [Sketcher::SketchObject] Sketch135
  ArcFitTolerance = 0
  AttachmentSupport = -> [XZ_Plane061]
  FullyConstrained = false
  MakeInternals = false
  MapMode = 5
  Placement = pos=(0,0,0) rot=(1,0,0;1.5708rad)
  sketch-geometry (5):
    g0: LineSegment StartX=3.2 StartY=2.75 StartZ=0 EndX=5 EndY=2.75 EndZ=0
    g1: LineSegment StartX=5 StartY=2.75 StartZ=0 EndX=5 EndY=0 EndZ=0
    g2: LineSegment StartX=5 StartY=0 StartZ=0 EndX=1.5 EndY=0 EndZ=0
    g3: LineSegment StartX=1.5 StartY=0 StartZ=0 EndX=1.5 EndY=1.05 EndZ=0
    g4: LineSegment StartX=3.2 StartY=2.75 StartZ=0 EndX=1.5 EndY=1.05 EndZ=0
  constraints (15):
    c: Coincident(g0,g1)
    c: Coincident(g1,g2)
    c: Coincident(g2,g3)
    c: Horizontal(g0)
    c: Horizontal(g2)
    c: Vertical(g1)
    c: Vertical(g3)
    c: PointOnObject(g1,g-1)
    c: DistanceX(g1) = 5
    c: Coincident(g0,g4)
    c: Coincident(g4,g3)
    c: DistanceY(g0) = 2.75
    c: DistanceX(g2) = 1.5
    c: Angle(g3,g4) = 2.35619
    c: DistanceX(g0) = 3.2
FEATURE [PartDesign::Revolution] Revolution005
  Angle = 360
  Angle2 = 60
  Axis = (-3e-16,3e-16,1)
  Base = (0,0,0)
  Placement = pos=(0,0,0) rot=(1,0,0;1.5708rad)
  Profile = -> Sketch135
  ReferenceAxis = -> Z_Axis018
  Reversed = true
  Suppressed = false
  Type = 0
FEATURE [PartDesign::Body] Body056  label="RingMagnet10x2.75_4"
  AllowCompound = false
  Group = -> [Sketch135,Revolution005]
  Origin = -> Origin061
  Placement = pos=(-56,-13.45,22) rot=(1,0,0;1.5708rad)
  Tip = -> Revolution005
FEATURE [PartDesign::Fillet] Fillet003  label="FP Button hole fillet 1"
  Base = -> LinearPattern003 [Edge43,Edge42,Edge41]
  BaseFeature = -> LinearPattern003
  Radius = 1
  SupportTransform = false
  Suppressed = false
  UseAllEdges = false
FEATURE [PartDesign::Pocket] Pocket022  label="FP First vent hole ESP"
  BaseFeature = -> Fillet003
  Direction = (0,0,-1)
  Length = 5
  Length2 = 100
  Profile = -> Sketch099
  Suppressed = false
  Type = 1
FEATURE [PartDesign::MultiTransform] MultiTransform  label="FP Other vent holes"
  BaseFeature = -> Pocket022
  Originals = -> [Pocket022]
  Suppressed = false
  TransformMode = 0
  Transformations = -> [LinearPattern004,Mirrored]
FEATURE [PartDesign::Pocket] Pocket023  label="FP Sensor slot"
  BaseFeature = -> MultiTransform
  Direction = (-1,2e-16,-3e-16)
  Length = 18
  Length2 = 100
  Profile = -> Sketch128
  Reversed = true
  Suppressed = false
  Type = 0
FEATURE [PartDesign::MultiTransform] MultiTransform004  label="FP Other sensors"
  BaseFeature = -> Pocket023
  Originals = -> [Pocket023]
  Suppressed = false
  TransformMode = 0
  Transformations = -> [Mirrored017,Mirrored018]
FEATURE [PartDesign::SubtractivePipe] SubtractivePipe004  label="FP Sensor vent hole sensor"
  AuxilleryCurvelinear = true
  AuxillerySpineTangent = false
  BaseFeature = -> MultiTransform004
  Binormal = (0,0,0)
  Mode = 0
  Profile = -> Sketch129
  Spine = -> Sketch130
  SpineTangent = false
  Suppressed = false
  Transformation = 0
  Transition = 0
FEATURE [Part::Feature] Part__Feature006  label="Interconnect PCB PCB"
  shape: bbox 96 x 75 x 1.6 mm, 115 faces (baked)
FEATURE [App::Part] InterconnectPCB_1  label="InterconnectPCB 1"
  Group = -> [Part__Feature006]
  Origin = -> Origin062
  Placement = pos=(0,-18,-4e-15) rot=(1,0,0;1.5708rad)
FEATURE [App::DocumentObjectGroup] Group  label="Electronics"
  Group = -> [Screw001,Compound,Compound006,Screw,Screw002,Nut,Nut001,Nut002,Compound005,Compound004,Compound007,Compound008,Compound009,Compound010,Part,InterconnectPCB_1]
FEATURE [PartDesign::Mirrored] Mirrored019
  MirrorPlane = -> YZ_Plane043
  Suppressed = false
  TransformMode = 0
FEATURE [PartDesign::MultiTransform] MultiTransform005  label="FP Other vent holes sensors"
  BaseFeature = -> SubtractivePipe004
  Originals = -> [SubtractivePipe004]
  Suppressed = false
  TransformMode = 0
  Transformations = -> [Mirrored019]
FEATURE [PartDesign::Pocket] Pocket024  label="FP Notch for PCB"
  BaseFeature = -> MultiTransform005
  Direction = (0,0,-1)
  Length = 7
  Length2 = 100
  Midplane = true
  Profile = -> Sketch131
  Suppressed = false
  Type = 0
FEATURE [PartDesign::Pocket] Pocket025  label="FP Pocket for IsoTherm"
  BaseFeature = -> Pocket024
  Direction = (0,1,2e-16)
  Length = 5
  Length2 = 100
  Profile = -> Sketch132
  Suppressed = false
  Type = 1
FEATURE [Sketcher::SketchObject] Sketch136  label="wp large inner cavity"
  ArcFitTolerance = 0
  AttachmentOffset = pos=(0,0,2) rot=(0,0,1;0rad)
  AttachmentSupport = -> [XZ_Plane018]
  ExternalGeometry = -> [Sketch027,Sketch085,Sketch088]
  FullyConstrained = true
  MakeInternals = false
  MapMode = 5
  Placement = pos=(0,-2,4e-16) rot=(1,0,0;1.5708rad)
  sketch-geometry (20):
    g0: LineSegment StartX=-48 StartY=-25.1761 StartZ=0 EndX=-48 EndY=-17.8819 EndZ=0
    g1: ArcOfCircle CenterX=-6.23e-14 CenterY=-252.5 CenterZ=0 NormalX=0 NormalY=0 NormalZ=1 AngleXU=0 Radius=292 StartAngle=1.44187 EndAngle=1.69972
    g2: ArcOfCircle CenterX=3.11e-14 CenterY=252.5 CenterZ=0 NormalX=0 NormalY=0 NormalZ=1 AngleXU=0 Radius=292 StartAngle=4.58346 EndAngle=4.84132
    g3: ArcOfCircle CenterX=-36 CenterY=-25.1761 CenterZ=0 NormalX=0 NormalY=0 NormalZ=1 AngleXU=0 Radius=12 StartAngle=3.14159 EndAngle=4.58346
    g4: ArcOfCircle CenterX=36 CenterY=-25.1761 CenterZ=0 NormalX=0 NormalY=0 NormalZ=1 AngleXU=0 Radius=12 StartAngle=4.84132 EndAngle=5.99738
    g5: ArcOfCircle CenterX=-36 CenterY=25.1761 CenterZ=0 NormalX=0 NormalY=0 NormalZ=1 AngleXU=0 Radius=12 StartAngle=1.69972 EndAngle=3.14159
    g6: ArcOfCircle CenterX=36 CenterY=25.1761 CenterZ=0 NormalX=0 NormalY=0 NormalZ=1 AngleXU=0 Radius=12 StartAngle=6.2536 EndAngle=7.72505
    g7: ArcOfCircle CenterX=-44 CenterY=-1 CenterZ=0 NormalX=0 NormalY=0 NormalZ=1 AngleXU=0 Radius=11 StartAngle=4.83031 EndAngle=7.73606
    g8: ArcOfCircle CenterX=50 CenterY=10 CenterZ=0 NormalX=0 NormalY=0 NormalZ=1 AngleXU=0 Radius=11 StartAngle=2.06093 EndAngle=3.14159
    g9: ArcOfCircle CenterX=50 CenterY=-12 CenterZ=0 NormalX=0 NormalY=0 NormalZ=1 AngleXU=0 Radius=11 StartAngle=3.14159 EndAngle=4.20613
    g10: LineSegment StartX=-48 StartY=15.8819 StartZ=0 EndX=-48 EndY=25.1761 EndZ=0
    g11: ArcOfCircle CenterX=-42 CenterY=15.8819 CenterZ=0 NormalX=0 NormalY=0 NormalZ=1 AngleXU=0 Radius=6 StartAngle=3.14159 EndAngle=4.59447
    g12: ArcOfCircle CenterX=-42 CenterY=-17.8819 CenterZ=0 NormalX=0 NormalY=0 NormalZ=1 AngleXU=0 Radius=6 StartAngle=1.68872 EndAngle=3.14159
    g13: ArcOfCircle CenterX=41.9974 CenterY=24.9986 CenterZ=0 NormalX=0 NormalY=0 NormalZ=1 AngleXU=0 Radius=6 StartAngle=5.20252 EndAngle=6.2536
    g14: ArcOfCircle CenterX=41.7566 CenterY=-26.8676 CenterZ=0 NormalX=0 NormalY=0 NormalZ=1 AngleXU=0 Radius=6 StartAngle=5.99738 EndAngle=7.34773
    g15: LineSegment StartX=39 StartY=10 StartZ=0 EndX=39 EndY=-12 EndZ=0
    g16: LineSegment [constr] StartX=36 StartY=25.1761 StartZ=0 EndX=-36 EndY=25.1761 EndZ=0
    g17: LineSegment [constr] StartX=-36 StartY=25.1761 StartZ=0 EndX=-36 EndY=-25.1761 EndZ=0
    g18: LineSegment [constr] StartX=-36 StartY=-25.1761 StartZ=0 EndX=36 EndY=-25.1761 EndZ=0
    g19: LineSegment [constr] StartX=36 StartY=-25.1761 StartZ=0 EndX=36 EndY=25.1761 EndZ=0
  constraints (48):
    c: Vertical(g0)
    c: Coincident(g1,g-3)
    c: Coincident(g2,g-4)
    c: Radius(g1) = 292
    c: Equal(g2,g1)
    c: Tangent(g2,g3) = -1.5708
    c: Tangent(g0,g3) = 1.5708
    c: Tangent(g2,g4) = -1.5708
    c: Tangent(g1,g5) = -1.5708
    c: Tangent(g1,g6) = -1.5708
    c: Equal(g6,g4)
    c: Equal(g4,g3)
    c: Symmetric(g5,g6,g-2)
    c: Radius(g6) = 12
    c: Coincident(g7,g-7)
    c: Coincident(g8,g-5)
    c: Coincident(g9,g-6)
    c: Tangent(g0,g10)
    c: Radius(g7) = 11
    c: Tangent(g7,g11) = 1.5708
    c: Tangent(g10,g11) = 1.5708
    c: Tangent(g7,g12) = 1.5708
    c: Tangent(g0,g12) = 1.5708
    c: Tangent(g8,g13) = 1.5708
    c: Equal(g8,g9)
    c: Equal(g9,g7)
    c: Tangent(g9,g14) = 1.5708
    c: Equal(g14,g13)
    c: Equal(g13,g11)
    c: Equal(g11,g12)
    c: Tangent(g9,g15) = -1.5708
    c: Tangent(g8,g15) = -1.5708
    c: Tangent(g5,g10) = 1.5708
    c: Tangent(g4,g14) = -1.5708
    c: Tangent(g6,g13) = -1.5708
    c: Radius(g14) = 6
    c: DistanceX(g5,g-1) = 48
    c: Coincident(g16,g17)
    c: Coincident(g17,g18)
    c: Coincident(g18,g19)
    c: Coincident(g19,g16)
    c: Horizontal(g16)
    c: Horizontal(g18)
    c: Vertical(g17)
    c: Coincident(g16,g6)
    c: Coincident(g4,g18)
    c: Coincident(g3,g17)
    c: Coincident(g5,g16)
FEATURE [PartDesign::Pocket] Pocket027  label="WP Large inner cavity"
  BaseFeature = -> Pocket020
  Direction = (0,1,2e-16)
  Length = 5
  Length2 = 100
  Midplane = true
  Profile = -> Sketch136
  Reversed = true
  Suppressed = false
  Type = 1
FEATURE [Sketcher::SketchObject] Sketch137  label="wp chamfer inner fr crs"
  ArcFitTolerance = 0
  AttachmentOffset = pos=(0,0,-22) rot=(0,0,1;0rad)
  AttachmentSupport = -> [XY_Plane018]
  FullyConstrained = true
  MakeInternals = false
  MapMode = 5
  Placement = pos=(0,0,-22) rot=(0,0,1;0rad)
  sketch-geometry (3):
    g0: LineSegment StartX=-47.9 StartY=-7.9 StartZ=0 EndX=-49.1 EndY=-9.1 EndZ=0
    g1: LineSegment StartX=-49.1 StartY=-9.1 StartZ=0 EndX=-47.9 EndY=-9.1 EndZ=0
    g2: LineSegment StartX=-47.9 StartY=-9.1 StartZ=0 EndX=-47.9 EndY=-7.9 EndZ=0
  constraints (9):
    c: Coincident(g0,g1)
    c: Horizontal(g1)
    c: Coincident(g1,g2)
    c: Coincident(g2,g0)
    c: Vertical(g2)
    c: Equal(g1,g2)
    c: DistanceY(g2,g2) = 1.2
    c: DistanceX(g1,g-1) = 47.9
    c: DistanceY(g1,g-1) = 9.1
FEATURE [PartDesign::SubtractivePipe] SubtractivePipe005  label="WP Chamfer inner front"
  AuxilleryCurvelinear = true
  AuxillerySpineTangent = false
  BaseFeature = -> Pocket027
  Binormal = (0,0,0)
  Mode = 0
  Profile = -> Sketch137
  Spine = -> Sketch136
  SpineTangent = false
  Suppressed = false
  Transformation = 0
  Transition = 0
FEATURE [Sketcher::SketchObject] Sketch138  label="wp chamfer inner bck crs"
  ArcFitTolerance = 0
  AttachmentOffset = pos=(0,0,-22) rot=(0,0,1;0rad)
  AttachmentSupport = -> [XY_Plane018]
  FullyConstrained = true
  MakeInternals = false
  MapMode = 5
  Placement = pos=(0,0,-22) rot=(0,0,1;0rad)
  sketch-geometry (3):
    g0: LineSegment StartX=-47.9 StartY=-1.9 StartZ=0 EndX=-49.9 EndY=0.1 EndZ=0
    g1: LineSegment StartX=-49.9 StartY=0.1 StartZ=0 EndX=-47.9 EndY=0.1 EndZ=0
    g2: LineSegment StartX=-47.9 StartY=0.1 StartZ=0 EndX=-47.9 EndY=-1.9 EndZ=0
  constraints (9):
    c: Coincident(g0,g1)
    c: Horizontal(g1)
    c: Coincident(g1,g2)
    c: Coincident(g2,g0)
    c: Vertical(g2)
    c: DistanceX(g1,g-1) = 47.9
    c: DistanceY(g1,g-1) = -0.1
    c: DistanceY(g2,g2) = -2
    c: Equal(g2,g1)
FEATURE [PartDesign::SubtractivePipe] SubtractivePipe006  label="WP Chamfer inner back"
  AuxilleryCurvelinear = true
  AuxillerySpineTangent = false
  BaseFeature = -> SubtractivePipe005
  Binormal = (0,0,0)
  Mode = 0
  Profile = -> Sketch138
  Spine = -> Sketch136
  SpineTangent = false
  Suppressed = false
  Transformation = 0
  Transition = 0
FEATURE [Sketcher::SketchObject] Sketch139
  ArcFitTolerance = 0
  AttachmentSupport = -> [XZ_Plane043]
  FullyConstrained = false
  MakeInternals = false
  MapMode = 5
  Placement = pos=(0,0,0) rot=(1,0,0;1.5708rad)
  sketch-geometry (5):
    g0: LineSegment StartX=-54 StartY=22 StartZ=0 EndX=79.075 EndY=22 EndZ=0
    g1: LineSegment StartX=79.075 StartY=22 StartZ=0 EndX=79.075 EndY=-53.9496 EndZ=0
    g2: LineSegment StartX=79.075 StartY=-53.9496 StartZ=0 EndX=-56 EndY=-53.9496 EndZ=0
    g3: LineSegment StartX=-56 StartY=-53.9496 StartZ=0 EndX=-56 EndY=20 EndZ=0
    g4: ArcOfCircle CenterX=-54 CenterY=20 CenterZ=0 NormalX=0 NormalY=0 NormalZ=1 AngleXU=0 Radius=2 StartAngle=1.5708 EndAngle=3.14159
  constraints (12):
    c: Coincident(g0,g1)
    c: Coincident(g1,g2)
    c: Coincident(g2,g3)
    c: Horizontal(g0)
    c: Horizontal(g2)
    c: Vertical(g1)
    c: Vertical(g3)
    c: Tangent(g3,g4) = 1.5708
    c: Tangent(g0,g4) = 1.5708
    c: DistanceY(g0) = 22
    c: Radius(g4) = 2
    c: DistanceX(g3) = -56
FEATURE [Sketcher::SketchObject] Sketch140  label="fp remove groove right"
  ArcFitTolerance = 0
  AttachmentOffset = pos=(0,0,12.5) rot=(0,0,1;0rad)
  AttachmentSupport = -> [XZ_Plane043]
  ExternalGeometry = -> [Sketch071]
  FullyConstrained = true
  MakeInternals = false
  MapMode = 5
  Placement = pos=(0,-12.5,2.8e-15) rot=(1,0,0;1.5708rad)
  sketch-geometry (5):
    g0: ArcOfCircle CenterX=-2.3e-15 CenterY=-252.5 CenterZ=0 NormalX=0 NormalY=0 NormalZ=1 AngleXU=0 Radius=295.5 StartAngle=1.39005 EndAngle=1.50098
    g1: ArcOfCircle CenterX=-2.3e-15 CenterY=-252.5 CenterZ=0 NormalX=0 NormalY=0 NormalZ=1 AngleXU=0 Radius=290.9 StartAngle=1.35804 EndAngle=1.50098
    g2: LineSegment StartX=20.2922 StartY=37.6914 StartZ=0 EndX=20.613 EndY=42.2802 EndZ=0
    g3: LineSegment [constr] StartX=51.0529 StartY=26.8736 StartZ=0 EndX=53.9291 EndY=42.6129 EndZ=0
    g4: ArcOfCircle CenterX=51.0529 CenterY=26.8736 CenterZ=0 NormalX=0 NormalY=0 NormalZ=1 AngleXU=0 Radius=11.5 StartAngle=0.446654 EndAngle=1.39005
  constraints (14):
    c: Coincident(g0,g-3)
    c: Coincident(g1,g0)
    c: Coincident(g2,g1)
    c: Coincident(g2,g0)
    c: PointOnObject(g0,g2)
    c: Radius(g0) = 295.5
    c: Angle(g2,g-2) = 0.0698132
    c: Coincident(g3,g-4)
    c: Coincident(g3,g-4)
    c: PointOnObject(g0,g3)
    c: Coincident(g4,g3)
    c: Coincident(g4,g0)
    c: Coincident(g1,g4)
    c: Distance(g2) = 4.6
FEATURE [PartDesign::Pocket] Pocket029  label="FP Remove groove right"
  BaseFeature = -> Pocket025
  Direction = (0,1,2e-16)
  Length = 5
  Length2 = 100
  Profile = -> Sketch140
  Suppressed = false
  Type = 1
FEATURE [PartDesign::Mirrored] Mirrored020
  MirrorPlane = -> XY_Plane043
  Suppressed = false
  TransformMode = 0
FEATURE [PartDesign::Mirrored] Mirrored021
  MirrorPlane = -> YZ_Plane043
  Suppressed = false
  TransformMode = 0
FEATURE [PartDesign::MultiTransform] MultiTransform006  label="FP Remove other sections of groove"
  BaseFeature = -> Pocket029
  Originals = -> [Pocket029]
  Suppressed = false
  TransformMode = 0
  Transformations = -> [Mirrored020,Mirrored021]
FEATURE [PartDesign::Pocket] Pocket028
  BaseFeature = -> MultiTransform006
  Direction = (0,1,2e-16)
  Length = 5
  Length2 = 100
  Midplane = true
  Profile = -> Sketch139
  Suppressed = false
  Type = 1
FEATURE [PartDesign::Body] Body038  label="Front panel"
  AllowCompound = false
  Group = -> [Sketch071,Sketch070,Pad025,Sketch072,SubtractivePipe001,Fillet002,Sketch073,DatumPlane001,Sketch077,Groove003,MultiTransform003,Mirrored016,Mirrored014,Sketch078,Sketch079,Pocket011,Pocket010,Pocket013,Sketch080,Pocket014,Sketch081,Pocket015,Sketch082,Pocket016,Sketch083,SubtractivePipe002,Sketch091,Groove,LinearPattern003,Fillet003,Sketch099,Pocket022,LinearPattern004,Mirrored,Sketch128,+21 more]
  Origin = -> Origin043
  Tip = -> MultiTransform006
FEATURE [Sketcher::SketchObject] Sketch141
  ArcFitTolerance = 0
  AttachmentSupport = -> [XZ_Plane018]
  FullyConstrained = false
  MakeInternals = false
  MapMode = 5
  Placement = pos=(0,0,0) rot=(1,0,0;1.5708rad)
  sketch-geometry (4):
    g0: LineSegment StartX=-56 StartY=22 StartZ=0 EndX=75.498 EndY=22 EndZ=0
    g1: LineSegment StartX=75.498 StartY=22 StartZ=0 EndX=75.498 EndY=-52.4167 EndZ=0
    g2: LineSegment StartX=75.498 StartY=-52.4167 StartZ=0 EndX=-56 EndY=-52.4167 EndZ=0
    g3: LineSegment StartX=-56 StartY=-52.4167 StartZ=0 EndX=-56 EndY=22 EndZ=0
  constraints (10):
    c: Coincident(g0,g1)
    c: Coincident(g1,g2)
    c: Coincident(g2,g3)
    c: Coincident(g3,g0)
    c: Horizontal(g0)
    c: Horizontal(g2)
    c: Vertical(g1)
    c: Vertical(g3)
    c: DistanceY(g0) = 22
    c: DistanceX(g2) = -56
FEATURE [PartDesign::Pocket] Pocket030
  BaseFeature = -> SubtractivePipe006
  Direction = (0,1,2e-16)
  Length = 5
  Length2 = 100
  Profile = -> Sketch141
  Reversed = true
  Suppressed = false
  Type = 1
FEATURE [PartDesign::Body] Body017  label="Wall plate"
  AllowCompound = false
  Group = -> [Sketch027,Sketch028,Pad016,Sketch029,SubtractivePipe,Fillet,DatumPlane,Pocket009,Revolution,Sketch068,Groove001,MultiTransform002,Mirrored011,Mirrored012,Sketch069,Sketch084,AdditivePipe013,Sketch085,Pocket017,Sketch086,Pocket018,Sketch088,Sketch087,Pocket019,Pocket020,Sketch101,Sketch136,Pocket027,Sketch137,SubtractivePipe005,Sketch138,SubtractivePipe006,Sketch141,Pocket030]
  Origin = -> Origin018
  Tip = -> Pocket030
FEATURE [Sketcher::SketchObject] Sketch144
  ArcFitTolerance = 0
  AttachmentSupport = -> [XY_Plane064]
  FullyConstrained = true
  MakeInternals = false
  MapMode = 5
  sketch-geometry (4):
    g0: LineSegment StartX=7.5 StartY=-1.5 StartZ=0 EndX=7.5 EndY=-7 EndZ=0
    g1: LineSegment StartX=7.5 StartY=-7 StartZ=0 EndX=-7.5 EndY=-7 EndZ=0
    g2: LineSegment StartX=-7.5 StartY=-7 StartZ=0 EndX=-7.5 EndY=-1.5 EndZ=0
    g3: LineSegment StartX=-7.5 StartY=-1.5 StartZ=0 EndX=7.5 EndY=-1.5 EndZ=0
  constraints (11):
    c: Coincident(g0,g1)
    c: Coincident(g1,g2)
    c: Vertical(g0)
    c: Vertical(g2)
    c: Symmetric(g1,g0,g-2)
    c: DistanceX(g1,g1) = 15
    c: DistanceY(g3,g-1) = 1.5
    c: Coincident(g0,g3)
    c: Coincident(g2,g3)
    c: Horizontal(g3)
    c: DistanceY(g0,g-1) = 7
FEATURE [PartDesign::Pad] Pad031
  Direction = (0,0,1)
  Length = 13.5
  Length2 = 10
  Midplane = true
  Profile = -> Sketch144
  ReferenceAxis = -> Sketch144 [N_Axis]
  Suppressed = false
  Type = 0
FEATURE [Sketcher::SketchObject] Sketch145
  ArcFitTolerance = 0
  AttachmentSupport = -> [XY_Plane064]
  FullyConstrained = true
  MakeInternals = false
  MapMode = 5
  sketch-geometry (6):
    g0: LineSegment StartX=0 StartY=0 StartZ=0 EndX=0 EndY=-8 EndZ=0
    g1: LineSegment StartX=0 StartY=-8 StartZ=0 EndX=4 EndY=-8 EndZ=0
    g2: LineSegment StartX=4 StartY=-8 StartZ=0 EndX=4 EndY=-4 EndZ=0
    g3: LineSegment StartX=4 StartY=-4 StartZ=0 EndX=2 EndY=-4 EndZ=0
    g4: LineSegment StartX=2 StartY=-4 StartZ=0 EndX=2 EndY=0 EndZ=0
    g5: LineSegment StartX=2 StartY=0 StartZ=0 EndX=0 EndY=0 EndZ=0
  constraints (17):
    c: Coincident(g-1,g0)
    c: PointOnObject(g0,g-2)
    c: Coincident(g0,g1)
    c: Horizontal(g1)
    c: Coincident(g1,g2)
    c: Vertical(g2)
    c: Coincident(g2,g3)
    c: Horizontal(g3)
    c: Coincident(g3,g4)
    c: PointOnObject(g4,g-1)
    c: Coincident(g4,g5)
    c: Coincident(g5,g0)
    c: Vertical(g4)
    c: DistanceX(g5,g5) = 2
    c: DistanceX(g1,g1) = 4
    c: DistanceY(g2,g4) = 4
    c: DistanceY(g1,g0) = 8
FEATURE [PartDesign::Groove] Groove005
  Angle = 360
  Angle2 = 60
  Axis = (1e-16,1,-1e-16)
  Base = (0,0,0)
  BaseFeature = -> Pad031
  Profile = -> Sketch145
  ReferenceAxis = -> Y_Axis064
  Suppressed = false
  Type = 0
FEATURE [Sketcher::SketchObject] Sketch146
  ArcFitTolerance = 0
  AttachmentSupport = -> [XZ_Plane064]
  FullyConstrained = true
  MakeInternals = false
  MapMode = 5
  Placement = pos=(0,0,0) rot=(1,0,0;1.5708rad)
  sketch-geometry (4):
    g0: ArcOfCircle CenterX=0 CenterY=3 CenterZ=0 NormalX=0 NormalY=0 NormalZ=1 AngleXU=0 Radius=6.75 StartAngle=0 EndAngle=3.14159
    g1: ArcOfCircle CenterX=0 CenterY=-3 CenterZ=0 NormalX=0 NormalY=0 NormalZ=1 AngleXU=0 Radius=6.75 StartAngle=3.14159 EndAngle=6.28319
    g2: LineSegment StartX=-6.75 StartY=3 StartZ=0 EndX=-6.75 EndY=-3 EndZ=0
    g3: LineSegment StartX=6.75 StartY=-3 StartZ=0 EndX=6.75 EndY=3 EndZ=0
  constraints (9):
    c: Tangent(g0,g2) = -1.5708
    c: Tangent(g2,g1) = -1.5708
    c: Tangent(g1,g3) = -1.5708
    c: Tangent(g3,g0) = -1.5708
    c: Equal(g0,g1)
    c: PointOnObject(g0,g-2)
    c: Symmetric(g0,g1,g-1)
    c: DistanceY(g1,g0) = 6
    c: DistanceX(g0,g0) = 13.5
FEATURE [Sketcher::SketchObject] Sketch147
  ArcFitTolerance = 0
  AttachmentSupport = -> [XY_Plane064]
  FullyConstrained = true
  MakeInternals = false
  MapMode = 5
  sketch-geometry (6):
    g0: LineSegment StartX=4.25 StartY=0 StartZ=0 EndX=4.25 EndY=-3 EndZ=0
    g1: LineSegment StartX=4.25 StartY=-3 StartZ=0 EndX=6.7 EndY=-3 EndZ=0
    g2: LineSegment StartX=6.7 StartY=-3 StartZ=0 EndX=6.7 EndY=-8 EndZ=0
    g3: LineSegment StartX=6.7 StartY=-8 StartZ=0 EndX=10 EndY=-8 EndZ=0
    g4: LineSegment StartX=10 StartY=-8 StartZ=0 EndX=10 EndY=0 EndZ=0
    g5: LineSegment StartX=10 StartY=0 StartZ=0 EndX=4.25 EndY=0 EndZ=0
  constraints (18):
    c: PointOnObject(g0,g-1)
    c: Vertical(g0)
    c: Coincident(g0,g1)
    c: Horizontal(g1)
    c: Coincident(g1,g2)
    c: Vertical(g2)
    c: Coincident(g2,g3)
    c: Horizontal(g3)
    c: Coincident(g3,g4)
    c: PointOnObject(g4,g-1)
    c: Vertical(g4)
    c: Coincident(g4,g5)
    c: Coincident(g5,g0)
    c: DistanceX(g0) = 4.25
    c: DistanceX(g2) = 6.7
    c: DistanceX(g3) = 10
    c: DistanceY(g4,g4) = 8
    c: DistanceY(g1,g-1) = 3
FEATURE [PartDesign::SubtractivePipe] SubtractivePipe006002
  AuxilleryCurvelinear = true
  AuxillerySpineTangent = false
  BaseFeature = -> Groove005
  Binormal = (0,0,0)
  Mode = 0
  Profile = -> Sketch147
  Spine = -> Sketch146
  SpineTangent = false
  Suppressed = false
  Transformation = 0
  Transition = 0
FEATURE [PartDesign::Body] Body058  label="Screw interface L"
  AllowCompound = false
  Group = -> [Sketch144,Pad031,Sketch145,Groove005,Sketch146,Sketch147,SubtractivePipe006002]
  Origin = -> Origin064
  Placement = pos=(-50,0,-1) rot=(0,1,0;1.5708rad)
  Tip = -> SubtractivePipe006002
FEATURE [Sketcher::SketchObject] Sketch148
  ArcFitTolerance = 0
  AttachmentSupport = -> [XY_Plane065]
  FullyConstrained = true
  MakeInternals = false
  MapMode = 5
  sketch-geometry (4):
    g0: LineSegment StartX=7.5 StartY=-1.5 StartZ=0 EndX=7.5 EndY=-7 EndZ=0
    g1: LineSegment StartX=7.5 StartY=-7 StartZ=0 EndX=-7.5 EndY=-7 EndZ=0
    g2: LineSegment StartX=-7.5 StartY=-7 StartZ=0 EndX=-7.5 EndY=-1.5 EndZ=0
    g3: LineSegment StartX=-7.5 StartY=-1.5 StartZ=0 EndX=7.5 EndY=-1.5 EndZ=0
  constraints (11):
    c: Coincident(g0,g1)
    c: Coincident(g1,g2)
    c: Vertical(g0)
    c: Vertical(g2)
    c: Symmetric(g1,g0,g-2)
    c: DistanceX(g1,g1) = 15
    c: DistanceY(g3,g-1) = 1.5
    c: Coincident(g0,g3)
    c: Coincident(g2,g3)
    c: Horizontal(g3)
    c: DistanceY(g0,g-1) = 7
FEATURE [PartDesign::Pad] Pad032
  Direction = (0,0,1)
  Length = 13.5
  Length2 = 10
  Midplane = true
  Profile = -> Sketch148
  ReferenceAxis = -> Sketch148 [N_Axis]
  Suppressed = false
  Type = 0
FEATURE [Sketcher::SketchObject] Sketch149
  ArcFitTolerance = 0
  AttachmentSupport = -> [XY_Plane065]
  FullyConstrained = true
  MakeInternals = false
  MapMode = 5
  sketch-geometry (6):
    g0: LineSegment StartX=0 StartY=0 StartZ=0 EndX=0 EndY=-8 EndZ=0
    g1: LineSegment StartX=0 StartY=-8 StartZ=0 EndX=4 EndY=-8 EndZ=0
    g2: LineSegment StartX=4 StartY=-8 StartZ=0 EndX=4 EndY=-4 EndZ=0
    g3: LineSegment StartX=4 StartY=-4 StartZ=0 EndX=2 EndY=-4 EndZ=0
    g4: LineSegment StartX=2 StartY=-4 StartZ=0 EndX=2 EndY=0 EndZ=0
    g5: LineSegment StartX=2 StartY=0 StartZ=0 EndX=0 EndY=0 EndZ=0
  constraints (17):
    c: Coincident(g-1,g0)
    c: PointOnObject(g0,g-2)
    c: Coincident(g0,g1)
    c: Horizontal(g1)
    c: Coincident(g1,g2)
    c: Vertical(g2)
    c: Coincident(g2,g3)
    c: Horizontal(g3)
    c: Coincident(g3,g4)
    c: PointOnObject(g4,g-1)
    c: Coincident(g4,g5)
    c: Coincident(g5,g0)
    c: Vertical(g4)
    c: DistanceX(g5,g5) = 2
    c: DistanceX(g1,g1) = 4
    c: DistanceY(g2,g4) = 4
    c: DistanceY(g1,g0) = 8
FEATURE [PartDesign::Groove] Groove006
  Angle = 360
  Angle2 = 60
  Axis = (1e-16,1,-1e-16)
  Base = (0,0,0)
  BaseFeature = -> Pad032
  Profile = -> Sketch149
  ReferenceAxis = -> Y_Axis065
  Suppressed = false
  Type = 0
FEATURE [Sketcher::SketchObject] Sketch150
  ArcFitTolerance = 0
  AttachmentSupport = -> [XZ_Plane065]
  FullyConstrained = true
  MakeInternals = false
  MapMode = 5
  Placement = pos=(0,0,0) rot=(1,0,0;1.5708rad)
  sketch-geometry (4):
    g0: ArcOfCircle CenterX=0 CenterY=3 CenterZ=0 NormalX=0 NormalY=0 NormalZ=1 AngleXU=0 Radius=6.75 StartAngle=0 EndAngle=3.14159
    g1: ArcOfCircle CenterX=0 CenterY=-3 CenterZ=0 NormalX=0 NormalY=0 NormalZ=1 AngleXU=0 Radius=6.75 StartAngle=3.14159 EndAngle=6.28319
    g2: LineSegment StartX=-6.75 StartY=3 StartZ=0 EndX=-6.75 EndY=-3 EndZ=0
    g3: LineSegment StartX=6.75 StartY=-3 StartZ=0 EndX=6.75 EndY=3 EndZ=0
  constraints (9):
    c: Tangent(g0,g2) = -1.5708
    c: Tangent(g2,g1) = -1.5708
    c: Tangent(g1,g3) = -1.5708
    c: Tangent(g3,g0) = -1.5708
    c: Equal(g0,g1)
    c: PointOnObject(g0,g-2)
    c: Symmetric(g0,g1,g-1)
    c: DistanceY(g1,g0) = 6
    c: DistanceX(g0,g0) = 13.5
FEATURE [Sketcher::SketchObject] Sketch151
  ArcFitTolerance = 0
  AttachmentSupport = -> [XY_Plane065]
  FullyConstrained = true
  MakeInternals = false
  MapMode = 5
  sketch-geometry (6):
    g0: LineSegment StartX=4.25 StartY=0 StartZ=0 EndX=4.25 EndY=-3 EndZ=0
    g1: LineSegment StartX=4.25 StartY=-3 StartZ=0 EndX=6.7 EndY=-3 EndZ=0
    g2: LineSegment StartX=6.7 StartY=-3 StartZ=0 EndX=6.7 EndY=-8 EndZ=0
    g3: LineSegment StartX=6.7 StartY=-8 StartZ=0 EndX=10 EndY=-8 EndZ=0
    g4: LineSegment StartX=10 StartY=-8 StartZ=0 EndX=10 EndY=0 EndZ=0
    g5: LineSegment StartX=10 StartY=0 StartZ=0 EndX=4.25 EndY=0 EndZ=0
  constraints (18):
    c: PointOnObject(g0,g-1)
    c: Vertical(g0)
    c: Coincident(g0,g1)
    c: Horizontal(g1)
    c: Coincident(g1,g2)
    c: Vertical(g2)
    c: Coincident(g2,g3)
    c: Horizontal(g3)
    c: Coincident(g3,g4)
    c: PointOnObject(g4,g-1)
    c: Vertical(g4)
    c: Coincident(g4,g5)
    c: Coincident(g5,g0)
    c: DistanceX(g0) = 4.25
    c: DistanceX(g2) = 6.7
    c: DistanceX(g3) = 10
    c: DistanceY(g4,g4) = 8
    c: DistanceY(g1,g-1) = 3
FEATURE [PartDesign::SubtractivePipe] SubtractivePipe006003
  AuxilleryCurvelinear = true
  AuxillerySpineTangent = false
  BaseFeature = -> Groove006
  Binormal = (0,0,0)
  Mode = 0
  Profile = -> Sketch151
  Spine = -> Sketch150
  SpineTangent = false
  Suppressed = false
  Transformation = 0
  Transition = 0
FEATURE [PartDesign::Body] Body059  label="Screw interface R"
  AllowCompound = false
  Group = -> [Sketch148,Pad032,Sketch149,Groove006,Sketch150,Sketch151,SubtractivePipe006003]
  Origin = -> Origin065
  Placement = pos=(50,0,-1) rot=(0,1,0;3.14159rad)
  Tip = -> SubtractivePipe006003
FEATURE [Mesh::Feature] Mesh  label="Wall plate refined (Meshed)"
FEATURE [Mesh::Feature] Mesh001  label="Front panel (Meshed)"
